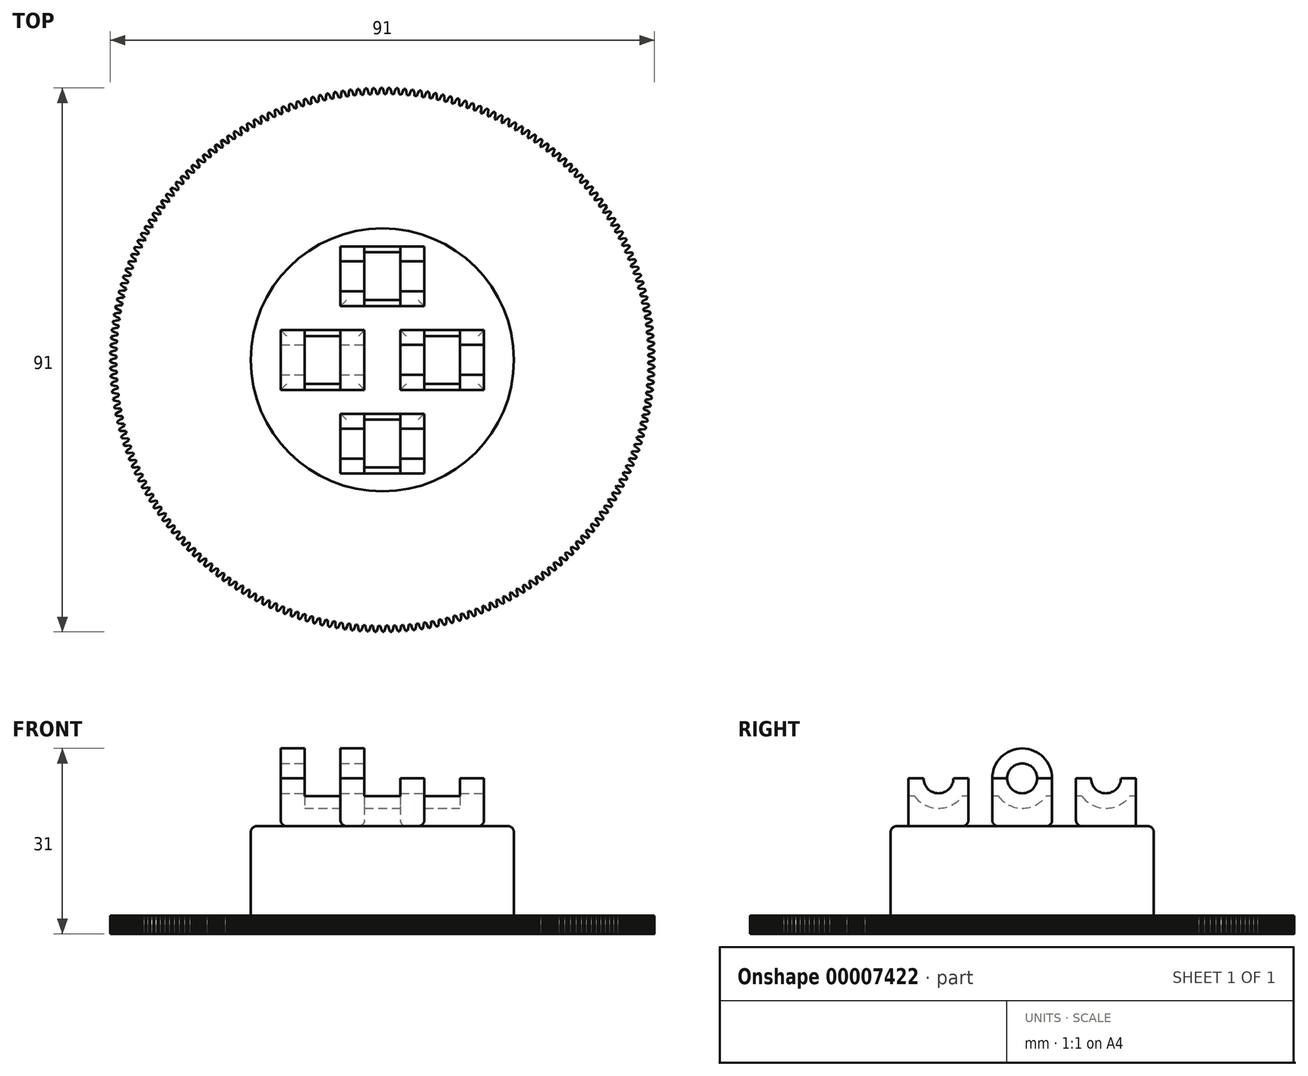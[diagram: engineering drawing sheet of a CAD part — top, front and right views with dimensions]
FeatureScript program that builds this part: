
annotation { "Feature Type Name" : "Feature", "Feature Type Description" : "" }
export const myFeature = defineFeature(function(context is Context, id is Id, definition is map)
    precondition{}
    {
        {
            var Q0;
            Q0=qCreatedBy(makeId("Top.planeOp"),FACE);
            var sketch = newSketch(context, id + "F0", { "sketchPlane" : qUnion([Q0])});
            skPoint(sketch, "E0.rect.middle", {"position": v(0, 0) * mm});
            skCircle(sketch, "E1", {"center": v(0, 0) * mm, "radius": 45.5 * mm});
            skSolve(sketch);
        }
        {
            var Q0;
            Q0=makeQuery(id+"F0.imprint","IMPRINT",FACE,{"disambiguationData":[TD([[makeQuery(id+"F0.imprint","IMPRINT",EDGE,{"derivedFrom":sQuery(id+"F0.wireOp",EDGE,"E1")}),1.0]])]});
            extrude(context, id + "F1", {"entities" : qUnion([Q0]), "depth" : 3 * mm});
        }
        {
            var Q0;
            Q0=makeQuery(id+"F1.opExtrude","CAP_FACE",FACE,{"disambiguationData":[OSD([sQuery(id+"F0.wireOp",EDGE,"E1")])],"isStart":false});
            var sketch = newSketch(context, id + "F2", { "sketchPlane" : qUnion([Q0])});
            skCircle(sketch, "E2", {"center": v(0, 0) * mm, "radius": 22 * mm});
            skSolve(sketch);
        }
        {
            var Q0;
            Q0=makeQuery(id+"F2.imprint","IMPRINT",FACE,{"disambiguationData":[TD([[makeQuery(id+"F2.imprint","IMPRINT",EDGE,{"derivedFrom":sQuery(id+"F2.wireOp",EDGE,"E2")}),1.0]])]});
            extrude(context, id + "F3", {"entities" : qUnion([Q0]), "operationType" : NewBodyOperationType.ADD, "depth" : 15 * mm});
        }
        {
            var Q0;
            Q0=makeQuery(id+"F3.opExtrude","CAP_FACE",FACE,{"disambiguationData":[OSD([sQuery(id+"F2.wireOp",EDGE,"E2")])],"isStart":false});
            var sketch = newSketch(context, id + "F4", { "sketchPlane" : qUnion([Q0])});
            skLineSegment(sketch, "E3", {"start": v(-22, 0) * mm, "end": v(22, 0) * mm});
            skPoint(sketch, "E4", {"position": v(-20, 0) * mm});
            skPoint(sketch, "E5", {"position": v(-10, 0) * mm});
            skLineSegment(sketch, "E6.rect.bottom", {"start": v(-3, 5) * mm, "end": v(-17, 5) * mm});
            skLineSegment(sketch, "E6.rect.top", {"start": v(-3, -5) * mm, "end": v(-17, -5) * mm});
            skLineSegment(sketch, "E6.rect.left", {"start": v(-3, 5) * mm, "end": v(-3, -5) * mm});
            skLineSegment(sketch, "E6.rect.right", {"start": v(-17, 5) * mm, "end": v(-17, -5) * mm});
            skSolve(sketch);
        }
        {
            var Q0;
            Q0=qSketchRegion(id+"F4",true);
            extrude(context, id + "F5", {"entities" : qUnion([Q0]), "depth" : 8 * mm});
        }
        {
            var Q0;
            Q0=makeQuery(id+"F5.opExtrude","SWEPT_FACE",FACE,{"disambiguationData":[OSD([sQuery(id+"F4.wireOp",EDGE,"E6.rect.left")])]});
            var sketch = newSketch(context, id + "F6", { "sketchPlane" : qUnion([Q0])});
            skPoint(sketch, "E7", {"position": v(0, 26) * mm});
            skCircle(sketch, "E8", {"center": v(0, 26) * mm, "radius": 5 * mm});
            skSolve(sketch);
        }
        {
            var Q0;
            {var subQ0=sQuery(id+"F4.wireOp",EDGE,"E6.rect.left");var subQ1=makeQuery(id+"F5.opExtrude","CAP_EDGE",EDGE,{"disambiguationData":[OSD([subQ0])],"isStart":false});Q0=makeQuery(id+"F6.imprint","IMPRINT",FACE,{"disambiguationData":[TD([[makeQuery(id+"F6.imprint","IMPRINT",EDGE,{"derivedFrom":subQ1}),-1.0]])]});}
            extrude(context, id + "F7", {"entities" : qUnion([Q0]), "oppositeDirection" : true, "depth" : 14 * mm});
        }
        {
            var Q0;
            Q0=makeQuery(id+"F7.opExtrude","CAP_FACE",FACE,{"disambiguationData":[OSD([sQuery(id+"F4.wireOp",EDGE,"E6.rect.left"),sQuery(id+"F6.wireOp",EDGE,"E8")])],"isStart":true});
            var sketch = newSketch(context, id + "F8", { "sketchPlane" : qUnion([Q0])});
            skPoint(sketch, "E9", {"position": v(0, 26) * mm});
            skCircle(sketch, "E10", {"center": v(0, 26) * mm, "radius": 2.5 * mm});
            skSolve(sketch);
        }
        {
            var Q0;
            {var subQ0=makeQuery(id+"F7.opExtrude","CAP_EDGE",EDGE,{"disambiguationData":[OSD([sQuery(id+"F4.wireOp",EDGE,"E6.rect.left")])],"isStart":true});var subQ1=sQuery(id+"F8.wireOp",EDGE,"E10");var subQ3=makeQuery(id+"F8.imprint","INTERSECT",VERTEX,{"disambiguationData":[OD(0.0)],"derivedFrom":[subQ0,subQ1]});Q0=makeQuery(id+"F8.imprint","IMPRINT",FACE,{"disambiguationData":[TD([[makeQuery(id+"F8.imprint","IMPRINT",EDGE,{"disambiguationData":[TD([[subQ3,1.0]])],"derivedFrom":subQ1}),1.0]])]});}
            var Q1;
            {var subQ0=makeQuery(id+"F7.opExtrude","CAP_EDGE",EDGE,{"disambiguationData":[OSD([sQuery(id+"F4.wireOp",EDGE,"E6.rect.left")])],"isStart":true});var subQ1=sQuery(id+"F8.wireOp",EDGE,"E10");var subQ3=makeQuery(id+"F8.imprint","INTERSECT",VERTEX,{"disambiguationData":[OD(0.0)],"derivedFrom":[subQ0,subQ1]});Q1=makeQuery(id+"F8.imprint","IMPRINT",FACE,{"disambiguationData":[TD([[makeQuery(id+"F8.imprint","IMPRINT",EDGE,{"disambiguationData":[TD([[subQ3,-1.0]])],"derivedFrom":subQ1}),1.0]])]});}
            extrude(context, id + "F9", {"entities" : qUnion([Q0, Q1]), "operationType" : NewBodyOperationType.REMOVE, "endBound" : BoundingType.THROUGH_ALL, "oppositeDirection" : true, "depth" : 25 * mm});
        }
        {
            var Q0;
            Q0=makeQuery(id+"F7.opExtrude","CAP_FACE",FACE,{"disambiguationData":[OSD([sQuery(id+"F4.wireOp",EDGE,"E6.rect.left"),sQuery(id+"F6.wireOp",EDGE,"E8")])],"isStart":true});
            cPlane(context, id + "F10", {"entities" : qUnion([Q0]), "cplaneType" : CPlaneType.OFFSET, "offset" : 4 * mm, "oppositeDirection" : true, "width" : 150 * mm, "height" : 150 * mm});
        }
        {
            var Q0;
            Q0=qCreatedBy(id+"F10.planeOp",FACE);
            var sketch = newSketch(context, id + "F11", { "sketchPlane" : qUnion([Q0])});
            skCircle(sketch, "E11", {"center": v(0, 26) * mm, "radius": 5 * mm});
            skSolve(sketch);
        }
        {
            var Q0;
            Q0=qSketchRegion(id+"F11",true);
            extrude(context, id + "F12", {"entities" : qUnion([Q0]), "operationType" : NewBodyOperationType.REMOVE, "oppositeDirection" : true, "depth" : 6 * mm});
        }
        {
            var Q0;
            Q0=makeQuery(id+"F5.opExtrude","SWEPT_FACE",FACE,{"disambiguationData":[OSD([sQuery(id+"F4.wireOp",EDGE,"E6.rect.top")])]});
            var sketch = newSketch(context, id + "F13", { "sketchPlane" : qUnion([Q0])});
            skLineSegment(sketch, "E12.bottom", {"start": v(-13, 26) * mm, "end": v(-7, 26) * mm});
            skLineSegment(sketch, "E12.top", {"start": v(-13, 23) * mm, "end": v(-7, 23) * mm});
            skLineSegment(sketch, "E12.left", {"start": v(-13, 26) * mm, "end": v(-13, 23) * mm});
            skLineSegment(sketch, "E12.right", {"start": v(-7, 26) * mm, "end": v(-7, 23) * mm});
            skSolve(sketch);
        }
        {
            var Q0;
            Q0=makeQuery(id+"F13.imprint","IMPRINT",FACE,{"disambiguationData":[TD([[makeQuery(id+"F13.imprint","IMPRINT",EDGE,{"derivedFrom":sQuery(id+"F13.wireOp",EDGE,"E12.bottom")}),-1.0]])]});
            extrude(context, id + "F14", {"entities" : qUnion([Q0]), "operationType" : NewBodyOperationType.REMOVE, "endBound" : BoundingType.THROUGH_ALL, "oppositeDirection" : true, "depth" : 25 * mm});
        }
        {
            var Q0;
            Q0=makeQuery(id+"F5.opExtrude","SWEPT_BODY",BODY,{"disambiguationData":[OSD([sQuery(id+"F4.wireOp",EDGE,"E6.rect.bottom"),sQuery(id+"F4.wireOp",EDGE,"E6.rect.top"),sQuery(id+"F4.wireOp",EDGE,"E6.rect.left"),sQuery(id+"F4.wireOp",EDGE,"E6.rect.right")])]});
            transform(context, id + "F15", {"entities" : qUnion([Q0]), "transformType" : TransformType.TRANSLATION_3D, "dx" : 20 * mm, "dy" : 0 * mm, "dz" : 0 * mm, "makeCopy" : true});
        }
        {
            var Q0;
            Q0=makeQuery(id+"F5.opExtrude","SWEPT_BODY",BODY,{"disambiguationData":[OSD([sQuery(id+"F4.wireOp",EDGE,"E6.rect.bottom"),sQuery(id+"F4.wireOp",EDGE,"E6.rect.top"),sQuery(id+"F4.wireOp",EDGE,"E6.rect.left"),sQuery(id+"F4.wireOp",EDGE,"E6.rect.right")])]});
            transform(context, id + "F16", {"entities" : qUnion([Q0]), "transformType" : TransformType.TRANSLATION_3D, "dx" : 10 * mm, "dy" : 14 * mm, "dz" : 0 * mm, "makeCopy" : true});
        }
        {
            var Q0;
            Q0=makeQuery(id+"F5.opExtrude","SWEPT_BODY",BODY,{"disambiguationData":[OSD([sQuery(id+"F4.wireOp",EDGE,"E6.rect.bottom"),sQuery(id+"F4.wireOp",EDGE,"E6.rect.top"),sQuery(id+"F4.wireOp",EDGE,"E6.rect.left"),sQuery(id+"F4.wireOp",EDGE,"E6.rect.right")])]});
            transform(context, id + "F17", {"entities" : qUnion([Q0]), "transformType" : TransformType.TRANSLATION_3D, "dx" : 10 * mm, "dy" : -14 * mm, "dz" : 0 * mm, "makeCopy" : true});
        }
        {
            var Q0;
            Q0=makeQuery(id+"F3.opExtrude","CAP_EDGE",EDGE,{"disambiguationData":[OSD([sQuery(id+"F2.wireOp",EDGE,"E2")])],"isStart":false});
            var Q1;
            Q1=makeQuery(id+"FjqFsmPxTx0BuLd_1.opFillet","BLEND_EDGE",EDGE,{"blendedFrom":[makeQuery(id+"F5.opExtrude","CAP_EDGE",EDGE,{"disambiguationData":[OSD([sQuery(id+"F4.wireOp",EDGE,"E6.rect.right")])],"isStart":true}),makeQuery(id+"F3.opExtrude","SWEPT_FACE",FACE,{"disambiguationData":[OSD([sQuery(id+"F2.wireOp",EDGE,"E2")])]})],"blendedInto":[makeQuery(id+"F3.opExtrude","SWEPT_FACE",FACE,{"disambiguationData":[OSD([sQuery(id+"F2.wireOp",EDGE,"E2")])]})]});
            var Q2;
            Q2=makeQuery(id+"FjqFsmPxTx0BuLd_1.opFillet","BLEND_EDGE",EDGE,{"blendedFrom":[makeQuery(id+"F15.opPattern","COPY",EDGE,{"derivedFrom":makeQuery(id+"F5.opExtrude","CAP_EDGE",EDGE,{"disambiguationData":[OSD([sQuery(id+"F4.wireOp",EDGE,"E6.rect.left")])],"isStart":true}),"instanceName":"1"}),makeQuery(id+"F3.opExtrude","SWEPT_FACE",FACE,{"disambiguationData":[OSD([sQuery(id+"F2.wireOp",EDGE,"E2")])]})],"blendedInto":[makeQuery(id+"F3.opExtrude","SWEPT_FACE",FACE,{"disambiguationData":[OSD([sQuery(id+"F2.wireOp",EDGE,"E2")])]})]});
            fillet(context, id + "F18", {"entities" : qUnion([Q0, Q1, Q2]), "radius" : 1 * mm, "tangentPropagation" : true, "allowEdgeOverflow" : false});
        }
        {
            var Q0;
            Q0=makeQuery(id+"F5.opExtrude","CAP_EDGE",EDGE,{"disambiguationData":[OSD([sQuery(id+"F4.wireOp",EDGE,"E6.rect.right")])],"isStart":true});
            var Q1;
            Q1=makeQuery(id+"F16.opPattern","COPY",EDGE,{"derivedFrom":makeQuery(id+"F5.opExtrude","CAP_EDGE",EDGE,{"disambiguationData":[OSD([sQuery(id+"F4.wireOp",EDGE,"E6.rect.right")])],"isStart":true}),"instanceName":"1"});
            var Q2;
            Q2=makeQuery(id+"F17.opPattern","COPY",EDGE,{"derivedFrom":makeQuery(id+"F5.opExtrude","CAP_EDGE",EDGE,{"disambiguationData":[OSD([sQuery(id+"F4.wireOp",EDGE,"E6.rect.right")])],"isStart":true}),"instanceName":"1"});
            var Q3;
            Q3=makeQuery(id+"F17.opPattern","COPY",EDGE,{"derivedFrom":makeQuery(id+"F5.opExtrude","CAP_EDGE",EDGE,{"disambiguationData":[OSD([sQuery(id+"F4.wireOp",EDGE,"E6.rect.left")])],"isStart":true}),"instanceName":"1"});
            var Q4;
            Q4=makeQuery(id+"F15.opPattern","COPY",EDGE,{"derivedFrom":makeQuery(id+"F5.opExtrude","CAP_EDGE",EDGE,{"disambiguationData":[OSD([sQuery(id+"F4.wireOp",EDGE,"E6.rect.left")])],"isStart":true}),"instanceName":"1"});
            var Q5;
            Q5=makeQuery(id+"F16.opPattern","COPY",EDGE,{"derivedFrom":makeQuery(id+"F5.opExtrude","CAP_EDGE",EDGE,{"disambiguationData":[OSD([sQuery(id+"F4.wireOp",EDGE,"E6.rect.left")])],"isStart":true}),"instanceName":"1"});
            var Q6;
            Q6=makeQuery(id+"F15.opPattern","COPY",EDGE,{"derivedFrom":makeQuery(id+"F5.opExtrude","CAP_EDGE",EDGE,{"disambiguationData":[OSD([sQuery(id+"F4.wireOp",EDGE,"E6.rect.right")])],"isStart":true}),"instanceName":"1"});
            var Q7;
            Q7=makeQuery(id+"F5.opExtrude","CAP_EDGE",EDGE,{"disambiguationData":[OSD([sQuery(id+"F4.wireOp",EDGE,"E6.rect.left")])],"isStart":true});
            var Q8;
            Q8=makeQuery(id+"F5.opExtrude","CAP_EDGE",EDGE,{"disambiguationData":[OSD([sQuery(id+"F4.wireOp",EDGE,"E6.rect.top")])],"isStart":true});
            var Q9;
            Q9=makeQuery(id+"F15.opPattern","COPY",EDGE,{"derivedFrom":makeQuery(id+"F5.opExtrude","CAP_EDGE",EDGE,{"disambiguationData":[OSD([sQuery(id+"F4.wireOp",EDGE,"E6.rect.top")])],"isStart":true}),"instanceName":"1"});
            var Q10;
            Q10=makeQuery(id+"F16.opPattern","COPY",EDGE,{"derivedFrom":makeQuery(id+"F5.opExtrude","CAP_EDGE",EDGE,{"disambiguationData":[OSD([sQuery(id+"F4.wireOp",EDGE,"E6.rect.top")])],"isStart":true}),"instanceName":"1"});
            var Q11;
            Q11=makeQuery(id+"F15.opPattern","COPY",EDGE,{"derivedFrom":makeQuery(id+"F5.opExtrude","CAP_EDGE",EDGE,{"disambiguationData":[OSD([sQuery(id+"F4.wireOp",EDGE,"E6.rect.bottom")])],"isStart":true}),"instanceName":"1"});
            var Q12;
            Q12=makeQuery(id+"F5.opExtrude","CAP_EDGE",EDGE,{"disambiguationData":[OSD([sQuery(id+"F4.wireOp",EDGE,"E6.rect.bottom")])],"isStart":true});
            var Q13;
            Q13=makeQuery(id+"F17.opPattern","COPY",EDGE,{"derivedFrom":makeQuery(id+"F5.opExtrude","CAP_EDGE",EDGE,{"disambiguationData":[OSD([sQuery(id+"F4.wireOp",EDGE,"E6.rect.bottom")])],"isStart":true}),"instanceName":"1"});
            fillet(context, id + "F19", {"entities" : qUnion([Q0, Q1, Q2, Q3, Q4, Q5, Q6, Q7, Q8, Q9, Q10, Q11, Q12, Q13]), "radius" : 1 * mm, "tangentPropagation" : true, "allowEdgeOverflow" : false});
        }
        {
            var Q0;
            Q0=makeQuery(id+"F1.opExtrude","CAP_FACE",FACE,{"disambiguationData":[OSD([sQuery(id+"F0.wireOp",EDGE,"E1")])],"isStart":false});
            var sketch = newSketch(context, id + "F20", { "sketchPlane" : qUnion([Q0])});
            skLineSegment(sketch, "E13", {"start": v(0, 0) * mm, "end": v(0, 45.5) * mm, "construction": true});
            skLineSegment(sketch, "E14", {"start": v(0, 0) * mm, "end": v(1, 45.49) * mm, "construction": true});
            skPoint(sketch, "E15", {"position": v(0, 44.5) * mm});
            skPoint(sketch, "E16", {"position": v(0.98, 44.49) * mm});
            skLineSegment(sketch, "E17", {"start": v(0, 44.5) * mm, "end": v(0.98, 44.49) * mm, "construction": true});
            skPoint(sketch, "E18", {"position": v(0.3, 44.5) * mm});
            skPoint(sketch, "E19", {"position": v(0.68, 44.5) * mm});
            skPoint(sketch, "E20", {"position": v(0.99, 44.99) * mm});
            skPoint(sketch, "E21", {"position": v(0, 44.99) * mm});
            skLineSegment(sketch, "E22", {"start": v(0, 44.99) * mm, "end": v(0.99, 44.99) * mm, "construction": true});
            skPoint(sketch, "E23", {"position": v(0.2, 44.99) * mm});
            skPoint(sketch, "E24", {"position": v(0.79, 44.99) * mm});
            skLineSegment(sketch, "E25", {"start": v(0, 45.5) * mm, "end": v(0.2, 44.99) * mm});
            skLineSegment(sketch, "E26", {"start": v(0.2, 44.99) * mm, "end": v(0.3, 44.5) * mm});
            skLineSegment(sketch, "E27", {"start": v(0.68, 44.5) * mm, "end": v(0.3, 44.5) * mm});
            skLineSegment(sketch, "E28", {"start": v(0.68, 44.5) * mm, "end": v(0.79, 44.99) * mm});
            skLineSegment(sketch, "E29", {"start": v(1, 45.49) * mm, "end": v(0.79, 44.99) * mm});
            skLineSegment(sketch, "E30.1.0", {"start": v(-1.3, 45.48) * mm, "end": v(-1.08, 44.98) * mm});
            skLineSegment(sketch, "E30.1.1", {"start": v(-1.08, 44.98) * mm, "end": v(-0.97, 44.49) * mm});
            skLineSegment(sketch, "E30.1.2", {"start": v(-0.6, 44.5) * mm, "end": v(-0.97, 44.49) * mm});
            skLineSegment(sketch, "E30.1.3", {"start": v(-0.6, 44.5) * mm, "end": v(-0.5, 45) * mm});
            skLineSegment(sketch, "E30.1.4", {"start": v(-0.3, 45.5) * mm, "end": v(-0.5, 45) * mm});
            skLineSegment(sketch, "E30.2.0", {"start": v(-2.6, 45.43) * mm, "end": v(-2.37, 44.93) * mm});
            skLineSegment(sketch, "E30.2.1", {"start": v(-2.37, 44.93) * mm, "end": v(-2.24, 44.44) * mm});
            skLineSegment(sketch, "E30.2.2", {"start": v(-1.86, 44.46) * mm, "end": v(-2.24, 44.44) * mm});
            skLineSegment(sketch, "E30.2.3", {"start": v(-1.86, 44.46) * mm, "end": v(-1.78, 44.96) * mm});
            skLineSegment(sketch, "E30.2.4", {"start": v(-1.6, 45.47) * mm, "end": v(-1.78, 44.96) * mm});
            skLineSegment(sketch, "E30.3.0", {"start": v(-3.9, 45.33) * mm, "end": v(-3.65, 44.84) * mm});
            skLineSegment(sketch, "E30.3.1", {"start": v(-3.65, 44.84) * mm, "end": v(-3.5, 44.36) * mm});
            skLineSegment(sketch, "E30.3.2", {"start": v(-3.13, 44.39) * mm, "end": v(-3.5, 44.36) * mm});
            skLineSegment(sketch, "E30.3.3", {"start": v(-3.13, 44.39) * mm, "end": v(-3.06, 44.9) * mm});
            skLineSegment(sketch, "E30.3.4", {"start": v(-2.9, 45.4) * mm, "end": v(-3.06, 44.9) * mm});
            skLineSegment(sketch, "E30.4.0", {"start": v(-5.19, 45.2) * mm, "end": v(-4.93, 44.72) * mm});
            skLineSegment(sketch, "E30.4.1", {"start": v(-4.93, 44.72) * mm, "end": v(-4.77, 44.24) * mm});
            skLineSegment(sketch, "E30.4.2", {"start": v(-4.4, 44.28) * mm, "end": v(-4.77, 44.24) * mm});
            skLineSegment(sketch, "E30.4.3", {"start": v(-4.4, 44.28) * mm, "end": v(-4.34, 44.79) * mm});
            skLineSegment(sketch, "E30.4.4", {"start": v(-4.2, 45.3) * mm, "end": v(-4.34, 44.79) * mm});
            skLineSegment(sketch, "E30.5.0", {"start": v(-6.48, 45.04) * mm, "end": v(-6.2, 44.56) * mm});
            skLineSegment(sketch, "E30.5.1", {"start": v(-6.2, 44.56) * mm, "end": v(-6.04, 44.09) * mm});
            skLineSegment(sketch, "E30.5.2", {"start": v(-5.66, 44.14) * mm, "end": v(-6.04, 44.09) * mm});
            skLineSegment(sketch, "E30.5.3", {"start": v(-5.66, 44.14) * mm, "end": v(-5.62, 44.64) * mm});
            skLineSegment(sketch, "E30.5.4", {"start": v(-5.48, 45.17) * mm, "end": v(-5.62, 44.64) * mm});
            skLineSegment(sketch, "E30.6.0", {"start": v(-7.76, 44.83) * mm, "end": v(-7.47, 44.36) * mm});
            skLineSegment(sketch, "E30.6.1", {"start": v(-7.47, 44.36) * mm, "end": v(-7.3, 43.9) * mm});
            skLineSegment(sketch, "E30.6.2", {"start": v(-6.92, 43.96) * mm, "end": v(-7.3, 43.9) * mm});
            skLineSegment(sketch, "E30.6.3", {"start": v(-6.92, 43.96) * mm, "end": v(-6.9, 44.46) * mm});
            skLineSegment(sketch, "E30.6.4", {"start": v(-6.77, 45) * mm, "end": v(-6.9, 44.46) * mm});
            skLineSegment(sketch, "E30.7.0", {"start": v(-9.04, 44.6) * mm, "end": v(-8.74, 44.13) * mm});
            skLineSegment(sketch, "E30.7.1", {"start": v(-8.74, 44.13) * mm, "end": v(-8.54, 43.67) * mm});
            skLineSegment(sketch, "E30.7.2", {"start": v(-8.17, 43.74) * mm, "end": v(-8.54, 43.67) * mm});
            skLineSegment(sketch, "E30.7.3", {"start": v(-8.17, 43.74) * mm, "end": v(-8.16, 44.25) * mm});
            skLineSegment(sketch, "E30.7.4", {"start": v(-8.05, 44.78) * mm, "end": v(-8.16, 44.25) * mm});
            skLineSegment(sketch, "E30.8.0", {"start": v(-10.3, 44.32) * mm, "end": v(-10, 43.87) * mm});
            skLineSegment(sketch, "E30.8.1", {"start": v(-10, 43.87) * mm, "end": v(-9.79, 43.4) * mm});
            skLineSegment(sketch, "E30.8.2", {"start": v(-9.42, 43.49) * mm, "end": v(-9.79, 43.4) * mm});
            skLineSegment(sketch, "E30.8.3", {"start": v(-9.42, 43.49) * mm, "end": v(-9.42, 44) * mm});
            skLineSegment(sketch, "E30.8.4", {"start": v(-9.33, 44.53) * mm, "end": v(-9.42, 44) * mm});
            skLineSegment(sketch, "E30.9.0", {"start": v(-11.57, 44) * mm, "end": v(-11.24, 43.56) * mm});
            skLineSegment(sketch, "E30.9.1", {"start": v(-11.24, 43.56) * mm, "end": v(-11.02, 43.11) * mm});
            skLineSegment(sketch, "E30.9.2", {"start": v(-10.66, 43.2) * mm, "end": v(-11.02, 43.11) * mm});
            skLineSegment(sketch, "E30.9.3", {"start": v(-10.66, 43.2) * mm, "end": v(-10.67, 43.71) * mm});
            skLineSegment(sketch, "E30.9.4", {"start": v(-10.6, 44.25) * mm, "end": v(-10.67, 43.71) * mm});
            skLineSegment(sketch, "E30.10.0", {"start": v(-12.82, 43.66) * mm, "end": v(-12.48, 43.22) * mm});
            skLineSegment(sketch, "E30.10.1", {"start": v(-12.48, 43.22) * mm, "end": v(-12.25, 42.78) * mm});
            skLineSegment(sketch, "E30.10.2", {"start": v(-11.88, 42.88) * mm, "end": v(-12.25, 42.78) * mm});
            skLineSegment(sketch, "E30.10.3", {"start": v(-11.88, 42.88) * mm, "end": v(-11.92, 43.39) * mm});
            skLineSegment(sketch, "E30.10.4", {"start": v(-11.86, 43.93) * mm, "end": v(-11.92, 43.39) * mm});
            skLineSegment(sketch, "E30.11.0", {"start": v(-14.06, 43.27) * mm, "end": v(-13.71, 42.85) * mm});
            skLineSegment(sketch, "E30.11.1", {"start": v(-13.71, 42.85) * mm, "end": v(-13.46, 42.41) * mm});
            skLineSegment(sketch, "E30.11.2", {"start": v(-13.1, 42.52) * mm, "end": v(-13.46, 42.41) * mm});
            skLineSegment(sketch, "E30.11.3", {"start": v(-13.1, 42.52) * mm, "end": v(-13.15, 43.03) * mm});
            skLineSegment(sketch, "E30.11.4", {"start": v(-13.1, 43.57) * mm, "end": v(-13.15, 43.03) * mm});
            skLineSegment(sketch, "E30.12.0", {"start": v(-15.3, 42.85) * mm, "end": v(-14.93, 42.44) * mm});
            skLineSegment(sketch, "E30.12.1", {"start": v(-14.93, 42.44) * mm, "end": v(-14.67, 42) * mm});
            skLineSegment(sketch, "E30.12.2", {"start": v(-14.31, 42.13) * mm, "end": v(-14.67, 42) * mm});
            skLineSegment(sketch, "E30.12.3", {"start": v(-14.31, 42.13) * mm, "end": v(-14.38, 42.64) * mm});
            skLineSegment(sketch, "E30.12.4", {"start": v(-14.34, 43.18) * mm, "end": v(-14.38, 42.64) * mm});
            skLineSegment(sketch, "E30.13.0", {"start": v(-16.5, 42.4) * mm, "end": v(-16.14, 42) * mm});
            skLineSegment(sketch, "E30.13.1", {"start": v(-16.14, 42) * mm, "end": v(-15.86, 41.57) * mm});
            skLineSegment(sketch, "E30.13.2", {"start": v(-15.51, 41.7) * mm, "end": v(-15.86, 41.57) * mm});
            skLineSegment(sketch, "E30.13.3", {"start": v(-15.51, 41.7) * mm, "end": v(-15.59, 42.2) * mm});
            skLineSegment(sketch, "E30.13.4", {"start": v(-15.57, 42.75) * mm, "end": v(-15.59, 42.2) * mm});
            skLineSegment(sketch, "E30.14.0", {"start": v(-17.71, 41.91) * mm, "end": v(-17.33, 41.52) * mm});
            skLineSegment(sketch, "E30.14.1", {"start": v(-17.33, 41.52) * mm, "end": v(-17.04, 41.1) * mm});
            skLineSegment(sketch, "E30.14.2", {"start": v(-16.7, 41.25) * mm, "end": v(-17.04, 41.1) * mm});
            skLineSegment(sketch, "E30.14.3", {"start": v(-16.7, 41.25) * mm, "end": v(-16.79, 41.75) * mm});
            skLineSegment(sketch, "E30.14.4", {"start": v(-16.79, 42.3) * mm, "end": v(-16.79, 41.75) * mm});
            skLineSegment(sketch, "E30.15.0", {"start": v(-18.9, 41.39) * mm, "end": v(-18.5, 41) * mm});
            skLineSegment(sketch, "E30.15.1", {"start": v(-18.5, 41) * mm, "end": v(-18.21, 40.6) * mm});
            skLineSegment(sketch, "E30.15.2", {"start": v(-17.87, 40.75) * mm, "end": v(-18.21, 40.6) * mm});
            skLineSegment(sketch, "E30.15.3", {"start": v(-17.87, 40.75) * mm, "end": v(-17.97, 41.25) * mm});
            skLineSegment(sketch, "E30.15.4", {"start": v(-17.99, 41.8) * mm, "end": v(-17.97, 41.25) * mm});
            skLineSegment(sketch, "E30.16.0", {"start": v(-20.08, 40.83) * mm, "end": v(-19.67, 40.46) * mm});
            skLineSegment(sketch, "E30.16.1", {"start": v(-19.67, 40.46) * mm, "end": v(-19.36, 40.06) * mm});
            skLineSegment(sketch, "E30.16.2", {"start": v(-19.02, 40.23) * mm, "end": v(-19.36, 40.06) * mm});
            skLineSegment(sketch, "E30.16.3", {"start": v(-19.02, 40.23) * mm, "end": v(-19.14, 40.72) * mm});
            skLineSegment(sketch, "E30.16.4", {"start": v(-19.17, 41.26) * mm, "end": v(-19.14, 40.72) * mm});
            skLineSegment(sketch, "E30.17.0", {"start": v(-21.23, 40.24) * mm, "end": v(-20.82, 39.88) * mm});
            skLineSegment(sketch, "E30.17.1", {"start": v(-20.82, 39.88) * mm, "end": v(-20.5, 39.5) * mm});
            skLineSegment(sketch, "E30.17.2", {"start": v(-20.16, 39.67) * mm, "end": v(-20.5, 39.5) * mm});
            skLineSegment(sketch, "E30.17.3", {"start": v(-20.16, 39.67) * mm, "end": v(-20.3, 40.16) * mm});
            skLineSegment(sketch, "E30.17.4", {"start": v(-20.34, 40.7) * mm, "end": v(-20.3, 40.16) * mm});
            skLineSegment(sketch, "E30.18.0", {"start": v(-22.37, 39.62) * mm, "end": v(-21.95, 39.27) * mm});
            skLineSegment(sketch, "E30.18.1", {"start": v(-21.95, 39.27) * mm, "end": v(-21.62, 38.9) * mm});
            skLineSegment(sketch, "E30.18.2", {"start": v(-21.29, 39.07) * mm, "end": v(-21.62, 38.9) * mm});
            skLineSegment(sketch, "E30.18.3", {"start": v(-21.29, 39.07) * mm, "end": v(-21.44, 39.56) * mm});
            skLineSegment(sketch, "E30.18.4", {"start": v(-21.5, 40.1) * mm, "end": v(-21.44, 39.56) * mm});
            skLineSegment(sketch, "E30.19.0", {"start": v(-23.5, 38.96) * mm, "end": v(-23.06, 38.63) * mm});
            skLineSegment(sketch, "E30.19.1", {"start": v(-23.06, 38.63) * mm, "end": v(-22.72, 38.26) * mm});
            skLineSegment(sketch, "E30.19.2", {"start": v(-22.4, 38.45) * mm, "end": v(-22.72, 38.26) * mm});
            skLineSegment(sketch, "E30.19.3", {"start": v(-22.4, 38.45) * mm, "end": v(-22.56, 38.93) * mm});
            skLineSegment(sketch, "E30.19.4", {"start": v(-22.63, 39.47) * mm, "end": v(-22.56, 38.93) * mm});
            skLineSegment(sketch, "E30.20.0", {"start": v(-24.6, 38.28) * mm, "end": v(-24.15, 37.96) * mm});
            skLineSegment(sketch, "E30.20.1", {"start": v(-24.15, 37.96) * mm, "end": v(-23.8, 37.6) * mm});
            skLineSegment(sketch, "E30.20.2", {"start": v(-23.48, 37.8) * mm, "end": v(-23.8, 37.6) * mm});
            skLineSegment(sketch, "E30.20.3", {"start": v(-23.48, 37.8) * mm, "end": v(-23.66, 38.27) * mm});
            skLineSegment(sketch, "E30.20.4", {"start": v(-23.75, 38.8) * mm, "end": v(-23.66, 38.27) * mm});
            skLineSegment(sketch, "E30.21.0", {"start": v(-25.68, 37.56) * mm, "end": v(-25.23, 37.25) * mm});
            skLineSegment(sketch, "E30.21.1", {"start": v(-25.23, 37.25) * mm, "end": v(-24.87, 36.9) * mm});
            skLineSegment(sketch, "E30.21.2", {"start": v(-24.55, 37.1) * mm, "end": v(-24.87, 36.9) * mm});
            skLineSegment(sketch, "E30.21.3", {"start": v(-24.55, 37.1) * mm, "end": v(-24.74, 37.58) * mm});
            skLineSegment(sketch, "E30.21.4", {"start": v(-24.85, 38.11) * mm, "end": v(-24.74, 37.58) * mm});
            skLineSegment(sketch, "E30.22.0", {"start": v(-26.74, 36.81) * mm, "end": v(-26.28, 36.51) * mm});
            skLineSegment(sketch, "E30.22.1", {"start": v(-26.28, 36.51) * mm, "end": v(-25.91, 36.17) * mm});
            skLineSegment(sketch, "E30.22.2", {"start": v(-25.6, 36.4) * mm, "end": v(-25.91, 36.17) * mm});
            skLineSegment(sketch, "E30.22.3", {"start": v(-25.6, 36.4) * mm, "end": v(-25.8, 36.86) * mm});
            skLineSegment(sketch, "E30.22.4", {"start": v(-25.93, 37.39) * mm, "end": v(-25.8, 36.86) * mm});
            skLineSegment(sketch, "E30.23.0", {"start": v(-27.78, 36.03) * mm, "end": v(-27.31, 35.75) * mm});
            skLineSegment(sketch, "E30.23.1", {"start": v(-27.31, 35.75) * mm, "end": v(-26.93, 35.42) * mm});
            skLineSegment(sketch, "E30.23.2", {"start": v(-26.63, 35.65) * mm, "end": v(-26.93, 35.42) * mm});
            skLineSegment(sketch, "E30.23.3", {"start": v(-26.63, 35.65) * mm, "end": v(-26.85, 36.1) * mm});
            skLineSegment(sketch, "E30.23.4", {"start": v(-26.99, 36.63) * mm, "end": v(-26.85, 36.1) * mm});
            skLineSegment(sketch, "E30.24.0", {"start": v(-28.8, 35.22) * mm, "end": v(-28.32, 34.95) * mm});
            skLineSegment(sketch, "E30.24.1", {"start": v(-28.32, 34.95) * mm, "end": v(-27.93, 34.64) * mm});
            skLineSegment(sketch, "E30.24.2", {"start": v(-27.64, 34.87) * mm, "end": v(-27.93, 34.64) * mm});
            skLineSegment(sketch, "E30.24.3", {"start": v(-27.64, 34.87) * mm, "end": v(-27.87, 35.33) * mm});
            skLineSegment(sketch, "E30.24.4", {"start": v(-28.02, 35.85) * mm, "end": v(-27.87, 35.33) * mm});
            skLineSegment(sketch, "E30.25.0", {"start": v(-29.8, 34.39) * mm, "end": v(-29.31, 34.13) * mm});
            skLineSegment(sketch, "E30.25.1", {"start": v(-29.31, 34.13) * mm, "end": v(-28.91, 33.82) * mm});
            skLineSegment(sketch, "E30.25.2", {"start": v(-28.62, 34.07) * mm, "end": v(-28.91, 33.82) * mm});
            skLineSegment(sketch, "E30.25.3", {"start": v(-28.62, 34.07) * mm, "end": v(-28.87, 34.52) * mm});
            skLineSegment(sketch, "E30.25.4", {"start": v(-29.03, 35.03) * mm, "end": v(-28.87, 34.52) * mm});
            skLineSegment(sketch, "E30.26.0", {"start": v(-30.77, 33.52) * mm, "end": v(-30.27, 33.28) * mm});
            skLineSegment(sketch, "E30.26.1", {"start": v(-30.27, 33.28) * mm, "end": v(-29.87, 32.99) * mm});
            skLineSegment(sketch, "E30.26.2", {"start": v(-29.59, 33.24) * mm, "end": v(-29.87, 32.99) * mm});
            skLineSegment(sketch, "E30.26.3", {"start": v(-29.59, 33.24) * mm, "end": v(-29.84, 33.68) * mm});
            skLineSegment(sketch, "E30.26.4", {"start": v(-30.02, 34.19) * mm, "end": v(-29.84, 33.68) * mm});
            skLineSegment(sketch, "E30.27.0", {"start": v(-31.71, 32.63) * mm, "end": v(-31.21, 32.4) * mm});
            skLineSegment(sketch, "E30.27.1", {"start": v(-31.21, 32.4) * mm, "end": v(-30.8, 32.12) * mm});
            skLineSegment(sketch, "E30.27.2", {"start": v(-30.52, 32.38) * mm, "end": v(-30.8, 32.12) * mm});
            skLineSegment(sketch, "E30.27.3", {"start": v(-30.52, 32.38) * mm, "end": v(-30.79, 32.81) * mm});
            skLineSegment(sketch, "E30.27.4", {"start": v(-30.99, 33.32) * mm, "end": v(-30.79, 32.81) * mm});
            skLineSegment(sketch, "E30.28.0", {"start": v(-32.63, 31.71) * mm, "end": v(-32.12, 31.5) * mm});
            skLineSegment(sketch, "E30.28.1", {"start": v(-32.12, 31.5) * mm, "end": v(-31.7, 31.23) * mm});
            skLineSegment(sketch, "E30.28.2", {"start": v(-31.43, 31.5) * mm, "end": v(-31.7, 31.23) * mm});
            skLineSegment(sketch, "E30.28.3", {"start": v(-31.43, 31.5) * mm, "end": v(-31.71, 31.92) * mm});
            skLineSegment(sketch, "E30.28.4", {"start": v(-31.92, 32.42) * mm, "end": v(-31.71, 31.92) * mm});
            skLineSegment(sketch, "E30.29.0", {"start": v(-33.52, 30.77) * mm, "end": v(-33.01, 30.57) * mm});
            skLineSegment(sketch, "E30.29.1", {"start": v(-33.01, 30.57) * mm, "end": v(-32.58, 30.3) * mm});
            skLineSegment(sketch, "E30.29.2", {"start": v(-32.32, 30.58) * mm, "end": v(-32.58, 30.3) * mm});
            skLineSegment(sketch, "E30.29.3", {"start": v(-32.32, 30.58) * mm, "end": v(-32.61, 31) * mm});
            skLineSegment(sketch, "E30.29.4", {"start": v(-32.84, 31.5) * mm, "end": v(-32.61, 31) * mm});
            skLineSegment(sketch, "E30.30.0", {"start": v(-34.39, 29.8) * mm, "end": v(-33.87, 29.61) * mm});
            skLineSegment(sketch, "E30.30.1", {"start": v(-33.87, 29.61) * mm, "end": v(-33.43, 29.37) * mm});
            skLineSegment(sketch, "E30.30.2", {"start": v(-33.18, 29.65) * mm, "end": v(-33.43, 29.37) * mm});
            skLineSegment(sketch, "E30.30.3", {"start": v(-33.18, 29.65) * mm, "end": v(-33.48, 30.06) * mm});
            skLineSegment(sketch, "E30.30.4", {"start": v(-33.72, 30.54) * mm, "end": v(-33.48, 30.06) * mm});
            skLineSegment(sketch, "E30.31.0", {"start": v(-35.22, 28.8) * mm, "end": v(-34.7, 28.63) * mm});
            skLineSegment(sketch, "E30.31.1", {"start": v(-34.7, 28.63) * mm, "end": v(-34.26, 28.4) * mm});
            skLineSegment(sketch, "E30.31.2", {"start": v(-34.01, 28.69) * mm, "end": v(-34.26, 28.4) * mm});
            skLineSegment(sketch, "E30.31.3", {"start": v(-34.01, 28.69) * mm, "end": v(-34.33, 29.09) * mm});
            skLineSegment(sketch, "E30.31.4", {"start": v(-34.58, 29.57) * mm, "end": v(-34.33, 29.09) * mm});
            skLineSegment(sketch, "E30.32.0", {"start": v(-36.03, 27.78) * mm, "end": v(-35.5, 27.63) * mm});
            skLineSegment(sketch, "E30.32.1", {"start": v(-35.5, 27.63) * mm, "end": v(-35.05, 27.4) * mm});
            skLineSegment(sketch, "E30.32.2", {"start": v(-34.82, 27.7) * mm, "end": v(-35.05, 27.4) * mm});
            skLineSegment(sketch, "E30.32.3", {"start": v(-34.82, 27.7) * mm, "end": v(-35.15, 28.1) * mm});
            skLineSegment(sketch, "E30.32.4", {"start": v(-35.41, 28.57) * mm, "end": v(-35.15, 28.1) * mm});
            skLineSegment(sketch, "E30.33.0", {"start": v(-36.81, 26.74) * mm, "end": v(-36.28, 26.6) * mm});
            skLineSegment(sketch, "E30.33.1", {"start": v(-36.28, 26.6) * mm, "end": v(-35.82, 26.4) * mm});
            skLineSegment(sketch, "E30.33.2", {"start": v(-35.6, 26.7) * mm, "end": v(-35.82, 26.4) * mm});
            skLineSegment(sketch, "E30.33.3", {"start": v(-35.6, 26.7) * mm, "end": v(-35.93, 27.08) * mm});
            skLineSegment(sketch, "E30.33.4", {"start": v(-36.21, 27.55) * mm, "end": v(-35.93, 27.08) * mm});
            skLineSegment(sketch, "E30.34.0", {"start": v(-37.56, 25.68) * mm, "end": v(-37.02, 25.56) * mm});
            skLineSegment(sketch, "E30.34.1", {"start": v(-37.02, 25.56) * mm, "end": v(-36.56, 25.36) * mm});
            skLineSegment(sketch, "E30.34.2", {"start": v(-36.34, 25.67) * mm, "end": v(-36.56, 25.36) * mm});
            skLineSegment(sketch, "E30.34.3", {"start": v(-36.34, 25.67) * mm, "end": v(-36.7, 26.04) * mm});
            skLineSegment(sketch, "E30.34.4", {"start": v(-36.99, 26.5) * mm, "end": v(-36.7, 26.04) * mm});
            skLineSegment(sketch, "E30.35.0", {"start": v(-38.28, 24.6) * mm, "end": v(-37.74, 24.5) * mm});
            skLineSegment(sketch, "E30.35.1", {"start": v(-37.74, 24.5) * mm, "end": v(-37.27, 24.3) * mm});
            skLineSegment(sketch, "E30.35.2", {"start": v(-37.06, 24.62) * mm, "end": v(-37.27, 24.3) * mm});
            skLineSegment(sketch, "E30.35.3", {"start": v(-37.06, 24.62) * mm, "end": v(-37.42, 24.99) * mm});
            skLineSegment(sketch, "E30.35.4", {"start": v(-37.73, 25.43) * mm, "end": v(-37.42, 24.99) * mm});
            skLineSegment(sketch, "E30.36.0", {"start": v(-38.96, 23.5) * mm, "end": v(-38.42, 23.4) * mm});
            skLineSegment(sketch, "E30.36.1", {"start": v(-38.42, 23.4) * mm, "end": v(-37.95, 23.23) * mm});
            skLineSegment(sketch, "E30.36.2", {"start": v(-37.75, 23.56) * mm, "end": v(-37.95, 23.23) * mm});
            skLineSegment(sketch, "E30.36.3", {"start": v(-37.75, 23.56) * mm, "end": v(-38.12, 23.9) * mm});
            skLineSegment(sketch, "E30.36.4", {"start": v(-38.44, 24.35) * mm, "end": v(-38.12, 23.9) * mm});
            skLineSegment(sketch, "E30.37.0", {"start": v(-39.62, 22.37) * mm, "end": v(-39.08, 22.3) * mm});
            skLineSegment(sketch, "E30.37.1", {"start": v(-39.08, 22.3) * mm, "end": v(-38.6, 22.14) * mm});
            skLineSegment(sketch, "E30.37.2", {"start": v(-38.4, 22.47) * mm, "end": v(-38.6, 22.14) * mm});
            skLineSegment(sketch, "E30.37.3", {"start": v(-38.4, 22.47) * mm, "end": v(-38.79, 22.8) * mm});
            skLineSegment(sketch, "E30.37.4", {"start": v(-39.12, 23.24) * mm, "end": v(-38.79, 22.8) * mm});
            skLineSegment(sketch, "E30.38.0", {"start": v(-40.24, 21.23) * mm, "end": v(-39.7, 21.17) * mm});
            skLineSegment(sketch, "E30.38.1", {"start": v(-39.7, 21.17) * mm, "end": v(-39.21, 21.03) * mm});
            skLineSegment(sketch, "E30.38.2", {"start": v(-39.03, 21.36) * mm, "end": v(-39.21, 21.03) * mm});
            skLineSegment(sketch, "E30.38.3", {"start": v(-39.03, 21.36) * mm, "end": v(-39.42, 21.7) * mm});
            skLineSegment(sketch, "E30.38.4", {"start": v(-39.77, 22.11) * mm, "end": v(-39.42, 21.7) * mm});
            skLineSegment(sketch, "E30.39.0", {"start": v(-40.83, 20.08) * mm, "end": v(-40.28, 20.03) * mm});
            skLineSegment(sketch, "E30.39.1", {"start": v(-40.28, 20.03) * mm, "end": v(-39.8, 19.9) * mm});
            skLineSegment(sketch, "E30.39.2", {"start": v(-39.63, 20.24) * mm, "end": v(-39.8, 19.9) * mm});
            skLineSegment(sketch, "E30.39.3", {"start": v(-39.63, 20.24) * mm, "end": v(-40.03, 20.56) * mm});
            skLineSegment(sketch, "E30.39.4", {"start": v(-40.38, 20.97) * mm, "end": v(-40.03, 20.56) * mm});
            skLineSegment(sketch, "E30.40.0", {"start": v(-41.39, 18.9) * mm, "end": v(-40.84, 18.87) * mm});
            skLineSegment(sketch, "E30.40.1", {"start": v(-40.84, 18.87) * mm, "end": v(-40.35, 18.76) * mm});
            skLineSegment(sketch, "E30.40.2", {"start": v(-40.2, 19.1) * mm, "end": v(-40.35, 18.76) * mm});
            skLineSegment(sketch, "E30.40.3", {"start": v(-40.2, 19.1) * mm, "end": v(-40.6, 19.4) * mm});
            skLineSegment(sketch, "E30.40.4", {"start": v(-40.96, 19.8) * mm, "end": v(-40.6, 19.4) * mm});
            skLineSegment(sketch, "E30.41.0", {"start": v(-41.91, 17.71) * mm, "end": v(-41.36, 17.7) * mm});
            skLineSegment(sketch, "E30.41.1", {"start": v(-41.36, 17.7) * mm, "end": v(-40.87, 17.6) * mm});
            skLineSegment(sketch, "E30.41.2", {"start": v(-40.72, 17.94) * mm, "end": v(-40.87, 17.6) * mm});
            skLineSegment(sketch, "E30.41.3", {"start": v(-40.72, 17.94) * mm, "end": v(-41.13, 18.24) * mm});
            skLineSegment(sketch, "E30.41.4", {"start": v(-41.51, 18.63) * mm, "end": v(-41.13, 18.24) * mm});
            skLineSegment(sketch, "E30.42.0", {"start": v(-42.4, 16.5) * mm, "end": v(-41.85, 16.5) * mm});
            skLineSegment(sketch, "E30.42.1", {"start": v(-41.85, 16.5) * mm, "end": v(-41.36, 16.42) * mm});
            skLineSegment(sketch, "E30.42.2", {"start": v(-41.21, 16.77) * mm, "end": v(-41.36, 16.42) * mm});
            skLineSegment(sketch, "E30.42.3", {"start": v(-41.21, 16.77) * mm, "end": v(-41.64, 17.06) * mm});
            skLineSegment(sketch, "E30.42.4", {"start": v(-42.03, 17.44) * mm, "end": v(-41.64, 17.06) * mm});
            skLineSegment(sketch, "E30.43.0", {"start": v(-42.85, 15.3) * mm, "end": v(-42.3, 15.3) * mm});
            skLineSegment(sketch, "E30.43.1", {"start": v(-42.3, 15.3) * mm, "end": v(-41.8, 15.24) * mm});
            skLineSegment(sketch, "E30.43.2", {"start": v(-41.68, 15.59) * mm, "end": v(-41.8, 15.24) * mm});
            skLineSegment(sketch, "E30.43.3", {"start": v(-41.68, 15.59) * mm, "end": v(-42.1, 15.86) * mm});
            skLineSegment(sketch, "E30.43.4", {"start": v(-42.5, 16.23) * mm, "end": v(-42.1, 15.86) * mm});
            skLineSegment(sketch, "E30.44.0", {"start": v(-43.27, 14.06) * mm, "end": v(-42.73, 14.1) * mm});
            skLineSegment(sketch, "E30.44.1", {"start": v(-42.73, 14.1) * mm, "end": v(-42.23, 14.04) * mm});
            skLineSegment(sketch, "E30.44.2", {"start": v(-42.1, 14.4) * mm, "end": v(-42.23, 14.04) * mm});
            skLineSegment(sketch, "E30.44.3", {"start": v(-42.1, 14.4) * mm, "end": v(-42.54, 14.65) * mm});
            skLineSegment(sketch, "E30.44.4", {"start": v(-42.95, 15) * mm, "end": v(-42.54, 14.65) * mm});
            skLineSegment(sketch, "E30.45.0", {"start": v(-43.66, 12.82) * mm, "end": v(-43.11, 12.87) * mm});
            skLineSegment(sketch, "E30.45.1", {"start": v(-43.11, 12.87) * mm, "end": v(-42.6, 12.82) * mm});
            skLineSegment(sketch, "E30.45.2", {"start": v(-42.5, 13.19) * mm, "end": v(-42.6, 12.82) * mm});
            skLineSegment(sketch, "E30.45.3", {"start": v(-42.5, 13.19) * mm, "end": v(-42.94, 13.43) * mm});
            skLineSegment(sketch, "E30.45.4", {"start": v(-43.36, 13.77) * mm, "end": v(-42.94, 13.43) * mm});
            skLineSegment(sketch, "E30.46.0", {"start": v(-44, 11.57) * mm, "end": v(-43.46, 11.63) * mm});
            skLineSegment(sketch, "E30.46.1", {"start": v(-43.46, 11.63) * mm, "end": v(-42.96, 11.6) * mm});
            skLineSegment(sketch, "E30.46.2", {"start": v(-42.86, 11.97) * mm, "end": v(-42.96, 11.6) * mm});
            skLineSegment(sketch, "E30.46.3", {"start": v(-42.86, 11.97) * mm, "end": v(-43.31, 12.2) * mm});
            skLineSegment(sketch, "E30.46.4", {"start": v(-43.74, 12.53) * mm, "end": v(-43.31, 12.2) * mm});
            skLineSegment(sketch, "E30.47.0", {"start": v(-44.32, 10.3) * mm, "end": v(-43.77, 10.38) * mm});
            skLineSegment(sketch, "E30.47.1", {"start": v(-43.77, 10.38) * mm, "end": v(-43.27, 10.37) * mm});
            skLineSegment(sketch, "E30.47.2", {"start": v(-43.18, 10.74) * mm, "end": v(-43.27, 10.37) * mm});
            skLineSegment(sketch, "E30.47.3", {"start": v(-43.18, 10.74) * mm, "end": v(-43.64, 10.96) * mm});
            skLineSegment(sketch, "E30.47.4", {"start": v(-44.08, 11.28) * mm, "end": v(-43.64, 10.96) * mm});
            skLineSegment(sketch, "E30.48.0", {"start": v(-44.6, 9.04) * mm, "end": v(-44.05, 9.13) * mm});
            skLineSegment(sketch, "E30.48.1", {"start": v(-44.05, 9.13) * mm, "end": v(-43.55, 9.13) * mm});
            skLineSegment(sketch, "E30.48.2", {"start": v(-43.47, 9.5) * mm, "end": v(-43.55, 9.13) * mm});
            skLineSegment(sketch, "E30.48.3", {"start": v(-43.47, 9.5) * mm, "end": v(-43.94, 9.7) * mm});
            skLineSegment(sketch, "E30.48.4", {"start": v(-44.38, 10.01) * mm, "end": v(-43.94, 9.7) * mm});
            skLineSegment(sketch, "E30.49.0", {"start": v(-44.83, 7.76) * mm, "end": v(-44.3, 7.87) * mm});
            skLineSegment(sketch, "E30.49.1", {"start": v(-44.3, 7.87) * mm, "end": v(-43.8, 7.88) * mm});
            skLineSegment(sketch, "E30.49.2", {"start": v(-43.73, 8.25) * mm, "end": v(-43.8, 7.88) * mm});
            skLineSegment(sketch, "E30.49.3", {"start": v(-43.73, 8.25) * mm, "end": v(-44.2, 8.45) * mm});
            skLineSegment(sketch, "E30.49.4", {"start": v(-44.65, 8.74) * mm, "end": v(-44.2, 8.45) * mm});
            skLineSegment(sketch, "E30.50.0", {"start": v(-45.04, 6.48) * mm, "end": v(-44.5, 6.6) * mm});
            skLineSegment(sketch, "E30.50.1", {"start": v(-44.5, 6.6) * mm, "end": v(-44, 6.63) * mm});
            skLineSegment(sketch, "E30.50.2", {"start": v(-43.94, 7) * mm, "end": v(-44, 6.63) * mm});
            skLineSegment(sketch, "E30.50.3", {"start": v(-43.94, 7) * mm, "end": v(-44.42, 7.18) * mm});
            skLineSegment(sketch, "E30.50.4", {"start": v(-44.88, 7.46) * mm, "end": v(-44.42, 7.18) * mm});
            skLineSegment(sketch, "E30.51.0", {"start": v(-45.2, 5.19) * mm, "end": v(-44.67, 5.33) * mm});
            skLineSegment(sketch, "E30.51.1", {"start": v(-44.67, 5.33) * mm, "end": v(-44.17, 5.37) * mm});
            skLineSegment(sketch, "E30.51.2", {"start": v(-44.13, 5.75) * mm, "end": v(-44.17, 5.37) * mm});
            skLineSegment(sketch, "E30.51.3", {"start": v(-44.13, 5.75) * mm, "end": v(-44.6, 5.91) * mm});
            skLineSegment(sketch, "E30.51.4", {"start": v(-45.08, 6.18) * mm, "end": v(-44.6, 5.91) * mm});
            skLineSegment(sketch, "E30.52.0", {"start": v(-45.33, 3.9) * mm, "end": v(-44.8, 4.05) * mm});
            skLineSegment(sketch, "E30.52.1", {"start": v(-44.8, 4.05) * mm, "end": v(-44.3, 4.1) * mm});
            skLineSegment(sketch, "E30.52.2", {"start": v(-44.27, 4.48) * mm, "end": v(-44.3, 4.1) * mm});
            skLineSegment(sketch, "E30.52.3", {"start": v(-44.27, 4.48) * mm, "end": v(-44.76, 4.64) * mm});
            skLineSegment(sketch, "E30.52.4", {"start": v(-45.24, 4.89) * mm, "end": v(-44.76, 4.64) * mm});
            skLineSegment(sketch, "E30.53.0", {"start": v(-45.43, 2.6) * mm, "end": v(-44.9, 2.77) * mm});
            skLineSegment(sketch, "E30.53.1", {"start": v(-44.9, 2.77) * mm, "end": v(-44.4, 2.84) * mm});
            skLineSegment(sketch, "E30.53.2", {"start": v(-44.38, 3.22) * mm, "end": v(-44.4, 2.84) * mm});
            skLineSegment(sketch, "E30.53.3", {"start": v(-44.38, 3.22) * mm, "end": v(-44.87, 3.36) * mm});
            skLineSegment(sketch, "E30.53.4", {"start": v(-45.36, 3.6) * mm, "end": v(-44.87, 3.36) * mm});
            skLineSegment(sketch, "E30.54.0", {"start": v(-45.48, 1.3) * mm, "end": v(-44.96, 1.48) * mm});
            skLineSegment(sketch, "E30.54.1", {"start": v(-44.96, 1.48) * mm, "end": v(-44.47, 1.57) * mm});
            skLineSegment(sketch, "E30.54.2", {"start": v(-44.45, 1.95) * mm, "end": v(-44.47, 1.57) * mm});
            skLineSegment(sketch, "E30.54.3", {"start": v(-44.45, 1.95) * mm, "end": v(-44.95, 2.07) * mm});
            skLineSegment(sketch, "E30.54.4", {"start": v(-45.44, 2.3) * mm, "end": v(-44.95, 2.07) * mm});
            skLineSegment(sketch, "E30.55.0", {"start": v(-45.5, 0) * mm, "end": v(-44.99, 0.2) * mm});
            skLineSegment(sketch, "E30.55.1", {"start": v(-44.99, 0.2) * mm, "end": v(-44.5, 0.3) * mm});
            skLineSegment(sketch, "E30.55.2", {"start": v(-44.5, 0.68) * mm, "end": v(-44.5, 0.3) * mm});
            skLineSegment(sketch, "E30.55.3", {"start": v(-44.5, 0.68) * mm, "end": v(-44.99, 0.79) * mm});
            skLineSegment(sketch, "E30.55.4", {"start": v(-45.49, 1) * mm, "end": v(-44.99, 0.79) * mm});
            skLineSegment(sketch, "E30.56.0", {"start": v(-45.48, -1.3) * mm, "end": v(-44.98, -1.08) * mm});
            skLineSegment(sketch, "E30.56.1", {"start": v(-44.98, -1.08) * mm, "end": v(-44.49, -0.97) * mm});
            skLineSegment(sketch, "E30.56.2", {"start": v(-44.5, -0.6) * mm, "end": v(-44.49, -0.97) * mm});
            skLineSegment(sketch, "E30.56.3", {"start": v(-44.5, -0.6) * mm, "end": v(-45, -0.5) * mm});
            skLineSegment(sketch, "E30.56.4", {"start": v(-45.5, -0.3) * mm, "end": v(-45, -0.5) * mm});
            skLineSegment(sketch, "E30.57.0", {"start": v(-45.43, -2.6) * mm, "end": v(-44.93, -2.37) * mm});
            skLineSegment(sketch, "E30.57.1", {"start": v(-44.93, -2.37) * mm, "end": v(-44.44, -2.24) * mm});
            skLineSegment(sketch, "E30.57.2", {"start": v(-44.46, -1.86) * mm, "end": v(-44.44, -2.24) * mm});
            skLineSegment(sketch, "E30.57.3", {"start": v(-44.46, -1.86) * mm, "end": v(-44.96, -1.78) * mm});
            skLineSegment(sketch, "E30.57.4", {"start": v(-45.47, -1.6) * mm, "end": v(-44.96, -1.78) * mm});
            skLineSegment(sketch, "E30.58.0", {"start": v(-45.33, -3.9) * mm, "end": v(-44.84, -3.65) * mm});
            skLineSegment(sketch, "E30.58.1", {"start": v(-44.84, -3.65) * mm, "end": v(-44.36, -3.5) * mm});
            skLineSegment(sketch, "E30.58.2", {"start": v(-44.39, -3.13) * mm, "end": v(-44.36, -3.5) * mm});
            skLineSegment(sketch, "E30.58.3", {"start": v(-44.39, -3.13) * mm, "end": v(-44.9, -3.06) * mm});
            skLineSegment(sketch, "E30.58.4", {"start": v(-45.4, -2.9) * mm, "end": v(-44.9, -3.06) * mm});
            skLineSegment(sketch, "E30.59.0", {"start": v(-45.2, -5.19) * mm, "end": v(-44.72, -4.93) * mm});
            skLineSegment(sketch, "E30.59.1", {"start": v(-44.72, -4.93) * mm, "end": v(-44.24, -4.77) * mm});
            skLineSegment(sketch, "E30.59.2", {"start": v(-44.28, -4.4) * mm, "end": v(-44.24, -4.77) * mm});
            skLineSegment(sketch, "E30.59.3", {"start": v(-44.28, -4.4) * mm, "end": v(-44.79, -4.34) * mm});
            skLineSegment(sketch, "E30.59.4", {"start": v(-45.3, -4.2) * mm, "end": v(-44.79, -4.34) * mm});
            skLineSegment(sketch, "E30.60.0", {"start": v(-45.04, -6.48) * mm, "end": v(-44.56, -6.2) * mm});
            skLineSegment(sketch, "E30.60.1", {"start": v(-44.56, -6.2) * mm, "end": v(-44.09, -6.04) * mm});
            skLineSegment(sketch, "E30.60.2", {"start": v(-44.14, -5.66) * mm, "end": v(-44.09, -6.04) * mm});
            skLineSegment(sketch, "E30.60.3", {"start": v(-44.14, -5.66) * mm, "end": v(-44.64, -5.62) * mm});
            skLineSegment(sketch, "E30.60.4", {"start": v(-45.17, -5.48) * mm, "end": v(-44.64, -5.62) * mm});
            skLineSegment(sketch, "E30.61.0", {"start": v(-44.83, -7.76) * mm, "end": v(-44.36, -7.47) * mm});
            skLineSegment(sketch, "E30.61.1", {"start": v(-44.36, -7.47) * mm, "end": v(-43.9, -7.3) * mm});
            skLineSegment(sketch, "E30.61.2", {"start": v(-43.96, -6.92) * mm, "end": v(-43.9, -7.3) * mm});
            skLineSegment(sketch, "E30.61.3", {"start": v(-43.96, -6.92) * mm, "end": v(-44.46, -6.9) * mm});
            skLineSegment(sketch, "E30.61.4", {"start": v(-45, -6.77) * mm, "end": v(-44.46, -6.9) * mm});
            skLineSegment(sketch, "E30.62.0", {"start": v(-44.6, -9.04) * mm, "end": v(-44.13, -8.74) * mm});
            skLineSegment(sketch, "E30.62.1", {"start": v(-44.13, -8.74) * mm, "end": v(-43.67, -8.54) * mm});
            skLineSegment(sketch, "E30.62.2", {"start": v(-43.74, -8.17) * mm, "end": v(-43.67, -8.54) * mm});
            skLineSegment(sketch, "E30.62.3", {"start": v(-43.74, -8.17) * mm, "end": v(-44.25, -8.16) * mm});
            skLineSegment(sketch, "E30.62.4", {"start": v(-44.78, -8.05) * mm, "end": v(-44.25, -8.16) * mm});
            skLineSegment(sketch, "E30.63.0", {"start": v(-44.32, -10.3) * mm, "end": v(-43.87, -10) * mm});
            skLineSegment(sketch, "E30.63.1", {"start": v(-43.87, -10) * mm, "end": v(-43.4, -9.79) * mm});
            skLineSegment(sketch, "E30.63.2", {"start": v(-43.49, -9.42) * mm, "end": v(-43.4, -9.79) * mm});
            skLineSegment(sketch, "E30.63.3", {"start": v(-43.49, -9.42) * mm, "end": v(-44, -9.42) * mm});
            skLineSegment(sketch, "E30.63.4", {"start": v(-44.53, -9.33) * mm, "end": v(-44, -9.42) * mm});
            skLineSegment(sketch, "E30.64.0", {"start": v(-44, -11.57) * mm, "end": v(-43.56, -11.24) * mm});
            skLineSegment(sketch, "E30.64.1", {"start": v(-43.56, -11.24) * mm, "end": v(-43.11, -11.02) * mm});
            skLineSegment(sketch, "E30.64.2", {"start": v(-43.2, -10.66) * mm, "end": v(-43.11, -11.02) * mm});
            skLineSegment(sketch, "E30.64.3", {"start": v(-43.2, -10.66) * mm, "end": v(-43.71, -10.67) * mm});
            skLineSegment(sketch, "E30.64.4", {"start": v(-44.25, -10.6) * mm, "end": v(-43.71, -10.67) * mm});
            skLineSegment(sketch, "E30.65.0", {"start": v(-43.66, -12.82) * mm, "end": v(-43.22, -12.48) * mm});
            skLineSegment(sketch, "E30.65.1", {"start": v(-43.22, -12.48) * mm, "end": v(-42.78, -12.25) * mm});
            skLineSegment(sketch, "E30.65.2", {"start": v(-42.88, -11.88) * mm, "end": v(-42.78, -12.25) * mm});
            skLineSegment(sketch, "E30.65.3", {"start": v(-42.88, -11.88) * mm, "end": v(-43.39, -11.92) * mm});
            skLineSegment(sketch, "E30.65.4", {"start": v(-43.93, -11.86) * mm, "end": v(-43.39, -11.92) * mm});
            skLineSegment(sketch, "E30.66.0", {"start": v(-43.27, -14.06) * mm, "end": v(-42.85, -13.71) * mm});
            skLineSegment(sketch, "E30.66.1", {"start": v(-42.85, -13.71) * mm, "end": v(-42.41, -13.46) * mm});
            skLineSegment(sketch, "E30.66.2", {"start": v(-42.52, -13.1) * mm, "end": v(-42.41, -13.46) * mm});
            skLineSegment(sketch, "E30.66.3", {"start": v(-42.52, -13.1) * mm, "end": v(-43.03, -13.15) * mm});
            skLineSegment(sketch, "E30.66.4", {"start": v(-43.57, -13.1) * mm, "end": v(-43.03, -13.15) * mm});
            skLineSegment(sketch, "E30.67.0", {"start": v(-42.85, -15.3) * mm, "end": v(-42.44, -14.93) * mm});
            skLineSegment(sketch, "E30.67.1", {"start": v(-42.44, -14.93) * mm, "end": v(-42, -14.67) * mm});
            skLineSegment(sketch, "E30.67.2", {"start": v(-42.13, -14.31) * mm, "end": v(-42, -14.67) * mm});
            skLineSegment(sketch, "E30.67.3", {"start": v(-42.13, -14.31) * mm, "end": v(-42.64, -14.38) * mm});
            skLineSegment(sketch, "E30.67.4", {"start": v(-43.18, -14.34) * mm, "end": v(-42.64, -14.38) * mm});
            skLineSegment(sketch, "E30.68.0", {"start": v(-42.4, -16.5) * mm, "end": v(-42, -16.14) * mm});
            skLineSegment(sketch, "E30.68.1", {"start": v(-42, -16.14) * mm, "end": v(-41.57, -15.86) * mm});
            skLineSegment(sketch, "E30.68.2", {"start": v(-41.7, -15.51) * mm, "end": v(-41.57, -15.86) * mm});
            skLineSegment(sketch, "E30.68.3", {"start": v(-41.7, -15.51) * mm, "end": v(-42.2, -15.59) * mm});
            skLineSegment(sketch, "E30.68.4", {"start": v(-42.75, -15.57) * mm, "end": v(-42.2, -15.59) * mm});
            skLineSegment(sketch, "E30.69.0", {"start": v(-41.91, -17.71) * mm, "end": v(-41.52, -17.33) * mm});
            skLineSegment(sketch, "E30.69.1", {"start": v(-41.52, -17.33) * mm, "end": v(-41.1, -17.04) * mm});
            skLineSegment(sketch, "E30.69.2", {"start": v(-41.25, -16.7) * mm, "end": v(-41.1, -17.04) * mm});
            skLineSegment(sketch, "E30.69.3", {"start": v(-41.25, -16.7) * mm, "end": v(-41.75, -16.79) * mm});
            skLineSegment(sketch, "E30.69.4", {"start": v(-42.3, -16.79) * mm, "end": v(-41.75, -16.79) * mm});
            skLineSegment(sketch, "E30.70.0", {"start": v(-41.39, -18.9) * mm, "end": v(-41, -18.5) * mm});
            skLineSegment(sketch, "E30.70.1", {"start": v(-41, -18.5) * mm, "end": v(-40.6, -18.21) * mm});
            skLineSegment(sketch, "E30.70.2", {"start": v(-40.75, -17.87) * mm, "end": v(-40.6, -18.21) * mm});
            skLineSegment(sketch, "E30.70.3", {"start": v(-40.75, -17.87) * mm, "end": v(-41.25, -17.97) * mm});
            skLineSegment(sketch, "E30.70.4", {"start": v(-41.8, -17.99) * mm, "end": v(-41.25, -17.97) * mm});
            skLineSegment(sketch, "E30.71.0", {"start": v(-40.83, -20.08) * mm, "end": v(-40.46, -19.67) * mm});
            skLineSegment(sketch, "E30.71.1", {"start": v(-40.46, -19.67) * mm, "end": v(-40.06, -19.36) * mm});
            skLineSegment(sketch, "E30.71.2", {"start": v(-40.23, -19.02) * mm, "end": v(-40.06, -19.36) * mm});
            skLineSegment(sketch, "E30.71.3", {"start": v(-40.23, -19.02) * mm, "end": v(-40.72, -19.14) * mm});
            skLineSegment(sketch, "E30.71.4", {"start": v(-41.26, -19.17) * mm, "end": v(-40.72, -19.14) * mm});
            skLineSegment(sketch, "E30.72.0", {"start": v(-40.24, -21.23) * mm, "end": v(-39.88, -20.82) * mm});
            skLineSegment(sketch, "E30.72.1", {"start": v(-39.88, -20.82) * mm, "end": v(-39.5, -20.5) * mm});
            skLineSegment(sketch, "E30.72.2", {"start": v(-39.67, -20.16) * mm, "end": v(-39.5, -20.5) * mm});
            skLineSegment(sketch, "E30.72.3", {"start": v(-39.67, -20.16) * mm, "end": v(-40.16, -20.3) * mm});
            skLineSegment(sketch, "E30.72.4", {"start": v(-40.7, -20.34) * mm, "end": v(-40.16, -20.3) * mm});
            skLineSegment(sketch, "E30.73.0", {"start": v(-39.62, -22.37) * mm, "end": v(-39.27, -21.95) * mm});
            skLineSegment(sketch, "E30.73.1", {"start": v(-39.27, -21.95) * mm, "end": v(-38.9, -21.62) * mm});
            skLineSegment(sketch, "E30.73.2", {"start": v(-39.07, -21.29) * mm, "end": v(-38.9, -21.62) * mm});
            skLineSegment(sketch, "E30.73.3", {"start": v(-39.07, -21.29) * mm, "end": v(-39.56, -21.44) * mm});
            skLineSegment(sketch, "E30.73.4", {"start": v(-40.1, -21.5) * mm, "end": v(-39.56, -21.44) * mm});
            skLineSegment(sketch, "E30.74.0", {"start": v(-38.96, -23.5) * mm, "end": v(-38.63, -23.06) * mm});
            skLineSegment(sketch, "E30.74.1", {"start": v(-38.63, -23.06) * mm, "end": v(-38.26, -22.72) * mm});
            skLineSegment(sketch, "E30.74.2", {"start": v(-38.45, -22.4) * mm, "end": v(-38.26, -22.72) * mm});
            skLineSegment(sketch, "E30.74.3", {"start": v(-38.45, -22.4) * mm, "end": v(-38.93, -22.56) * mm});
            skLineSegment(sketch, "E30.74.4", {"start": v(-39.47, -22.63) * mm, "end": v(-38.93, -22.56) * mm});
            skLineSegment(sketch, "E30.75.0", {"start": v(-38.28, -24.6) * mm, "end": v(-37.96, -24.15) * mm});
            skLineSegment(sketch, "E30.75.1", {"start": v(-37.96, -24.15) * mm, "end": v(-37.6, -23.8) * mm});
            skLineSegment(sketch, "E30.75.2", {"start": v(-37.8, -23.48) * mm, "end": v(-37.6, -23.8) * mm});
            skLineSegment(sketch, "E30.75.3", {"start": v(-37.8, -23.48) * mm, "end": v(-38.27, -23.66) * mm});
            skLineSegment(sketch, "E30.75.4", {"start": v(-38.8, -23.75) * mm, "end": v(-38.27, -23.66) * mm});
            skLineSegment(sketch, "E30.76.0", {"start": v(-37.56, -25.68) * mm, "end": v(-37.25, -25.23) * mm});
            skLineSegment(sketch, "E30.76.1", {"start": v(-37.25, -25.23) * mm, "end": v(-36.9, -24.87) * mm});
            skLineSegment(sketch, "E30.76.2", {"start": v(-37.1, -24.55) * mm, "end": v(-36.9, -24.87) * mm});
            skLineSegment(sketch, "E30.76.3", {"start": v(-37.1, -24.55) * mm, "end": v(-37.58, -24.74) * mm});
            skLineSegment(sketch, "E30.76.4", {"start": v(-38.11, -24.85) * mm, "end": v(-37.58, -24.74) * mm});
            skLineSegment(sketch, "E30.77.0", {"start": v(-36.81, -26.74) * mm, "end": v(-36.51, -26.28) * mm});
            skLineSegment(sketch, "E30.77.1", {"start": v(-36.51, -26.28) * mm, "end": v(-36.17, -25.91) * mm});
            skLineSegment(sketch, "E30.77.2", {"start": v(-36.4, -25.6) * mm, "end": v(-36.17, -25.91) * mm});
            skLineSegment(sketch, "E30.77.3", {"start": v(-36.4, -25.6) * mm, "end": v(-36.86, -25.8) * mm});
            skLineSegment(sketch, "E30.77.4", {"start": v(-37.39, -25.93) * mm, "end": v(-36.86, -25.8) * mm});
            skLineSegment(sketch, "E30.78.0", {"start": v(-36.03, -27.78) * mm, "end": v(-35.75, -27.31) * mm});
            skLineSegment(sketch, "E30.78.1", {"start": v(-35.75, -27.31) * mm, "end": v(-35.42, -26.93) * mm});
            skLineSegment(sketch, "E30.78.2", {"start": v(-35.65, -26.63) * mm, "end": v(-35.42, -26.93) * mm});
            skLineSegment(sketch, "E30.78.3", {"start": v(-35.65, -26.63) * mm, "end": v(-36.1, -26.85) * mm});
            skLineSegment(sketch, "E30.78.4", {"start": v(-36.63, -26.99) * mm, "end": v(-36.1, -26.85) * mm});
            skLineSegment(sketch, "E30.79.0", {"start": v(-35.22, -28.8) * mm, "end": v(-34.95, -28.32) * mm});
            skLineSegment(sketch, "E30.79.1", {"start": v(-34.95, -28.32) * mm, "end": v(-34.64, -27.93) * mm});
            skLineSegment(sketch, "E30.79.2", {"start": v(-34.87, -27.64) * mm, "end": v(-34.64, -27.93) * mm});
            skLineSegment(sketch, "E30.79.3", {"start": v(-34.87, -27.64) * mm, "end": v(-35.33, -27.87) * mm});
            skLineSegment(sketch, "E30.79.4", {"start": v(-35.85, -28.02) * mm, "end": v(-35.33, -27.87) * mm});
            skLineSegment(sketch, "E30.80.0", {"start": v(-34.39, -29.8) * mm, "end": v(-34.13, -29.31) * mm});
            skLineSegment(sketch, "E30.80.1", {"start": v(-34.13, -29.31) * mm, "end": v(-33.82, -28.91) * mm});
            skLineSegment(sketch, "E30.80.2", {"start": v(-34.07, -28.62) * mm, "end": v(-33.82, -28.91) * mm});
            skLineSegment(sketch, "E30.80.3", {"start": v(-34.07, -28.62) * mm, "end": v(-34.52, -28.87) * mm});
            skLineSegment(sketch, "E30.80.4", {"start": v(-35.03, -29.03) * mm, "end": v(-34.52, -28.87) * mm});
            skLineSegment(sketch, "E30.81.0", {"start": v(-33.52, -30.77) * mm, "end": v(-33.28, -30.27) * mm});
            skLineSegment(sketch, "E30.81.1", {"start": v(-33.28, -30.27) * mm, "end": v(-32.99, -29.87) * mm});
            skLineSegment(sketch, "E30.81.2", {"start": v(-33.24, -29.59) * mm, "end": v(-32.99, -29.87) * mm});
            skLineSegment(sketch, "E30.81.3", {"start": v(-33.24, -29.59) * mm, "end": v(-33.68, -29.84) * mm});
            skLineSegment(sketch, "E30.81.4", {"start": v(-34.19, -30.02) * mm, "end": v(-33.68, -29.84) * mm});
            skLineSegment(sketch, "E30.82.0", {"start": v(-32.63, -31.71) * mm, "end": v(-32.4, -31.21) * mm});
            skLineSegment(sketch, "E30.82.1", {"start": v(-32.4, -31.21) * mm, "end": v(-32.12, -30.8) * mm});
            skLineSegment(sketch, "E30.82.2", {"start": v(-32.38, -30.52) * mm, "end": v(-32.12, -30.8) * mm});
            skLineSegment(sketch, "E30.82.3", {"start": v(-32.38, -30.52) * mm, "end": v(-32.81, -30.79) * mm});
            skLineSegment(sketch, "E30.82.4", {"start": v(-33.32, -30.99) * mm, "end": v(-32.81, -30.79) * mm});
            skLineSegment(sketch, "E30.83.0", {"start": v(-31.71, -32.63) * mm, "end": v(-31.5, -32.12) * mm});
            skLineSegment(sketch, "E30.83.1", {"start": v(-31.5, -32.12) * mm, "end": v(-31.23, -31.7) * mm});
            skLineSegment(sketch, "E30.83.2", {"start": v(-31.5, -31.43) * mm, "end": v(-31.23, -31.7) * mm});
            skLineSegment(sketch, "E30.83.3", {"start": v(-31.5, -31.43) * mm, "end": v(-31.92, -31.71) * mm});
            skLineSegment(sketch, "E30.83.4", {"start": v(-32.42, -31.92) * mm, "end": v(-31.92, -31.71) * mm});
            skLineSegment(sketch, "E30.84.0", {"start": v(-30.77, -33.52) * mm, "end": v(-30.57, -33.01) * mm});
            skLineSegment(sketch, "E30.84.1", {"start": v(-30.57, -33.01) * mm, "end": v(-30.3, -32.58) * mm});
            skLineSegment(sketch, "E30.84.2", {"start": v(-30.58, -32.32) * mm, "end": v(-30.3, -32.58) * mm});
            skLineSegment(sketch, "E30.84.3", {"start": v(-30.58, -32.32) * mm, "end": v(-31, -32.61) * mm});
            skLineSegment(sketch, "E30.84.4", {"start": v(-31.5, -32.84) * mm, "end": v(-31, -32.61) * mm});
            skLineSegment(sketch, "E30.85.0", {"start": v(-29.8, -34.39) * mm, "end": v(-29.61, -33.87) * mm});
            skLineSegment(sketch, "E30.85.1", {"start": v(-29.61, -33.87) * mm, "end": v(-29.37, -33.43) * mm});
            skLineSegment(sketch, "E30.85.2", {"start": v(-29.65, -33.18) * mm, "end": v(-29.37, -33.43) * mm});
            skLineSegment(sketch, "E30.85.3", {"start": v(-29.65, -33.18) * mm, "end": v(-30.06, -33.48) * mm});
            skLineSegment(sketch, "E30.85.4", {"start": v(-30.54, -33.72) * mm, "end": v(-30.06, -33.48) * mm});
            skLineSegment(sketch, "E30.86.0", {"start": v(-28.8, -35.22) * mm, "end": v(-28.63, -34.7) * mm});
            skLineSegment(sketch, "E30.86.1", {"start": v(-28.63, -34.7) * mm, "end": v(-28.4, -34.26) * mm});
            skLineSegment(sketch, "E30.86.2", {"start": v(-28.69, -34.01) * mm, "end": v(-28.4, -34.26) * mm});
            skLineSegment(sketch, "E30.86.3", {"start": v(-28.69, -34.01) * mm, "end": v(-29.09, -34.33) * mm});
            skLineSegment(sketch, "E30.86.4", {"start": v(-29.57, -34.58) * mm, "end": v(-29.09, -34.33) * mm});
            skLineSegment(sketch, "E30.87.0", {"start": v(-27.78, -36.03) * mm, "end": v(-27.63, -35.5) * mm});
            skLineSegment(sketch, "E30.87.1", {"start": v(-27.63, -35.5) * mm, "end": v(-27.4, -35.05) * mm});
            skLineSegment(sketch, "E30.87.2", {"start": v(-27.7, -34.82) * mm, "end": v(-27.4, -35.05) * mm});
            skLineSegment(sketch, "E30.87.3", {"start": v(-27.7, -34.82) * mm, "end": v(-28.1, -35.15) * mm});
            skLineSegment(sketch, "E30.87.4", {"start": v(-28.57, -35.41) * mm, "end": v(-28.1, -35.15) * mm});
            skLineSegment(sketch, "E30.88.0", {"start": v(-26.74, -36.81) * mm, "end": v(-26.6, -36.28) * mm});
            skLineSegment(sketch, "E30.88.1", {"start": v(-26.6, -36.28) * mm, "end": v(-26.4, -35.82) * mm});
            skLineSegment(sketch, "E30.88.2", {"start": v(-26.7, -35.6) * mm, "end": v(-26.4, -35.82) * mm});
            skLineSegment(sketch, "E30.88.3", {"start": v(-26.7, -35.6) * mm, "end": v(-27.08, -35.93) * mm});
            skLineSegment(sketch, "E30.88.4", {"start": v(-27.55, -36.21) * mm, "end": v(-27.08, -35.93) * mm});
            skLineSegment(sketch, "E30.89.0", {"start": v(-25.68, -37.56) * mm, "end": v(-25.56, -37.02) * mm});
            skLineSegment(sketch, "E30.89.1", {"start": v(-25.56, -37.02) * mm, "end": v(-25.36, -36.56) * mm});
            skLineSegment(sketch, "E30.89.2", {"start": v(-25.67, -36.34) * mm, "end": v(-25.36, -36.56) * mm});
            skLineSegment(sketch, "E30.89.3", {"start": v(-25.67, -36.34) * mm, "end": v(-26.04, -36.7) * mm});
            skLineSegment(sketch, "E30.89.4", {"start": v(-26.5, -36.99) * mm, "end": v(-26.04, -36.7) * mm});
            skLineSegment(sketch, "E30.90.0", {"start": v(-24.6, -38.28) * mm, "end": v(-24.5, -37.74) * mm});
            skLineSegment(sketch, "E30.90.1", {"start": v(-24.5, -37.74) * mm, "end": v(-24.3, -37.27) * mm});
            skLineSegment(sketch, "E30.90.2", {"start": v(-24.62, -37.06) * mm, "end": v(-24.3, -37.27) * mm});
            skLineSegment(sketch, "E30.90.3", {"start": v(-24.62, -37.06) * mm, "end": v(-24.99, -37.42) * mm});
            skLineSegment(sketch, "E30.90.4", {"start": v(-25.43, -37.73) * mm, "end": v(-24.99, -37.42) * mm});
            skLineSegment(sketch, "E30.91.0", {"start": v(-23.5, -38.96) * mm, "end": v(-23.4, -38.42) * mm});
            skLineSegment(sketch, "E30.91.1", {"start": v(-23.4, -38.42) * mm, "end": v(-23.23, -37.95) * mm});
            skLineSegment(sketch, "E30.91.2", {"start": v(-23.56, -37.75) * mm, "end": v(-23.23, -37.95) * mm});
            skLineSegment(sketch, "E30.91.3", {"start": v(-23.56, -37.75) * mm, "end": v(-23.9, -38.12) * mm});
            skLineSegment(sketch, "E30.91.4", {"start": v(-24.35, -38.44) * mm, "end": v(-23.9, -38.12) * mm});
            skLineSegment(sketch, "E30.92.0", {"start": v(-22.37, -39.62) * mm, "end": v(-22.3, -39.08) * mm});
            skLineSegment(sketch, "E30.92.1", {"start": v(-22.3, -39.08) * mm, "end": v(-22.14, -38.6) * mm});
            skLineSegment(sketch, "E30.92.2", {"start": v(-22.47, -38.4) * mm, "end": v(-22.14, -38.6) * mm});
            skLineSegment(sketch, "E30.92.3", {"start": v(-22.47, -38.4) * mm, "end": v(-22.8, -38.79) * mm});
            skLineSegment(sketch, "E30.92.4", {"start": v(-23.24, -39.12) * mm, "end": v(-22.8, -38.79) * mm});
            skLineSegment(sketch, "E30.93.0", {"start": v(-21.23, -40.24) * mm, "end": v(-21.17, -39.7) * mm});
            skLineSegment(sketch, "E30.93.1", {"start": v(-21.17, -39.7) * mm, "end": v(-21.03, -39.21) * mm});
            skLineSegment(sketch, "E30.93.2", {"start": v(-21.36, -39.03) * mm, "end": v(-21.03, -39.21) * mm});
            skLineSegment(sketch, "E30.93.3", {"start": v(-21.36, -39.03) * mm, "end": v(-21.7, -39.42) * mm});
            skLineSegment(sketch, "E30.93.4", {"start": v(-22.11, -39.77) * mm, "end": v(-21.7, -39.42) * mm});
            skLineSegment(sketch, "E30.94.0", {"start": v(-20.08, -40.83) * mm, "end": v(-20.03, -40.28) * mm});
            skLineSegment(sketch, "E30.94.1", {"start": v(-20.03, -40.28) * mm, "end": v(-19.9, -39.8) * mm});
            skLineSegment(sketch, "E30.94.2", {"start": v(-20.24, -39.63) * mm, "end": v(-19.9, -39.8) * mm});
            skLineSegment(sketch, "E30.94.3", {"start": v(-20.24, -39.63) * mm, "end": v(-20.56, -40.03) * mm});
            skLineSegment(sketch, "E30.94.4", {"start": v(-20.97, -40.38) * mm, "end": v(-20.56, -40.03) * mm});
            skLineSegment(sketch, "E30.95.0", {"start": v(-18.9, -41.39) * mm, "end": v(-18.87, -40.84) * mm});
            skLineSegment(sketch, "E30.95.1", {"start": v(-18.87, -40.84) * mm, "end": v(-18.76, -40.35) * mm});
            skLineSegment(sketch, "E30.95.2", {"start": v(-19.1, -40.2) * mm, "end": v(-18.76, -40.35) * mm});
            skLineSegment(sketch, "E30.95.3", {"start": v(-19.1, -40.2) * mm, "end": v(-19.4, -40.6) * mm});
            skLineSegment(sketch, "E30.95.4", {"start": v(-19.8, -40.96) * mm, "end": v(-19.4, -40.6) * mm});
            skLineSegment(sketch, "E30.96.0", {"start": v(-17.71, -41.91) * mm, "end": v(-17.7, -41.36) * mm});
            skLineSegment(sketch, "E30.96.1", {"start": v(-17.7, -41.36) * mm, "end": v(-17.6, -40.87) * mm});
            skLineSegment(sketch, "E30.96.2", {"start": v(-17.94, -40.72) * mm, "end": v(-17.6, -40.87) * mm});
            skLineSegment(sketch, "E30.96.3", {"start": v(-17.94, -40.72) * mm, "end": v(-18.24, -41.13) * mm});
            skLineSegment(sketch, "E30.96.4", {"start": v(-18.63, -41.51) * mm, "end": v(-18.24, -41.13) * mm});
            skLineSegment(sketch, "E30.97.0", {"start": v(-16.5, -42.4) * mm, "end": v(-16.5, -41.85) * mm});
            skLineSegment(sketch, "E30.97.1", {"start": v(-16.5, -41.85) * mm, "end": v(-16.42, -41.36) * mm});
            skLineSegment(sketch, "E30.97.2", {"start": v(-16.77, -41.21) * mm, "end": v(-16.42, -41.36) * mm});
            skLineSegment(sketch, "E30.97.3", {"start": v(-16.77, -41.21) * mm, "end": v(-17.06, -41.64) * mm});
            skLineSegment(sketch, "E30.97.4", {"start": v(-17.44, -42.03) * mm, "end": v(-17.06, -41.64) * mm});
            skLineSegment(sketch, "E30.98.0", {"start": v(-15.3, -42.85) * mm, "end": v(-15.3, -42.3) * mm});
            skLineSegment(sketch, "E30.98.1", {"start": v(-15.3, -42.3) * mm, "end": v(-15.24, -41.8) * mm});
            skLineSegment(sketch, "E30.98.2", {"start": v(-15.59, -41.68) * mm, "end": v(-15.24, -41.8) * mm});
            skLineSegment(sketch, "E30.98.3", {"start": v(-15.59, -41.68) * mm, "end": v(-15.86, -42.1) * mm});
            skLineSegment(sketch, "E30.98.4", {"start": v(-16.23, -42.5) * mm, "end": v(-15.86, -42.1) * mm});
            skLineSegment(sketch, "E30.99.0", {"start": v(-14.06, -43.27) * mm, "end": v(-14.1, -42.73) * mm});
            skLineSegment(sketch, "E30.99.1", {"start": v(-14.1, -42.73) * mm, "end": v(-14.04, -42.23) * mm});
            skLineSegment(sketch, "E30.99.2", {"start": v(-14.4, -42.1) * mm, "end": v(-14.04, -42.23) * mm});
            skLineSegment(sketch, "E30.99.3", {"start": v(-14.4, -42.1) * mm, "end": v(-14.65, -42.54) * mm});
            skLineSegment(sketch, "E30.99.4", {"start": v(-15, -42.95) * mm, "end": v(-14.65, -42.54) * mm});
            skLineSegment(sketch, "E30.100.0", {"start": v(-12.82, -43.66) * mm, "end": v(-12.87, -43.11) * mm});
            skLineSegment(sketch, "E30.100.1", {"start": v(-12.87, -43.11) * mm, "end": v(-12.82, -42.6) * mm});
            skLineSegment(sketch, "E30.100.2", {"start": v(-13.19, -42.5) * mm, "end": v(-12.82, -42.6) * mm});
            skLineSegment(sketch, "E30.100.3", {"start": v(-13.19, -42.5) * mm, "end": v(-13.43, -42.94) * mm});
            skLineSegment(sketch, "E30.100.4", {"start": v(-13.77, -43.36) * mm, "end": v(-13.43, -42.94) * mm});
            skLineSegment(sketch, "E30.101.0", {"start": v(-11.57, -44) * mm, "end": v(-11.63, -43.46) * mm});
            skLineSegment(sketch, "E30.101.1", {"start": v(-11.63, -43.46) * mm, "end": v(-11.6, -42.96) * mm});
            skLineSegment(sketch, "E30.101.2", {"start": v(-11.97, -42.86) * mm, "end": v(-11.6, -42.96) * mm});
            skLineSegment(sketch, "E30.101.3", {"start": v(-11.97, -42.86) * mm, "end": v(-12.2, -43.31) * mm});
            skLineSegment(sketch, "E30.101.4", {"start": v(-12.53, -43.74) * mm, "end": v(-12.2, -43.31) * mm});
            skLineSegment(sketch, "E30.102.0", {"start": v(-10.3, -44.32) * mm, "end": v(-10.38, -43.77) * mm});
            skLineSegment(sketch, "E30.102.1", {"start": v(-10.38, -43.77) * mm, "end": v(-10.37, -43.27) * mm});
            skLineSegment(sketch, "E30.102.2", {"start": v(-10.74, -43.18) * mm, "end": v(-10.37, -43.27) * mm});
            skLineSegment(sketch, "E30.102.3", {"start": v(-10.74, -43.18) * mm, "end": v(-10.96, -43.64) * mm});
            skLineSegment(sketch, "E30.102.4", {"start": v(-11.28, -44.08) * mm, "end": v(-10.96, -43.64) * mm});
            skLineSegment(sketch, "E30.103.0", {"start": v(-9.04, -44.6) * mm, "end": v(-9.13, -44.05) * mm});
            skLineSegment(sketch, "E30.103.1", {"start": v(-9.13, -44.05) * mm, "end": v(-9.13, -43.55) * mm});
            skLineSegment(sketch, "E30.103.2", {"start": v(-9.5, -43.47) * mm, "end": v(-9.13, -43.55) * mm});
            skLineSegment(sketch, "E30.103.3", {"start": v(-9.5, -43.47) * mm, "end": v(-9.7, -43.94) * mm});
            skLineSegment(sketch, "E30.103.4", {"start": v(-10.01, -44.38) * mm, "end": v(-9.7, -43.94) * mm});
            skLineSegment(sketch, "E30.104.0", {"start": v(-7.76, -44.83) * mm, "end": v(-7.87, -44.3) * mm});
            skLineSegment(sketch, "E30.104.1", {"start": v(-7.87, -44.3) * mm, "end": v(-7.88, -43.8) * mm});
            skLineSegment(sketch, "E30.104.2", {"start": v(-8.25, -43.73) * mm, "end": v(-7.88, -43.8) * mm});
            skLineSegment(sketch, "E30.104.3", {"start": v(-8.25, -43.73) * mm, "end": v(-8.45, -44.2) * mm});
            skLineSegment(sketch, "E30.104.4", {"start": v(-8.74, -44.65) * mm, "end": v(-8.45, -44.2) * mm});
            skLineSegment(sketch, "E30.105.0", {"start": v(-6.48, -45.04) * mm, "end": v(-6.6, -44.5) * mm});
            skLineSegment(sketch, "E30.105.1", {"start": v(-6.6, -44.5) * mm, "end": v(-6.63, -44) * mm});
            skLineSegment(sketch, "E30.105.2", {"start": v(-7, -43.94) * mm, "end": v(-6.63, -44) * mm});
            skLineSegment(sketch, "E30.105.3", {"start": v(-7, -43.94) * mm, "end": v(-7.18, -44.42) * mm});
            skLineSegment(sketch, "E30.105.4", {"start": v(-7.46, -44.88) * mm, "end": v(-7.18, -44.42) * mm});
            skLineSegment(sketch, "E30.106.0", {"start": v(-5.19, -45.2) * mm, "end": v(-5.33, -44.67) * mm});
            skLineSegment(sketch, "E30.106.1", {"start": v(-5.33, -44.67) * mm, "end": v(-5.37, -44.17) * mm});
            skLineSegment(sketch, "E30.106.2", {"start": v(-5.75, -44.13) * mm, "end": v(-5.37, -44.17) * mm});
            skLineSegment(sketch, "E30.106.3", {"start": v(-5.75, -44.13) * mm, "end": v(-5.91, -44.6) * mm});
            skLineSegment(sketch, "E30.106.4", {"start": v(-6.18, -45.08) * mm, "end": v(-5.91, -44.6) * mm});
            skLineSegment(sketch, "E30.107.0", {"start": v(-3.9, -45.33) * mm, "end": v(-4.05, -44.8) * mm});
            skLineSegment(sketch, "E30.107.1", {"start": v(-4.05, -44.8) * mm, "end": v(-4.1, -44.3) * mm});
            skLineSegment(sketch, "E30.107.2", {"start": v(-4.48, -44.27) * mm, "end": v(-4.1, -44.3) * mm});
            skLineSegment(sketch, "E30.107.3", {"start": v(-4.48, -44.27) * mm, "end": v(-4.64, -44.76) * mm});
            skLineSegment(sketch, "E30.107.4", {"start": v(-4.89, -45.24) * mm, "end": v(-4.64, -44.76) * mm});
            skLineSegment(sketch, "E30.108.0", {"start": v(-2.6, -45.43) * mm, "end": v(-2.77, -44.9) * mm});
            skLineSegment(sketch, "E30.108.1", {"start": v(-2.77, -44.9) * mm, "end": v(-2.84, -44.4) * mm});
            skLineSegment(sketch, "E30.108.2", {"start": v(-3.22, -44.38) * mm, "end": v(-2.84, -44.4) * mm});
            skLineSegment(sketch, "E30.108.3", {"start": v(-3.22, -44.38) * mm, "end": v(-3.36, -44.87) * mm});
            skLineSegment(sketch, "E30.108.4", {"start": v(-3.6, -45.36) * mm, "end": v(-3.36, -44.87) * mm});
            skLineSegment(sketch, "E30.109.0", {"start": v(-1.3, -45.48) * mm, "end": v(-1.48, -44.96) * mm});
            skLineSegment(sketch, "E30.109.1", {"start": v(-1.48, -44.96) * mm, "end": v(-1.57, -44.47) * mm});
            skLineSegment(sketch, "E30.109.2", {"start": v(-1.95, -44.45) * mm, "end": v(-1.57, -44.47) * mm});
            skLineSegment(sketch, "E30.109.3", {"start": v(-1.95, -44.45) * mm, "end": v(-2.07, -44.95) * mm});
            skLineSegment(sketch, "E30.109.4", {"start": v(-2.3, -45.44) * mm, "end": v(-2.07, -44.95) * mm});
            skLineSegment(sketch, "E30.110.0", {"start": v(0, -45.5) * mm, "end": v(-0.2, -44.99) * mm});
            skLineSegment(sketch, "E30.110.1", {"start": v(-0.2, -44.99) * mm, "end": v(-0.3, -44.5) * mm});
            skLineSegment(sketch, "E30.110.2", {"start": v(-0.68, -44.5) * mm, "end": v(-0.3, -44.5) * mm});
            skLineSegment(sketch, "E30.110.3", {"start": v(-0.68, -44.5) * mm, "end": v(-0.79, -44.99) * mm});
            skLineSegment(sketch, "E30.110.4", {"start": v(-1, -45.49) * mm, "end": v(-0.79, -44.99) * mm});
            skLineSegment(sketch, "E30.111.0", {"start": v(1.3, -45.48) * mm, "end": v(1.08, -44.98) * mm});
            skLineSegment(sketch, "E30.111.1", {"start": v(1.08, -44.98) * mm, "end": v(0.97, -44.49) * mm});
            skLineSegment(sketch, "E30.111.2", {"start": v(0.6, -44.5) * mm, "end": v(0.97, -44.49) * mm});
            skLineSegment(sketch, "E30.111.3", {"start": v(0.6, -44.5) * mm, "end": v(0.5, -45) * mm});
            skLineSegment(sketch, "E30.111.4", {"start": v(0.3, -45.5) * mm, "end": v(0.5, -45) * mm});
            skLineSegment(sketch, "E30.112.0", {"start": v(2.6, -45.43) * mm, "end": v(2.37, -44.93) * mm});
            skLineSegment(sketch, "E30.112.1", {"start": v(2.37, -44.93) * mm, "end": v(2.24, -44.44) * mm});
            skLineSegment(sketch, "E30.112.2", {"start": v(1.86, -44.46) * mm, "end": v(2.24, -44.44) * mm});
            skLineSegment(sketch, "E30.112.3", {"start": v(1.86, -44.46) * mm, "end": v(1.78, -44.96) * mm});
            skLineSegment(sketch, "E30.112.4", {"start": v(1.6, -45.47) * mm, "end": v(1.78, -44.96) * mm});
            skLineSegment(sketch, "E30.113.0", {"start": v(3.9, -45.33) * mm, "end": v(3.65, -44.84) * mm});
            skLineSegment(sketch, "E30.113.1", {"start": v(3.65, -44.84) * mm, "end": v(3.5, -44.36) * mm});
            skLineSegment(sketch, "E30.113.2", {"start": v(3.13, -44.39) * mm, "end": v(3.5, -44.36) * mm});
            skLineSegment(sketch, "E30.113.3", {"start": v(3.13, -44.39) * mm, "end": v(3.06, -44.9) * mm});
            skLineSegment(sketch, "E30.113.4", {"start": v(2.9, -45.4) * mm, "end": v(3.06, -44.9) * mm});
            skLineSegment(sketch, "E30.114.0", {"start": v(5.19, -45.2) * mm, "end": v(4.93, -44.72) * mm});
            skLineSegment(sketch, "E30.114.1", {"start": v(4.93, -44.72) * mm, "end": v(4.77, -44.24) * mm});
            skLineSegment(sketch, "E30.114.2", {"start": v(4.4, -44.28) * mm, "end": v(4.77, -44.24) * mm});
            skLineSegment(sketch, "E30.114.3", {"start": v(4.4, -44.28) * mm, "end": v(4.34, -44.79) * mm});
            skLineSegment(sketch, "E30.114.4", {"start": v(4.2, -45.3) * mm, "end": v(4.34, -44.79) * mm});
            skLineSegment(sketch, "E30.115.0", {"start": v(6.48, -45.04) * mm, "end": v(6.2, -44.56) * mm});
            skLineSegment(sketch, "E30.115.1", {"start": v(6.2, -44.56) * mm, "end": v(6.04, -44.09) * mm});
            skLineSegment(sketch, "E30.115.2", {"start": v(5.66, -44.14) * mm, "end": v(6.04, -44.09) * mm});
            skLineSegment(sketch, "E30.115.3", {"start": v(5.66, -44.14) * mm, "end": v(5.62, -44.64) * mm});
            skLineSegment(sketch, "E30.115.4", {"start": v(5.48, -45.17) * mm, "end": v(5.62, -44.64) * mm});
            skLineSegment(sketch, "E30.116.0", {"start": v(7.76, -44.83) * mm, "end": v(7.47, -44.36) * mm});
            skLineSegment(sketch, "E30.116.1", {"start": v(7.47, -44.36) * mm, "end": v(7.3, -43.9) * mm});
            skLineSegment(sketch, "E30.116.2", {"start": v(6.92, -43.96) * mm, "end": v(7.3, -43.9) * mm});
            skLineSegment(sketch, "E30.116.3", {"start": v(6.92, -43.96) * mm, "end": v(6.9, -44.46) * mm});
            skLineSegment(sketch, "E30.116.4", {"start": v(6.77, -45) * mm, "end": v(6.9, -44.46) * mm});
            skLineSegment(sketch, "E30.117.0", {"start": v(9.04, -44.6) * mm, "end": v(8.74, -44.13) * mm});
            skLineSegment(sketch, "E30.117.1", {"start": v(8.74, -44.13) * mm, "end": v(8.54, -43.67) * mm});
            skLineSegment(sketch, "E30.117.2", {"start": v(8.17, -43.74) * mm, "end": v(8.54, -43.67) * mm});
            skLineSegment(sketch, "E30.117.3", {"start": v(8.17, -43.74) * mm, "end": v(8.16, -44.25) * mm});
            skLineSegment(sketch, "E30.117.4", {"start": v(8.05, -44.78) * mm, "end": v(8.16, -44.25) * mm});
            skLineSegment(sketch, "E30.118.0", {"start": v(10.3, -44.32) * mm, "end": v(10, -43.87) * mm});
            skLineSegment(sketch, "E30.118.1", {"start": v(10, -43.87) * mm, "end": v(9.79, -43.4) * mm});
            skLineSegment(sketch, "E30.118.2", {"start": v(9.42, -43.49) * mm, "end": v(9.79, -43.4) * mm});
            skLineSegment(sketch, "E30.118.3", {"start": v(9.42, -43.49) * mm, "end": v(9.42, -44) * mm});
            skLineSegment(sketch, "E30.118.4", {"start": v(9.33, -44.53) * mm, "end": v(9.42, -44) * mm});
            skLineSegment(sketch, "E30.119.0", {"start": v(11.57, -44) * mm, "end": v(11.24, -43.56) * mm});
            skLineSegment(sketch, "E30.119.1", {"start": v(11.24, -43.56) * mm, "end": v(11.02, -43.11) * mm});
            skLineSegment(sketch, "E30.119.2", {"start": v(10.66, -43.2) * mm, "end": v(11.02, -43.11) * mm});
            skLineSegment(sketch, "E30.119.3", {"start": v(10.66, -43.2) * mm, "end": v(10.67, -43.71) * mm});
            skLineSegment(sketch, "E30.119.4", {"start": v(10.6, -44.25) * mm, "end": v(10.67, -43.71) * mm});
            skLineSegment(sketch, "E30.120.0", {"start": v(12.82, -43.66) * mm, "end": v(12.48, -43.22) * mm});
            skLineSegment(sketch, "E30.120.1", {"start": v(12.48, -43.22) * mm, "end": v(12.25, -42.78) * mm});
            skLineSegment(sketch, "E30.120.2", {"start": v(11.88, -42.88) * mm, "end": v(12.25, -42.78) * mm});
            skLineSegment(sketch, "E30.120.3", {"start": v(11.88, -42.88) * mm, "end": v(11.92, -43.39) * mm});
            skLineSegment(sketch, "E30.120.4", {"start": v(11.86, -43.93) * mm, "end": v(11.92, -43.39) * mm});
            skLineSegment(sketch, "E30.121.0", {"start": v(14.06, -43.27) * mm, "end": v(13.71, -42.85) * mm});
            skLineSegment(sketch, "E30.121.1", {"start": v(13.71, -42.85) * mm, "end": v(13.46, -42.41) * mm});
            skLineSegment(sketch, "E30.121.2", {"start": v(13.1, -42.52) * mm, "end": v(13.46, -42.41) * mm});
            skLineSegment(sketch, "E30.121.3", {"start": v(13.1, -42.52) * mm, "end": v(13.15, -43.03) * mm});
            skLineSegment(sketch, "E30.121.4", {"start": v(13.1, -43.57) * mm, "end": v(13.15, -43.03) * mm});
            skLineSegment(sketch, "E30.122.0", {"start": v(15.3, -42.85) * mm, "end": v(14.93, -42.44) * mm});
            skLineSegment(sketch, "E30.122.1", {"start": v(14.93, -42.44) * mm, "end": v(14.67, -42) * mm});
            skLineSegment(sketch, "E30.122.2", {"start": v(14.31, -42.13) * mm, "end": v(14.67, -42) * mm});
            skLineSegment(sketch, "E30.122.3", {"start": v(14.31, -42.13) * mm, "end": v(14.38, -42.64) * mm});
            skLineSegment(sketch, "E30.122.4", {"start": v(14.34, -43.18) * mm, "end": v(14.38, -42.64) * mm});
            skLineSegment(sketch, "E30.123.0", {"start": v(16.5, -42.4) * mm, "end": v(16.14, -42) * mm});
            skLineSegment(sketch, "E30.123.1", {"start": v(16.14, -42) * mm, "end": v(15.86, -41.57) * mm});
            skLineSegment(sketch, "E30.123.2", {"start": v(15.51, -41.7) * mm, "end": v(15.86, -41.57) * mm});
            skLineSegment(sketch, "E30.123.3", {"start": v(15.51, -41.7) * mm, "end": v(15.59, -42.2) * mm});
            skLineSegment(sketch, "E30.123.4", {"start": v(15.57, -42.75) * mm, "end": v(15.59, -42.2) * mm});
            skLineSegment(sketch, "E30.124.0", {"start": v(17.71, -41.91) * mm, "end": v(17.33, -41.52) * mm});
            skLineSegment(sketch, "E30.124.1", {"start": v(17.33, -41.52) * mm, "end": v(17.04, -41.1) * mm});
            skLineSegment(sketch, "E30.124.2", {"start": v(16.7, -41.25) * mm, "end": v(17.04, -41.1) * mm});
            skLineSegment(sketch, "E30.124.3", {"start": v(16.7, -41.25) * mm, "end": v(16.79, -41.75) * mm});
            skLineSegment(sketch, "E30.124.4", {"start": v(16.79, -42.3) * mm, "end": v(16.79, -41.75) * mm});
            skLineSegment(sketch, "E30.125.0", {"start": v(18.9, -41.39) * mm, "end": v(18.5, -41) * mm});
            skLineSegment(sketch, "E30.125.1", {"start": v(18.5, -41) * mm, "end": v(18.21, -40.6) * mm});
            skLineSegment(sketch, "E30.125.2", {"start": v(17.87, -40.75) * mm, "end": v(18.21, -40.6) * mm});
            skLineSegment(sketch, "E30.125.3", {"start": v(17.87, -40.75) * mm, "end": v(17.97, -41.25) * mm});
            skLineSegment(sketch, "E30.125.4", {"start": v(17.99, -41.8) * mm, "end": v(17.97, -41.25) * mm});
            skLineSegment(sketch, "E30.126.0", {"start": v(20.08, -40.83) * mm, "end": v(19.67, -40.46) * mm});
            skLineSegment(sketch, "E30.126.1", {"start": v(19.67, -40.46) * mm, "end": v(19.36, -40.06) * mm});
            skLineSegment(sketch, "E30.126.2", {"start": v(19.02, -40.23) * mm, "end": v(19.36, -40.06) * mm});
            skLineSegment(sketch, "E30.126.3", {"start": v(19.02, -40.23) * mm, "end": v(19.14, -40.72) * mm});
            skLineSegment(sketch, "E30.126.4", {"start": v(19.17, -41.26) * mm, "end": v(19.14, -40.72) * mm});
            skLineSegment(sketch, "E30.127.0", {"start": v(21.23, -40.24) * mm, "end": v(20.82, -39.88) * mm});
            skLineSegment(sketch, "E30.127.1", {"start": v(20.82, -39.88) * mm, "end": v(20.5, -39.5) * mm});
            skLineSegment(sketch, "E30.127.2", {"start": v(20.16, -39.67) * mm, "end": v(20.5, -39.5) * mm});
            skLineSegment(sketch, "E30.127.3", {"start": v(20.16, -39.67) * mm, "end": v(20.3, -40.16) * mm});
            skLineSegment(sketch, "E30.127.4", {"start": v(20.34, -40.7) * mm, "end": v(20.3, -40.16) * mm});
            skLineSegment(sketch, "E30.128.0", {"start": v(22.37, -39.62) * mm, "end": v(21.95, -39.27) * mm});
            skLineSegment(sketch, "E30.128.1", {"start": v(21.95, -39.27) * mm, "end": v(21.62, -38.9) * mm});
            skLineSegment(sketch, "E30.128.2", {"start": v(21.29, -39.07) * mm, "end": v(21.62, -38.9) * mm});
            skLineSegment(sketch, "E30.128.3", {"start": v(21.29, -39.07) * mm, "end": v(21.44, -39.56) * mm});
            skLineSegment(sketch, "E30.128.4", {"start": v(21.5, -40.1) * mm, "end": v(21.44, -39.56) * mm});
            skLineSegment(sketch, "E30.129.0", {"start": v(23.5, -38.96) * mm, "end": v(23.06, -38.63) * mm});
            skLineSegment(sketch, "E30.129.1", {"start": v(23.06, -38.63) * mm, "end": v(22.72, -38.26) * mm});
            skLineSegment(sketch, "E30.129.2", {"start": v(22.4, -38.45) * mm, "end": v(22.72, -38.26) * mm});
            skLineSegment(sketch, "E30.129.3", {"start": v(22.4, -38.45) * mm, "end": v(22.56, -38.93) * mm});
            skLineSegment(sketch, "E30.129.4", {"start": v(22.63, -39.47) * mm, "end": v(22.56, -38.93) * mm});
            skLineSegment(sketch, "E30.130.0", {"start": v(24.6, -38.28) * mm, "end": v(24.15, -37.96) * mm});
            skLineSegment(sketch, "E30.130.1", {"start": v(24.15, -37.96) * mm, "end": v(23.8, -37.6) * mm});
            skLineSegment(sketch, "E30.130.2", {"start": v(23.48, -37.8) * mm, "end": v(23.8, -37.6) * mm});
            skLineSegment(sketch, "E30.130.3", {"start": v(23.48, -37.8) * mm, "end": v(23.66, -38.27) * mm});
            skLineSegment(sketch, "E30.130.4", {"start": v(23.75, -38.8) * mm, "end": v(23.66, -38.27) * mm});
            skLineSegment(sketch, "E30.131.0", {"start": v(25.68, -37.56) * mm, "end": v(25.23, -37.25) * mm});
            skLineSegment(sketch, "E30.131.1", {"start": v(25.23, -37.25) * mm, "end": v(24.87, -36.9) * mm});
            skLineSegment(sketch, "E30.131.2", {"start": v(24.55, -37.1) * mm, "end": v(24.87, -36.9) * mm});
            skLineSegment(sketch, "E30.131.3", {"start": v(24.55, -37.1) * mm, "end": v(24.74, -37.58) * mm});
            skLineSegment(sketch, "E30.131.4", {"start": v(24.85, -38.11) * mm, "end": v(24.74, -37.58) * mm});
            skLineSegment(sketch, "E30.132.0", {"start": v(26.74, -36.81) * mm, "end": v(26.28, -36.51) * mm});
            skLineSegment(sketch, "E30.132.1", {"start": v(26.28, -36.51) * mm, "end": v(25.91, -36.17) * mm});
            skLineSegment(sketch, "E30.132.2", {"start": v(25.6, -36.4) * mm, "end": v(25.91, -36.17) * mm});
            skLineSegment(sketch, "E30.132.3", {"start": v(25.6, -36.4) * mm, "end": v(25.8, -36.86) * mm});
            skLineSegment(sketch, "E30.132.4", {"start": v(25.93, -37.39) * mm, "end": v(25.8, -36.86) * mm});
            skLineSegment(sketch, "E30.133.0", {"start": v(27.78, -36.03) * mm, "end": v(27.31, -35.75) * mm});
            skLineSegment(sketch, "E30.133.1", {"start": v(27.31, -35.75) * mm, "end": v(26.93, -35.42) * mm});
            skLineSegment(sketch, "E30.133.2", {"start": v(26.63, -35.65) * mm, "end": v(26.93, -35.42) * mm});
            skLineSegment(sketch, "E30.133.3", {"start": v(26.63, -35.65) * mm, "end": v(26.85, -36.1) * mm});
            skLineSegment(sketch, "E30.133.4", {"start": v(26.99, -36.63) * mm, "end": v(26.85, -36.1) * mm});
            skLineSegment(sketch, "E30.134.0", {"start": v(28.8, -35.22) * mm, "end": v(28.32, -34.95) * mm});
            skLineSegment(sketch, "E30.134.1", {"start": v(28.32, -34.95) * mm, "end": v(27.93, -34.64) * mm});
            skLineSegment(sketch, "E30.134.2", {"start": v(27.64, -34.87) * mm, "end": v(27.93, -34.64) * mm});
            skLineSegment(sketch, "E30.134.3", {"start": v(27.64, -34.87) * mm, "end": v(27.87, -35.33) * mm});
            skLineSegment(sketch, "E30.134.4", {"start": v(28.02, -35.85) * mm, "end": v(27.87, -35.33) * mm});
            skLineSegment(sketch, "E30.135.0", {"start": v(29.8, -34.39) * mm, "end": v(29.31, -34.13) * mm});
            skLineSegment(sketch, "E30.135.1", {"start": v(29.31, -34.13) * mm, "end": v(28.91, -33.82) * mm});
            skLineSegment(sketch, "E30.135.2", {"start": v(28.62, -34.07) * mm, "end": v(28.91, -33.82) * mm});
            skLineSegment(sketch, "E30.135.3", {"start": v(28.62, -34.07) * mm, "end": v(28.87, -34.52) * mm});
            skLineSegment(sketch, "E30.135.4", {"start": v(29.03, -35.03) * mm, "end": v(28.87, -34.52) * mm});
            skLineSegment(sketch, "E30.136.0", {"start": v(30.77, -33.52) * mm, "end": v(30.27, -33.28) * mm});
            skLineSegment(sketch, "E30.136.1", {"start": v(30.27, -33.28) * mm, "end": v(29.87, -32.99) * mm});
            skLineSegment(sketch, "E30.136.2", {"start": v(29.59, -33.24) * mm, "end": v(29.87, -32.99) * mm});
            skLineSegment(sketch, "E30.136.3", {"start": v(29.59, -33.24) * mm, "end": v(29.84, -33.68) * mm});
            skLineSegment(sketch, "E30.136.4", {"start": v(30.02, -34.19) * mm, "end": v(29.84, -33.68) * mm});
            skLineSegment(sketch, "E30.137.0", {"start": v(31.71, -32.63) * mm, "end": v(31.21, -32.4) * mm});
            skLineSegment(sketch, "E30.137.1", {"start": v(31.21, -32.4) * mm, "end": v(30.8, -32.12) * mm});
            skLineSegment(sketch, "E30.137.2", {"start": v(30.52, -32.38) * mm, "end": v(30.8, -32.12) * mm});
            skLineSegment(sketch, "E30.137.3", {"start": v(30.52, -32.38) * mm, "end": v(30.79, -32.81) * mm});
            skLineSegment(sketch, "E30.137.4", {"start": v(30.99, -33.32) * mm, "end": v(30.79, -32.81) * mm});
            skLineSegment(sketch, "E30.138.0", {"start": v(32.63, -31.71) * mm, "end": v(32.12, -31.5) * mm});
            skLineSegment(sketch, "E30.138.1", {"start": v(32.12, -31.5) * mm, "end": v(31.7, -31.23) * mm});
            skLineSegment(sketch, "E30.138.2", {"start": v(31.43, -31.5) * mm, "end": v(31.7, -31.23) * mm});
            skLineSegment(sketch, "E30.138.3", {"start": v(31.43, -31.5) * mm, "end": v(31.71, -31.92) * mm});
            skLineSegment(sketch, "E30.138.4", {"start": v(31.92, -32.42) * mm, "end": v(31.71, -31.92) * mm});
            skLineSegment(sketch, "E30.139.0", {"start": v(33.52, -30.77) * mm, "end": v(33.01, -30.57) * mm});
            skLineSegment(sketch, "E30.139.1", {"start": v(33.01, -30.57) * mm, "end": v(32.58, -30.3) * mm});
            skLineSegment(sketch, "E30.139.2", {"start": v(32.32, -30.58) * mm, "end": v(32.58, -30.3) * mm});
            skLineSegment(sketch, "E30.139.3", {"start": v(32.32, -30.58) * mm, "end": v(32.61, -31) * mm});
            skLineSegment(sketch, "E30.139.4", {"start": v(32.84, -31.5) * mm, "end": v(32.61, -31) * mm});
            skLineSegment(sketch, "E30.140.0", {"start": v(34.39, -29.8) * mm, "end": v(33.87, -29.61) * mm});
            skLineSegment(sketch, "E30.140.1", {"start": v(33.87, -29.61) * mm, "end": v(33.43, -29.37) * mm});
            skLineSegment(sketch, "E30.140.2", {"start": v(33.18, -29.65) * mm, "end": v(33.43, -29.37) * mm});
            skLineSegment(sketch, "E30.140.3", {"start": v(33.18, -29.65) * mm, "end": v(33.48, -30.06) * mm});
            skLineSegment(sketch, "E30.140.4", {"start": v(33.72, -30.54) * mm, "end": v(33.48, -30.06) * mm});
            skLineSegment(sketch, "E30.141.0", {"start": v(35.22, -28.8) * mm, "end": v(34.7, -28.63) * mm});
            skLineSegment(sketch, "E30.141.1", {"start": v(34.7, -28.63) * mm, "end": v(34.26, -28.4) * mm});
            skLineSegment(sketch, "E30.141.2", {"start": v(34.01, -28.69) * mm, "end": v(34.26, -28.4) * mm});
            skLineSegment(sketch, "E30.141.3", {"start": v(34.01, -28.69) * mm, "end": v(34.33, -29.09) * mm});
            skLineSegment(sketch, "E30.141.4", {"start": v(34.58, -29.57) * mm, "end": v(34.33, -29.09) * mm});
            skLineSegment(sketch, "E30.142.0", {"start": v(36.03, -27.78) * mm, "end": v(35.5, -27.63) * mm});
            skLineSegment(sketch, "E30.142.1", {"start": v(35.5, -27.63) * mm, "end": v(35.05, -27.4) * mm});
            skLineSegment(sketch, "E30.142.2", {"start": v(34.82, -27.7) * mm, "end": v(35.05, -27.4) * mm});
            skLineSegment(sketch, "E30.142.3", {"start": v(34.82, -27.7) * mm, "end": v(35.15, -28.1) * mm});
            skLineSegment(sketch, "E30.142.4", {"start": v(35.41, -28.57) * mm, "end": v(35.15, -28.1) * mm});
            skLineSegment(sketch, "E30.143.0", {"start": v(36.81, -26.74) * mm, "end": v(36.28, -26.6) * mm});
            skLineSegment(sketch, "E30.143.1", {"start": v(36.28, -26.6) * mm, "end": v(35.82, -26.4) * mm});
            skLineSegment(sketch, "E30.143.2", {"start": v(35.6, -26.7) * mm, "end": v(35.82, -26.4) * mm});
            skLineSegment(sketch, "E30.143.3", {"start": v(35.6, -26.7) * mm, "end": v(35.93, -27.08) * mm});
            skLineSegment(sketch, "E30.143.4", {"start": v(36.21, -27.55) * mm, "end": v(35.93, -27.08) * mm});
            skLineSegment(sketch, "E30.144.0", {"start": v(37.56, -25.68) * mm, "end": v(37.02, -25.56) * mm});
            skLineSegment(sketch, "E30.144.1", {"start": v(37.02, -25.56) * mm, "end": v(36.56, -25.36) * mm});
            skLineSegment(sketch, "E30.144.2", {"start": v(36.34, -25.67) * mm, "end": v(36.56, -25.36) * mm});
            skLineSegment(sketch, "E30.144.3", {"start": v(36.34, -25.67) * mm, "end": v(36.7, -26.04) * mm});
            skLineSegment(sketch, "E30.144.4", {"start": v(36.99, -26.5) * mm, "end": v(36.7, -26.04) * mm});
            skLineSegment(sketch, "E30.145.0", {"start": v(38.28, -24.6) * mm, "end": v(37.74, -24.5) * mm});
            skLineSegment(sketch, "E30.145.1", {"start": v(37.74, -24.5) * mm, "end": v(37.27, -24.3) * mm});
            skLineSegment(sketch, "E30.145.2", {"start": v(37.06, -24.62) * mm, "end": v(37.27, -24.3) * mm});
            skLineSegment(sketch, "E30.145.3", {"start": v(37.06, -24.62) * mm, "end": v(37.42, -24.99) * mm});
            skLineSegment(sketch, "E30.145.4", {"start": v(37.73, -25.43) * mm, "end": v(37.42, -24.99) * mm});
            skLineSegment(sketch, "E30.146.0", {"start": v(38.96, -23.5) * mm, "end": v(38.42, -23.4) * mm});
            skLineSegment(sketch, "E30.146.1", {"start": v(38.42, -23.4) * mm, "end": v(37.95, -23.23) * mm});
            skLineSegment(sketch, "E30.146.2", {"start": v(37.75, -23.56) * mm, "end": v(37.95, -23.23) * mm});
            skLineSegment(sketch, "E30.146.3", {"start": v(37.75, -23.56) * mm, "end": v(38.12, -23.9) * mm});
            skLineSegment(sketch, "E30.146.4", {"start": v(38.44, -24.35) * mm, "end": v(38.12, -23.9) * mm});
            skLineSegment(sketch, "E30.147.0", {"start": v(39.62, -22.37) * mm, "end": v(39.08, -22.3) * mm});
            skLineSegment(sketch, "E30.147.1", {"start": v(39.08, -22.3) * mm, "end": v(38.6, -22.14) * mm});
            skLineSegment(sketch, "E30.147.2", {"start": v(38.4, -22.47) * mm, "end": v(38.6, -22.14) * mm});
            skLineSegment(sketch, "E30.147.3", {"start": v(38.4, -22.47) * mm, "end": v(38.79, -22.8) * mm});
            skLineSegment(sketch, "E30.147.4", {"start": v(39.12, -23.24) * mm, "end": v(38.79, -22.8) * mm});
            skLineSegment(sketch, "E30.148.0", {"start": v(40.24, -21.23) * mm, "end": v(39.7, -21.17) * mm});
            skLineSegment(sketch, "E30.148.1", {"start": v(39.7, -21.17) * mm, "end": v(39.21, -21.03) * mm});
            skLineSegment(sketch, "E30.148.2", {"start": v(39.03, -21.36) * mm, "end": v(39.21, -21.03) * mm});
            skLineSegment(sketch, "E30.148.3", {"start": v(39.03, -21.36) * mm, "end": v(39.42, -21.7) * mm});
            skLineSegment(sketch, "E30.148.4", {"start": v(39.77, -22.11) * mm, "end": v(39.42, -21.7) * mm});
            skLineSegment(sketch, "E30.149.0", {"start": v(40.83, -20.08) * mm, "end": v(40.28, -20.03) * mm});
            skLineSegment(sketch, "E30.149.1", {"start": v(40.28, -20.03) * mm, "end": v(39.8, -19.9) * mm});
            skLineSegment(sketch, "E30.149.2", {"start": v(39.63, -20.24) * mm, "end": v(39.8, -19.9) * mm});
            skLineSegment(sketch, "E30.149.3", {"start": v(39.63, -20.24) * mm, "end": v(40.03, -20.56) * mm});
            skLineSegment(sketch, "E30.149.4", {"start": v(40.38, -20.97) * mm, "end": v(40.03, -20.56) * mm});
            skLineSegment(sketch, "E30.150.0", {"start": v(41.39, -18.9) * mm, "end": v(40.84, -18.87) * mm});
            skLineSegment(sketch, "E30.150.1", {"start": v(40.84, -18.87) * mm, "end": v(40.35, -18.76) * mm});
            skLineSegment(sketch, "E30.150.2", {"start": v(40.2, -19.1) * mm, "end": v(40.35, -18.76) * mm});
            skLineSegment(sketch, "E30.150.3", {"start": v(40.2, -19.1) * mm, "end": v(40.6, -19.4) * mm});
            skLineSegment(sketch, "E30.150.4", {"start": v(40.96, -19.8) * mm, "end": v(40.6, -19.4) * mm});
            skLineSegment(sketch, "E30.151.0", {"start": v(41.91, -17.71) * mm, "end": v(41.36, -17.7) * mm});
            skLineSegment(sketch, "E30.151.1", {"start": v(41.36, -17.7) * mm, "end": v(40.87, -17.6) * mm});
            skLineSegment(sketch, "E30.151.2", {"start": v(40.72, -17.94) * mm, "end": v(40.87, -17.6) * mm});
            skLineSegment(sketch, "E30.151.3", {"start": v(40.72, -17.94) * mm, "end": v(41.13, -18.24) * mm});
            skLineSegment(sketch, "E30.151.4", {"start": v(41.51, -18.63) * mm, "end": v(41.13, -18.24) * mm});
            skLineSegment(sketch, "E30.152.0", {"start": v(42.4, -16.5) * mm, "end": v(41.85, -16.5) * mm});
            skLineSegment(sketch, "E30.152.1", {"start": v(41.85, -16.5) * mm, "end": v(41.36, -16.42) * mm});
            skLineSegment(sketch, "E30.152.2", {"start": v(41.21, -16.77) * mm, "end": v(41.36, -16.42) * mm});
            skLineSegment(sketch, "E30.152.3", {"start": v(41.21, -16.77) * mm, "end": v(41.64, -17.06) * mm});
            skLineSegment(sketch, "E30.152.4", {"start": v(42.03, -17.44) * mm, "end": v(41.64, -17.06) * mm});
            skLineSegment(sketch, "E30.153.0", {"start": v(42.85, -15.3) * mm, "end": v(42.3, -15.3) * mm});
            skLineSegment(sketch, "E30.153.1", {"start": v(42.3, -15.3) * mm, "end": v(41.8, -15.24) * mm});
            skLineSegment(sketch, "E30.153.2", {"start": v(41.68, -15.59) * mm, "end": v(41.8, -15.24) * mm});
            skLineSegment(sketch, "E30.153.3", {"start": v(41.68, -15.59) * mm, "end": v(42.1, -15.86) * mm});
            skLineSegment(sketch, "E30.153.4", {"start": v(42.5, -16.23) * mm, "end": v(42.1, -15.86) * mm});
            skLineSegment(sketch, "E30.154.0", {"start": v(43.27, -14.06) * mm, "end": v(42.73, -14.1) * mm});
            skLineSegment(sketch, "E30.154.1", {"start": v(42.73, -14.1) * mm, "end": v(42.23, -14.04) * mm});
            skLineSegment(sketch, "E30.154.2", {"start": v(42.1, -14.4) * mm, "end": v(42.23, -14.04) * mm});
            skLineSegment(sketch, "E30.154.3", {"start": v(42.1, -14.4) * mm, "end": v(42.54, -14.65) * mm});
            skLineSegment(sketch, "E30.154.4", {"start": v(42.95, -15) * mm, "end": v(42.54, -14.65) * mm});
            skLineSegment(sketch, "E30.155.0", {"start": v(43.66, -12.82) * mm, "end": v(43.11, -12.87) * mm});
            skLineSegment(sketch, "E30.155.1", {"start": v(43.11, -12.87) * mm, "end": v(42.6, -12.82) * mm});
            skLineSegment(sketch, "E30.155.2", {"start": v(42.5, -13.19) * mm, "end": v(42.6, -12.82) * mm});
            skLineSegment(sketch, "E30.155.3", {"start": v(42.5, -13.19) * mm, "end": v(42.94, -13.43) * mm});
            skLineSegment(sketch, "E30.155.4", {"start": v(43.36, -13.77) * mm, "end": v(42.94, -13.43) * mm});
            skLineSegment(sketch, "E30.156.0", {"start": v(44, -11.57) * mm, "end": v(43.46, -11.63) * mm});
            skLineSegment(sketch, "E30.156.1", {"start": v(43.46, -11.63) * mm, "end": v(42.96, -11.6) * mm});
            skLineSegment(sketch, "E30.156.2", {"start": v(42.86, -11.97) * mm, "end": v(42.96, -11.6) * mm});
            skLineSegment(sketch, "E30.156.3", {"start": v(42.86, -11.97) * mm, "end": v(43.31, -12.2) * mm});
            skLineSegment(sketch, "E30.156.4", {"start": v(43.74, -12.53) * mm, "end": v(43.31, -12.2) * mm});
            skLineSegment(sketch, "E30.157.0", {"start": v(44.32, -10.3) * mm, "end": v(43.77, -10.38) * mm});
            skLineSegment(sketch, "E30.157.1", {"start": v(43.77, -10.38) * mm, "end": v(43.27, -10.37) * mm});
            skLineSegment(sketch, "E30.157.2", {"start": v(43.18, -10.74) * mm, "end": v(43.27, -10.37) * mm});
            skLineSegment(sketch, "E30.157.3", {"start": v(43.18, -10.74) * mm, "end": v(43.64, -10.96) * mm});
            skLineSegment(sketch, "E30.157.4", {"start": v(44.08, -11.28) * mm, "end": v(43.64, -10.96) * mm});
            skLineSegment(sketch, "E30.158.0", {"start": v(44.6, -9.04) * mm, "end": v(44.05, -9.13) * mm});
            skLineSegment(sketch, "E30.158.1", {"start": v(44.05, -9.13) * mm, "end": v(43.55, -9.13) * mm});
            skLineSegment(sketch, "E30.158.2", {"start": v(43.47, -9.5) * mm, "end": v(43.55, -9.13) * mm});
            skLineSegment(sketch, "E30.158.3", {"start": v(43.47, -9.5) * mm, "end": v(43.94, -9.7) * mm});
            skLineSegment(sketch, "E30.158.4", {"start": v(44.38, -10.01) * mm, "end": v(43.94, -9.7) * mm});
            skLineSegment(sketch, "E30.159.0", {"start": v(44.83, -7.76) * mm, "end": v(44.3, -7.87) * mm});
            skLineSegment(sketch, "E30.159.1", {"start": v(44.3, -7.87) * mm, "end": v(43.8, -7.88) * mm});
            skLineSegment(sketch, "E30.159.2", {"start": v(43.73, -8.25) * mm, "end": v(43.8, -7.88) * mm});
            skLineSegment(sketch, "E30.159.3", {"start": v(43.73, -8.25) * mm, "end": v(44.2, -8.45) * mm});
            skLineSegment(sketch, "E30.159.4", {"start": v(44.65, -8.74) * mm, "end": v(44.2, -8.45) * mm});
            skLineSegment(sketch, "E30.160.0", {"start": v(45.04, -6.48) * mm, "end": v(44.5, -6.6) * mm});
            skLineSegment(sketch, "E30.160.1", {"start": v(44.5, -6.6) * mm, "end": v(44, -6.63) * mm});
            skLineSegment(sketch, "E30.160.2", {"start": v(43.94, -7) * mm, "end": v(44, -6.63) * mm});
            skLineSegment(sketch, "E30.160.3", {"start": v(43.94, -7) * mm, "end": v(44.42, -7.18) * mm});
            skLineSegment(sketch, "E30.160.4", {"start": v(44.88, -7.46) * mm, "end": v(44.42, -7.18) * mm});
            skLineSegment(sketch, "E30.161.0", {"start": v(45.2, -5.19) * mm, "end": v(44.67, -5.33) * mm});
            skLineSegment(sketch, "E30.161.1", {"start": v(44.67, -5.33) * mm, "end": v(44.17, -5.37) * mm});
            skLineSegment(sketch, "E30.161.2", {"start": v(44.13, -5.75) * mm, "end": v(44.17, -5.37) * mm});
            skLineSegment(sketch, "E30.161.3", {"start": v(44.13, -5.75) * mm, "end": v(44.6, -5.91) * mm});
            skLineSegment(sketch, "E30.161.4", {"start": v(45.08, -6.18) * mm, "end": v(44.6, -5.91) * mm});
            skLineSegment(sketch, "E30.162.0", {"start": v(45.33, -3.9) * mm, "end": v(44.8, -4.05) * mm});
            skLineSegment(sketch, "E30.162.1", {"start": v(44.8, -4.05) * mm, "end": v(44.3, -4.1) * mm});
            skLineSegment(sketch, "E30.162.2", {"start": v(44.27, -4.48) * mm, "end": v(44.3, -4.1) * mm});
            skLineSegment(sketch, "E30.162.3", {"start": v(44.27, -4.48) * mm, "end": v(44.76, -4.64) * mm});
            skLineSegment(sketch, "E30.162.4", {"start": v(45.24, -4.89) * mm, "end": v(44.76, -4.64) * mm});
            skLineSegment(sketch, "E30.163.0", {"start": v(45.43, -2.6) * mm, "end": v(44.9, -2.77) * mm});
            skLineSegment(sketch, "E30.163.1", {"start": v(44.9, -2.77) * mm, "end": v(44.4, -2.84) * mm});
            skLineSegment(sketch, "E30.163.2", {"start": v(44.38, -3.22) * mm, "end": v(44.4, -2.84) * mm});
            skLineSegment(sketch, "E30.163.3", {"start": v(44.38, -3.22) * mm, "end": v(44.87, -3.36) * mm});
            skLineSegment(sketch, "E30.163.4", {"start": v(45.36, -3.6) * mm, "end": v(44.87, -3.36) * mm});
            skLineSegment(sketch, "E30.164.0", {"start": v(45.48, -1.3) * mm, "end": v(44.96, -1.48) * mm});
            skLineSegment(sketch, "E30.164.1", {"start": v(44.96, -1.48) * mm, "end": v(44.47, -1.57) * mm});
            skLineSegment(sketch, "E30.164.2", {"start": v(44.45, -1.95) * mm, "end": v(44.47, -1.57) * mm});
            skLineSegment(sketch, "E30.164.3", {"start": v(44.45, -1.95) * mm, "end": v(44.95, -2.07) * mm});
            skLineSegment(sketch, "E30.164.4", {"start": v(45.44, -2.3) * mm, "end": v(44.95, -2.07) * mm});
            skLineSegment(sketch, "E30.165.0", {"start": v(45.5, 0) * mm, "end": v(44.99, -0.2) * mm});
            skLineSegment(sketch, "E30.165.1", {"start": v(44.99, -0.2) * mm, "end": v(44.5, -0.3) * mm});
            skLineSegment(sketch, "E30.165.2", {"start": v(44.5, -0.68) * mm, "end": v(44.5, -0.3) * mm});
            skLineSegment(sketch, "E30.165.3", {"start": v(44.5, -0.68) * mm, "end": v(44.99, -0.79) * mm});
            skLineSegment(sketch, "E30.165.4", {"start": v(45.49, -1) * mm, "end": v(44.99, -0.79) * mm});
            skLineSegment(sketch, "E30.166.0", {"start": v(45.48, 1.3) * mm, "end": v(44.98, 1.08) * mm});
            skLineSegment(sketch, "E30.166.1", {"start": v(44.98, 1.08) * mm, "end": v(44.49, 0.97) * mm});
            skLineSegment(sketch, "E30.166.2", {"start": v(44.5, 0.6) * mm, "end": v(44.49, 0.97) * mm});
            skLineSegment(sketch, "E30.166.3", {"start": v(44.5, 0.6) * mm, "end": v(45, 0.5) * mm});
            skLineSegment(sketch, "E30.166.4", {"start": v(45.5, 0.3) * mm, "end": v(45, 0.5) * mm});
            skLineSegment(sketch, "E30.167.0", {"start": v(45.43, 2.6) * mm, "end": v(44.93, 2.37) * mm});
            skLineSegment(sketch, "E30.167.1", {"start": v(44.93, 2.37) * mm, "end": v(44.44, 2.24) * mm});
            skLineSegment(sketch, "E30.167.2", {"start": v(44.46, 1.86) * mm, "end": v(44.44, 2.24) * mm});
            skLineSegment(sketch, "E30.167.3", {"start": v(44.46, 1.86) * mm, "end": v(44.96, 1.78) * mm});
            skLineSegment(sketch, "E30.167.4", {"start": v(45.47, 1.6) * mm, "end": v(44.96, 1.78) * mm});
            skLineSegment(sketch, "E30.168.0", {"start": v(45.33, 3.9) * mm, "end": v(44.84, 3.65) * mm});
            skLineSegment(sketch, "E30.168.1", {"start": v(44.84, 3.65) * mm, "end": v(44.36, 3.5) * mm});
            skLineSegment(sketch, "E30.168.2", {"start": v(44.39, 3.13) * mm, "end": v(44.36, 3.5) * mm});
            skLineSegment(sketch, "E30.168.3", {"start": v(44.39, 3.13) * mm, "end": v(44.9, 3.06) * mm});
            skLineSegment(sketch, "E30.168.4", {"start": v(45.4, 2.9) * mm, "end": v(44.9, 3.06) * mm});
            skLineSegment(sketch, "E30.169.0", {"start": v(45.2, 5.19) * mm, "end": v(44.72, 4.93) * mm});
            skLineSegment(sketch, "E30.169.1", {"start": v(44.72, 4.93) * mm, "end": v(44.24, 4.77) * mm});
            skLineSegment(sketch, "E30.169.2", {"start": v(44.28, 4.4) * mm, "end": v(44.24, 4.77) * mm});
            skLineSegment(sketch, "E30.169.3", {"start": v(44.28, 4.4) * mm, "end": v(44.79, 4.34) * mm});
            skLineSegment(sketch, "E30.169.4", {"start": v(45.3, 4.2) * mm, "end": v(44.79, 4.34) * mm});
            skLineSegment(sketch, "E30.170.0", {"start": v(45.04, 6.48) * mm, "end": v(44.56, 6.2) * mm});
            skLineSegment(sketch, "E30.170.1", {"start": v(44.56, 6.2) * mm, "end": v(44.09, 6.04) * mm});
            skLineSegment(sketch, "E30.170.2", {"start": v(44.14, 5.66) * mm, "end": v(44.09, 6.04) * mm});
            skLineSegment(sketch, "E30.170.3", {"start": v(44.14, 5.66) * mm, "end": v(44.64, 5.62) * mm});
            skLineSegment(sketch, "E30.170.4", {"start": v(45.17, 5.48) * mm, "end": v(44.64, 5.62) * mm});
            skLineSegment(sketch, "E30.171.0", {"start": v(44.83, 7.76) * mm, "end": v(44.36, 7.47) * mm});
            skLineSegment(sketch, "E30.171.1", {"start": v(44.36, 7.47) * mm, "end": v(43.9, 7.3) * mm});
            skLineSegment(sketch, "E30.171.2", {"start": v(43.96, 6.92) * mm, "end": v(43.9, 7.3) * mm});
            skLineSegment(sketch, "E30.171.3", {"start": v(43.96, 6.92) * mm, "end": v(44.46, 6.9) * mm});
            skLineSegment(sketch, "E30.171.4", {"start": v(45, 6.77) * mm, "end": v(44.46, 6.9) * mm});
            skLineSegment(sketch, "E30.172.0", {"start": v(44.6, 9.04) * mm, "end": v(44.13, 8.74) * mm});
            skLineSegment(sketch, "E30.172.1", {"start": v(44.13, 8.74) * mm, "end": v(43.67, 8.54) * mm});
            skLineSegment(sketch, "E30.172.2", {"start": v(43.74, 8.17) * mm, "end": v(43.67, 8.54) * mm});
            skLineSegment(sketch, "E30.172.3", {"start": v(43.74, 8.17) * mm, "end": v(44.25, 8.16) * mm});
            skLineSegment(sketch, "E30.172.4", {"start": v(44.78, 8.05) * mm, "end": v(44.25, 8.16) * mm});
            skLineSegment(sketch, "E30.173.0", {"start": v(44.32, 10.3) * mm, "end": v(43.87, 10) * mm});
            skLineSegment(sketch, "E30.173.1", {"start": v(43.87, 10) * mm, "end": v(43.4, 9.79) * mm});
            skLineSegment(sketch, "E30.173.2", {"start": v(43.49, 9.42) * mm, "end": v(43.4, 9.79) * mm});
            skLineSegment(sketch, "E30.173.3", {"start": v(43.49, 9.42) * mm, "end": v(44, 9.42) * mm});
            skLineSegment(sketch, "E30.173.4", {"start": v(44.53, 9.33) * mm, "end": v(44, 9.42) * mm});
            skLineSegment(sketch, "E30.174.0", {"start": v(44, 11.57) * mm, "end": v(43.56, 11.24) * mm});
            skLineSegment(sketch, "E30.174.1", {"start": v(43.56, 11.24) * mm, "end": v(43.11, 11.02) * mm});
            skLineSegment(sketch, "E30.174.2", {"start": v(43.2, 10.66) * mm, "end": v(43.11, 11.02) * mm});
            skLineSegment(sketch, "E30.174.3", {"start": v(43.2, 10.66) * mm, "end": v(43.71, 10.67) * mm});
            skLineSegment(sketch, "E30.174.4", {"start": v(44.25, 10.6) * mm, "end": v(43.71, 10.67) * mm});
            skLineSegment(sketch, "E30.175.0", {"start": v(43.66, 12.82) * mm, "end": v(43.22, 12.48) * mm});
            skLineSegment(sketch, "E30.175.1", {"start": v(43.22, 12.48) * mm, "end": v(42.78, 12.25) * mm});
            skLineSegment(sketch, "E30.175.2", {"start": v(42.88, 11.88) * mm, "end": v(42.78, 12.25) * mm});
            skLineSegment(sketch, "E30.175.3", {"start": v(42.88, 11.88) * mm, "end": v(43.39, 11.92) * mm});
            skLineSegment(sketch, "E30.175.4", {"start": v(43.93, 11.86) * mm, "end": v(43.39, 11.92) * mm});
            skLineSegment(sketch, "E30.176.0", {"start": v(43.27, 14.06) * mm, "end": v(42.85, 13.71) * mm});
            skLineSegment(sketch, "E30.176.1", {"start": v(42.85, 13.71) * mm, "end": v(42.41, 13.46) * mm});
            skLineSegment(sketch, "E30.176.2", {"start": v(42.52, 13.1) * mm, "end": v(42.41, 13.46) * mm});
            skLineSegment(sketch, "E30.176.3", {"start": v(42.52, 13.1) * mm, "end": v(43.03, 13.15) * mm});
            skLineSegment(sketch, "E30.176.4", {"start": v(43.57, 13.1) * mm, "end": v(43.03, 13.15) * mm});
            skLineSegment(sketch, "E30.177.0", {"start": v(42.85, 15.3) * mm, "end": v(42.44, 14.93) * mm});
            skLineSegment(sketch, "E30.177.1", {"start": v(42.44, 14.93) * mm, "end": v(42, 14.67) * mm});
            skLineSegment(sketch, "E30.177.2", {"start": v(42.13, 14.31) * mm, "end": v(42, 14.67) * mm});
            skLineSegment(sketch, "E30.177.3", {"start": v(42.13, 14.31) * mm, "end": v(42.64, 14.38) * mm});
            skLineSegment(sketch, "E30.177.4", {"start": v(43.18, 14.34) * mm, "end": v(42.64, 14.38) * mm});
            skLineSegment(sketch, "E30.178.0", {"start": v(42.4, 16.5) * mm, "end": v(42, 16.14) * mm});
            skLineSegment(sketch, "E30.178.1", {"start": v(42, 16.14) * mm, "end": v(41.57, 15.86) * mm});
            skLineSegment(sketch, "E30.178.2", {"start": v(41.7, 15.51) * mm, "end": v(41.57, 15.86) * mm});
            skLineSegment(sketch, "E30.178.3", {"start": v(41.7, 15.51) * mm, "end": v(42.2, 15.59) * mm});
            skLineSegment(sketch, "E30.178.4", {"start": v(42.75, 15.57) * mm, "end": v(42.2, 15.59) * mm});
            skLineSegment(sketch, "E30.179.0", {"start": v(41.91, 17.71) * mm, "end": v(41.52, 17.33) * mm});
            skLineSegment(sketch, "E30.179.1", {"start": v(41.52, 17.33) * mm, "end": v(41.1, 17.04) * mm});
            skLineSegment(sketch, "E30.179.2", {"start": v(41.25, 16.7) * mm, "end": v(41.1, 17.04) * mm});
            skLineSegment(sketch, "E30.179.3", {"start": v(41.25, 16.7) * mm, "end": v(41.75, 16.79) * mm});
            skLineSegment(sketch, "E30.179.4", {"start": v(42.3, 16.79) * mm, "end": v(41.75, 16.79) * mm});
            skLineSegment(sketch, "E30.180.0", {"start": v(41.39, 18.9) * mm, "end": v(41, 18.5) * mm});
            skLineSegment(sketch, "E30.180.1", {"start": v(41, 18.5) * mm, "end": v(40.6, 18.21) * mm});
            skLineSegment(sketch, "E30.180.2", {"start": v(40.75, 17.87) * mm, "end": v(40.6, 18.21) * mm});
            skLineSegment(sketch, "E30.180.3", {"start": v(40.75, 17.87) * mm, "end": v(41.25, 17.97) * mm});
            skLineSegment(sketch, "E30.180.4", {"start": v(41.8, 17.99) * mm, "end": v(41.25, 17.97) * mm});
            skLineSegment(sketch, "E30.181.0", {"start": v(40.83, 20.08) * mm, "end": v(40.46, 19.67) * mm});
            skLineSegment(sketch, "E30.181.1", {"start": v(40.46, 19.67) * mm, "end": v(40.06, 19.36) * mm});
            skLineSegment(sketch, "E30.181.2", {"start": v(40.23, 19.02) * mm, "end": v(40.06, 19.36) * mm});
            skLineSegment(sketch, "E30.181.3", {"start": v(40.23, 19.02) * mm, "end": v(40.72, 19.14) * mm});
            skLineSegment(sketch, "E30.181.4", {"start": v(41.26, 19.17) * mm, "end": v(40.72, 19.14) * mm});
            skLineSegment(sketch, "E30.182.0", {"start": v(40.24, 21.23) * mm, "end": v(39.88, 20.82) * mm});
            skLineSegment(sketch, "E30.182.1", {"start": v(39.88, 20.82) * mm, "end": v(39.5, 20.5) * mm});
            skLineSegment(sketch, "E30.182.2", {"start": v(39.67, 20.16) * mm, "end": v(39.5, 20.5) * mm});
            skLineSegment(sketch, "E30.182.3", {"start": v(39.67, 20.16) * mm, "end": v(40.16, 20.3) * mm});
            skLineSegment(sketch, "E30.182.4", {"start": v(40.7, 20.34) * mm, "end": v(40.16, 20.3) * mm});
            skLineSegment(sketch, "E30.183.0", {"start": v(39.62, 22.37) * mm, "end": v(39.27, 21.95) * mm});
            skLineSegment(sketch, "E30.183.1", {"start": v(39.27, 21.95) * mm, "end": v(38.9, 21.62) * mm});
            skLineSegment(sketch, "E30.183.2", {"start": v(39.07, 21.29) * mm, "end": v(38.9, 21.62) * mm});
            skLineSegment(sketch, "E30.183.3", {"start": v(39.07, 21.29) * mm, "end": v(39.56, 21.44) * mm});
            skLineSegment(sketch, "E30.183.4", {"start": v(40.1, 21.5) * mm, "end": v(39.56, 21.44) * mm});
            skLineSegment(sketch, "E30.184.0", {"start": v(38.96, 23.5) * mm, "end": v(38.63, 23.06) * mm});
            skLineSegment(sketch, "E30.184.1", {"start": v(38.63, 23.06) * mm, "end": v(38.26, 22.72) * mm});
            skLineSegment(sketch, "E30.184.2", {"start": v(38.45, 22.4) * mm, "end": v(38.26, 22.72) * mm});
            skLineSegment(sketch, "E30.184.3", {"start": v(38.45, 22.4) * mm, "end": v(38.93, 22.56) * mm});
            skLineSegment(sketch, "E30.184.4", {"start": v(39.47, 22.63) * mm, "end": v(38.93, 22.56) * mm});
            skLineSegment(sketch, "E30.185.0", {"start": v(38.28, 24.6) * mm, "end": v(37.96, 24.15) * mm});
            skLineSegment(sketch, "E30.185.1", {"start": v(37.96, 24.15) * mm, "end": v(37.6, 23.8) * mm});
            skLineSegment(sketch, "E30.185.2", {"start": v(37.8, 23.48) * mm, "end": v(37.6, 23.8) * mm});
            skLineSegment(sketch, "E30.185.3", {"start": v(37.8, 23.48) * mm, "end": v(38.27, 23.66) * mm});
            skLineSegment(sketch, "E30.185.4", {"start": v(38.8, 23.75) * mm, "end": v(38.27, 23.66) * mm});
            skLineSegment(sketch, "E30.186.0", {"start": v(37.56, 25.68) * mm, "end": v(37.25, 25.23) * mm});
            skLineSegment(sketch, "E30.186.1", {"start": v(37.25, 25.23) * mm, "end": v(36.9, 24.87) * mm});
            skLineSegment(sketch, "E30.186.2", {"start": v(37.1, 24.55) * mm, "end": v(36.9, 24.87) * mm});
            skLineSegment(sketch, "E30.186.3", {"start": v(37.1, 24.55) * mm, "end": v(37.58, 24.74) * mm});
            skLineSegment(sketch, "E30.186.4", {"start": v(38.11, 24.85) * mm, "end": v(37.58, 24.74) * mm});
            skLineSegment(sketch, "E30.187.0", {"start": v(36.81, 26.74) * mm, "end": v(36.51, 26.28) * mm});
            skLineSegment(sketch, "E30.187.1", {"start": v(36.51, 26.28) * mm, "end": v(36.17, 25.91) * mm});
            skLineSegment(sketch, "E30.187.2", {"start": v(36.4, 25.6) * mm, "end": v(36.17, 25.91) * mm});
            skLineSegment(sketch, "E30.187.3", {"start": v(36.4, 25.6) * mm, "end": v(36.86, 25.8) * mm});
            skLineSegment(sketch, "E30.187.4", {"start": v(37.39, 25.93) * mm, "end": v(36.86, 25.8) * mm});
            skLineSegment(sketch, "E30.188.0", {"start": v(36.03, 27.78) * mm, "end": v(35.75, 27.31) * mm});
            skLineSegment(sketch, "E30.188.1", {"start": v(35.75, 27.31) * mm, "end": v(35.42, 26.93) * mm});
            skLineSegment(sketch, "E30.188.2", {"start": v(35.65, 26.63) * mm, "end": v(35.42, 26.93) * mm});
            skLineSegment(sketch, "E30.188.3", {"start": v(35.65, 26.63) * mm, "end": v(36.1, 26.85) * mm});
            skLineSegment(sketch, "E30.188.4", {"start": v(36.63, 26.99) * mm, "end": v(36.1, 26.85) * mm});
            skLineSegment(sketch, "E30.189.0", {"start": v(35.22, 28.8) * mm, "end": v(34.95, 28.32) * mm});
            skLineSegment(sketch, "E30.189.1", {"start": v(34.95, 28.32) * mm, "end": v(34.64, 27.93) * mm});
            skLineSegment(sketch, "E30.189.2", {"start": v(34.87, 27.64) * mm, "end": v(34.64, 27.93) * mm});
            skLineSegment(sketch, "E30.189.3", {"start": v(34.87, 27.64) * mm, "end": v(35.33, 27.87) * mm});
            skLineSegment(sketch, "E30.189.4", {"start": v(35.85, 28.02) * mm, "end": v(35.33, 27.87) * mm});
            skLineSegment(sketch, "E30.190.0", {"start": v(34.39, 29.8) * mm, "end": v(34.13, 29.31) * mm});
            skLineSegment(sketch, "E30.190.1", {"start": v(34.13, 29.31) * mm, "end": v(33.82, 28.91) * mm});
            skLineSegment(sketch, "E30.190.2", {"start": v(34.07, 28.62) * mm, "end": v(33.82, 28.91) * mm});
            skLineSegment(sketch, "E30.190.3", {"start": v(34.07, 28.62) * mm, "end": v(34.52, 28.87) * mm});
            skLineSegment(sketch, "E30.190.4", {"start": v(35.03, 29.03) * mm, "end": v(34.52, 28.87) * mm});
            skLineSegment(sketch, "E30.191.0", {"start": v(33.52, 30.77) * mm, "end": v(33.28, 30.27) * mm});
            skLineSegment(sketch, "E30.191.1", {"start": v(33.28, 30.27) * mm, "end": v(32.99, 29.87) * mm});
            skLineSegment(sketch, "E30.191.2", {"start": v(33.24, 29.59) * mm, "end": v(32.99, 29.87) * mm});
            skLineSegment(sketch, "E30.191.3", {"start": v(33.24, 29.59) * mm, "end": v(33.68, 29.84) * mm});
            skLineSegment(sketch, "E30.191.4", {"start": v(34.19, 30.02) * mm, "end": v(33.68, 29.84) * mm});
            skLineSegment(sketch, "E30.192.0", {"start": v(32.63, 31.71) * mm, "end": v(32.4, 31.21) * mm});
            skLineSegment(sketch, "E30.192.1", {"start": v(32.4, 31.21) * mm, "end": v(32.12, 30.8) * mm});
            skLineSegment(sketch, "E30.192.2", {"start": v(32.38, 30.52) * mm, "end": v(32.12, 30.8) * mm});
            skLineSegment(sketch, "E30.192.3", {"start": v(32.38, 30.52) * mm, "end": v(32.81, 30.79) * mm});
            skLineSegment(sketch, "E30.192.4", {"start": v(33.32, 30.99) * mm, "end": v(32.81, 30.79) * mm});
            skLineSegment(sketch, "E30.193.0", {"start": v(31.71, 32.63) * mm, "end": v(31.5, 32.12) * mm});
            skLineSegment(sketch, "E30.193.1", {"start": v(31.5, 32.12) * mm, "end": v(31.23, 31.7) * mm});
            skLineSegment(sketch, "E30.193.2", {"start": v(31.5, 31.43) * mm, "end": v(31.23, 31.7) * mm});
            skLineSegment(sketch, "E30.193.3", {"start": v(31.5, 31.43) * mm, "end": v(31.92, 31.71) * mm});
            skLineSegment(sketch, "E30.193.4", {"start": v(32.42, 31.92) * mm, "end": v(31.92, 31.71) * mm});
            skLineSegment(sketch, "E30.194.0", {"start": v(30.77, 33.52) * mm, "end": v(30.57, 33.01) * mm});
            skLineSegment(sketch, "E30.194.1", {"start": v(30.57, 33.01) * mm, "end": v(30.3, 32.58) * mm});
            skLineSegment(sketch, "E30.194.2", {"start": v(30.58, 32.32) * mm, "end": v(30.3, 32.58) * mm});
            skLineSegment(sketch, "E30.194.3", {"start": v(30.58, 32.32) * mm, "end": v(31, 32.61) * mm});
            skLineSegment(sketch, "E30.194.4", {"start": v(31.5, 32.84) * mm, "end": v(31, 32.61) * mm});
            skLineSegment(sketch, "E30.195.0", {"start": v(29.8, 34.39) * mm, "end": v(29.61, 33.87) * mm});
            skLineSegment(sketch, "E30.195.1", {"start": v(29.61, 33.87) * mm, "end": v(29.37, 33.43) * mm});
            skLineSegment(sketch, "E30.195.2", {"start": v(29.65, 33.18) * mm, "end": v(29.37, 33.43) * mm});
            skLineSegment(sketch, "E30.195.3", {"start": v(29.65, 33.18) * mm, "end": v(30.06, 33.48) * mm});
            skLineSegment(sketch, "E30.195.4", {"start": v(30.54, 33.72) * mm, "end": v(30.06, 33.48) * mm});
            skLineSegment(sketch, "E30.196.0", {"start": v(28.8, 35.22) * mm, "end": v(28.63, 34.7) * mm});
            skLineSegment(sketch, "E30.196.1", {"start": v(28.63, 34.7) * mm, "end": v(28.4, 34.26) * mm});
            skLineSegment(sketch, "E30.196.2", {"start": v(28.69, 34.01) * mm, "end": v(28.4, 34.26) * mm});
            skLineSegment(sketch, "E30.196.3", {"start": v(28.69, 34.01) * mm, "end": v(29.09, 34.33) * mm});
            skLineSegment(sketch, "E30.196.4", {"start": v(29.57, 34.58) * mm, "end": v(29.09, 34.33) * mm});
            skLineSegment(sketch, "E30.197.0", {"start": v(27.78, 36.03) * mm, "end": v(27.63, 35.5) * mm});
            skLineSegment(sketch, "E30.197.1", {"start": v(27.63, 35.5) * mm, "end": v(27.4, 35.05) * mm});
            skLineSegment(sketch, "E30.197.2", {"start": v(27.7, 34.82) * mm, "end": v(27.4, 35.05) * mm});
            skLineSegment(sketch, "E30.197.3", {"start": v(27.7, 34.82) * mm, "end": v(28.1, 35.15) * mm});
            skLineSegment(sketch, "E30.197.4", {"start": v(28.57, 35.41) * mm, "end": v(28.1, 35.15) * mm});
            skLineSegment(sketch, "E30.198.0", {"start": v(26.74, 36.81) * mm, "end": v(26.6, 36.28) * mm});
            skLineSegment(sketch, "E30.198.1", {"start": v(26.6, 36.28) * mm, "end": v(26.4, 35.82) * mm});
            skLineSegment(sketch, "E30.198.2", {"start": v(26.7, 35.6) * mm, "end": v(26.4, 35.82) * mm});
            skLineSegment(sketch, "E30.198.3", {"start": v(26.7, 35.6) * mm, "end": v(27.08, 35.93) * mm});
            skLineSegment(sketch, "E30.198.4", {"start": v(27.55, 36.21) * mm, "end": v(27.08, 35.93) * mm});
            skLineSegment(sketch, "E30.199.0", {"start": v(25.68, 37.56) * mm, "end": v(25.56, 37.02) * mm});
            skLineSegment(sketch, "E30.199.1", {"start": v(25.56, 37.02) * mm, "end": v(25.36, 36.56) * mm});
            skLineSegment(sketch, "E30.199.2", {"start": v(25.67, 36.34) * mm, "end": v(25.36, 36.56) * mm});
            skLineSegment(sketch, "E30.199.3", {"start": v(25.67, 36.34) * mm, "end": v(26.04, 36.7) * mm});
            skLineSegment(sketch, "E30.199.4", {"start": v(26.5, 36.99) * mm, "end": v(26.04, 36.7) * mm});
            skLineSegment(sketch, "E30.200.0", {"start": v(24.6, 38.28) * mm, "end": v(24.5, 37.74) * mm});
            skLineSegment(sketch, "E30.200.1", {"start": v(24.5, 37.74) * mm, "end": v(24.3, 37.27) * mm});
            skLineSegment(sketch, "E30.200.2", {"start": v(24.62, 37.06) * mm, "end": v(24.3, 37.27) * mm});
            skLineSegment(sketch, "E30.200.3", {"start": v(24.62, 37.06) * mm, "end": v(24.99, 37.42) * mm});
            skLineSegment(sketch, "E30.200.4", {"start": v(25.43, 37.73) * mm, "end": v(24.99, 37.42) * mm});
            skLineSegment(sketch, "E30.201.0", {"start": v(23.5, 38.96) * mm, "end": v(23.4, 38.42) * mm});
            skLineSegment(sketch, "E30.201.1", {"start": v(23.4, 38.42) * mm, "end": v(23.23, 37.95) * mm});
            skLineSegment(sketch, "E30.201.2", {"start": v(23.56, 37.75) * mm, "end": v(23.23, 37.95) * mm});
            skLineSegment(sketch, "E30.201.3", {"start": v(23.56, 37.75) * mm, "end": v(23.9, 38.12) * mm});
            skLineSegment(sketch, "E30.201.4", {"start": v(24.35, 38.44) * mm, "end": v(23.9, 38.12) * mm});
            skLineSegment(sketch, "E30.202.0", {"start": v(22.37, 39.62) * mm, "end": v(22.3, 39.08) * mm});
            skLineSegment(sketch, "E30.202.1", {"start": v(22.3, 39.08) * mm, "end": v(22.14, 38.6) * mm});
            skLineSegment(sketch, "E30.202.2", {"start": v(22.47, 38.4) * mm, "end": v(22.14, 38.6) * mm});
            skLineSegment(sketch, "E30.202.3", {"start": v(22.47, 38.4) * mm, "end": v(22.8, 38.79) * mm});
            skLineSegment(sketch, "E30.202.4", {"start": v(23.24, 39.12) * mm, "end": v(22.8, 38.79) * mm});
            skLineSegment(sketch, "E30.203.0", {"start": v(21.23, 40.24) * mm, "end": v(21.17, 39.7) * mm});
            skLineSegment(sketch, "E30.203.1", {"start": v(21.17, 39.7) * mm, "end": v(21.03, 39.21) * mm});
            skLineSegment(sketch, "E30.203.2", {"start": v(21.36, 39.03) * mm, "end": v(21.03, 39.21) * mm});
            skLineSegment(sketch, "E30.203.3", {"start": v(21.36, 39.03) * mm, "end": v(21.7, 39.42) * mm});
            skLineSegment(sketch, "E30.203.4", {"start": v(22.11, 39.77) * mm, "end": v(21.7, 39.42) * mm});
            skLineSegment(sketch, "E30.204.0", {"start": v(20.08, 40.83) * mm, "end": v(20.03, 40.28) * mm});
            skLineSegment(sketch, "E30.204.1", {"start": v(20.03, 40.28) * mm, "end": v(19.9, 39.8) * mm});
            skLineSegment(sketch, "E30.204.2", {"start": v(20.24, 39.63) * mm, "end": v(19.9, 39.8) * mm});
            skLineSegment(sketch, "E30.204.3", {"start": v(20.24, 39.63) * mm, "end": v(20.56, 40.03) * mm});
            skLineSegment(sketch, "E30.204.4", {"start": v(20.97, 40.38) * mm, "end": v(20.56, 40.03) * mm});
            skLineSegment(sketch, "E30.205.0", {"start": v(18.9, 41.39) * mm, "end": v(18.87, 40.84) * mm});
            skLineSegment(sketch, "E30.205.1", {"start": v(18.87, 40.84) * mm, "end": v(18.76, 40.35) * mm});
            skLineSegment(sketch, "E30.205.2", {"start": v(19.1, 40.2) * mm, "end": v(18.76, 40.35) * mm});
            skLineSegment(sketch, "E30.205.3", {"start": v(19.1, 40.2) * mm, "end": v(19.4, 40.6) * mm});
            skLineSegment(sketch, "E30.205.4", {"start": v(19.8, 40.96) * mm, "end": v(19.4, 40.6) * mm});
            skLineSegment(sketch, "E30.206.0", {"start": v(17.71, 41.91) * mm, "end": v(17.7, 41.36) * mm});
            skLineSegment(sketch, "E30.206.1", {"start": v(17.7, 41.36) * mm, "end": v(17.6, 40.87) * mm});
            skLineSegment(sketch, "E30.206.2", {"start": v(17.94, 40.72) * mm, "end": v(17.6, 40.87) * mm});
            skLineSegment(sketch, "E30.206.3", {"start": v(17.94, 40.72) * mm, "end": v(18.24, 41.13) * mm});
            skLineSegment(sketch, "E30.206.4", {"start": v(18.63, 41.51) * mm, "end": v(18.24, 41.13) * mm});
            skLineSegment(sketch, "E30.207.0", {"start": v(16.5, 42.4) * mm, "end": v(16.5, 41.85) * mm});
            skLineSegment(sketch, "E30.207.1", {"start": v(16.5, 41.85) * mm, "end": v(16.42, 41.36) * mm});
            skLineSegment(sketch, "E30.207.2", {"start": v(16.77, 41.21) * mm, "end": v(16.42, 41.36) * mm});
            skLineSegment(sketch, "E30.207.3", {"start": v(16.77, 41.21) * mm, "end": v(17.06, 41.64) * mm});
            skLineSegment(sketch, "E30.207.4", {"start": v(17.44, 42.03) * mm, "end": v(17.06, 41.64) * mm});
            skLineSegment(sketch, "E30.208.0", {"start": v(15.3, 42.85) * mm, "end": v(15.3, 42.3) * mm});
            skLineSegment(sketch, "E30.208.1", {"start": v(15.3, 42.3) * mm, "end": v(15.24, 41.8) * mm});
            skLineSegment(sketch, "E30.208.2", {"start": v(15.59, 41.68) * mm, "end": v(15.24, 41.8) * mm});
            skLineSegment(sketch, "E30.208.3", {"start": v(15.59, 41.68) * mm, "end": v(15.86, 42.1) * mm});
            skLineSegment(sketch, "E30.208.4", {"start": v(16.23, 42.5) * mm, "end": v(15.86, 42.1) * mm});
            skLineSegment(sketch, "E30.209.0", {"start": v(14.06, 43.27) * mm, "end": v(14.1, 42.73) * mm});
            skLineSegment(sketch, "E30.209.1", {"start": v(14.1, 42.73) * mm, "end": v(14.04, 42.23) * mm});
            skLineSegment(sketch, "E30.209.2", {"start": v(14.4, 42.1) * mm, "end": v(14.04, 42.23) * mm});
            skLineSegment(sketch, "E30.209.3", {"start": v(14.4, 42.1) * mm, "end": v(14.65, 42.54) * mm});
            skLineSegment(sketch, "E30.209.4", {"start": v(15, 42.95) * mm, "end": v(14.65, 42.54) * mm});
            skLineSegment(sketch, "E30.210.0", {"start": v(12.82, 43.66) * mm, "end": v(12.87, 43.11) * mm});
            skLineSegment(sketch, "E30.210.1", {"start": v(12.87, 43.11) * mm, "end": v(12.82, 42.6) * mm});
            skLineSegment(sketch, "E30.210.2", {"start": v(13.19, 42.5) * mm, "end": v(12.82, 42.6) * mm});
            skLineSegment(sketch, "E30.210.3", {"start": v(13.19, 42.5) * mm, "end": v(13.43, 42.94) * mm});
            skLineSegment(sketch, "E30.210.4", {"start": v(13.77, 43.36) * mm, "end": v(13.43, 42.94) * mm});
            skLineSegment(sketch, "E30.211.0", {"start": v(11.57, 44) * mm, "end": v(11.63, 43.46) * mm});
            skLineSegment(sketch, "E30.211.1", {"start": v(11.63, 43.46) * mm, "end": v(11.6, 42.96) * mm});
            skLineSegment(sketch, "E30.211.2", {"start": v(11.97, 42.86) * mm, "end": v(11.6, 42.96) * mm});
            skLineSegment(sketch, "E30.211.3", {"start": v(11.97, 42.86) * mm, "end": v(12.2, 43.31) * mm});
            skLineSegment(sketch, "E30.211.4", {"start": v(12.53, 43.74) * mm, "end": v(12.2, 43.31) * mm});
            skLineSegment(sketch, "E30.212.0", {"start": v(10.3, 44.32) * mm, "end": v(10.38, 43.77) * mm});
            skLineSegment(sketch, "E30.212.1", {"start": v(10.38, 43.77) * mm, "end": v(10.37, 43.27) * mm});
            skLineSegment(sketch, "E30.212.2", {"start": v(10.74, 43.18) * mm, "end": v(10.37, 43.27) * mm});
            skLineSegment(sketch, "E30.212.3", {"start": v(10.74, 43.18) * mm, "end": v(10.96, 43.64) * mm});
            skLineSegment(sketch, "E30.212.4", {"start": v(11.28, 44.08) * mm, "end": v(10.96, 43.64) * mm});
            skLineSegment(sketch, "E30.213.0", {"start": v(9.04, 44.6) * mm, "end": v(9.13, 44.05) * mm});
            skLineSegment(sketch, "E30.213.1", {"start": v(9.13, 44.05) * mm, "end": v(9.13, 43.55) * mm});
            skLineSegment(sketch, "E30.213.2", {"start": v(9.5, 43.47) * mm, "end": v(9.13, 43.55) * mm});
            skLineSegment(sketch, "E30.213.3", {"start": v(9.5, 43.47) * mm, "end": v(9.7, 43.94) * mm});
            skLineSegment(sketch, "E30.213.4", {"start": v(10.01, 44.38) * mm, "end": v(9.7, 43.94) * mm});
            skLineSegment(sketch, "E30.214.0", {"start": v(7.76, 44.83) * mm, "end": v(7.87, 44.3) * mm});
            skLineSegment(sketch, "E30.214.1", {"start": v(7.87, 44.3) * mm, "end": v(7.88, 43.8) * mm});
            skLineSegment(sketch, "E30.214.2", {"start": v(8.25, 43.73) * mm, "end": v(7.88, 43.8) * mm});
            skLineSegment(sketch, "E30.214.3", {"start": v(8.25, 43.73) * mm, "end": v(8.45, 44.2) * mm});
            skLineSegment(sketch, "E30.214.4", {"start": v(8.74, 44.65) * mm, "end": v(8.45, 44.2) * mm});
            skLineSegment(sketch, "E30.215.0", {"start": v(6.48, 45.04) * mm, "end": v(6.6, 44.5) * mm});
            skLineSegment(sketch, "E30.215.1", {"start": v(6.6, 44.5) * mm, "end": v(6.63, 44) * mm});
            skLineSegment(sketch, "E30.215.2", {"start": v(7, 43.94) * mm, "end": v(6.63, 44) * mm});
            skLineSegment(sketch, "E30.215.3", {"start": v(7, 43.94) * mm, "end": v(7.18, 44.42) * mm});
            skLineSegment(sketch, "E30.215.4", {"start": v(7.46, 44.88) * mm, "end": v(7.18, 44.42) * mm});
            skLineSegment(sketch, "E30.216.0", {"start": v(5.19, 45.2) * mm, "end": v(5.33, 44.67) * mm});
            skLineSegment(sketch, "E30.216.1", {"start": v(5.33, 44.67) * mm, "end": v(5.37, 44.17) * mm});
            skLineSegment(sketch, "E30.216.2", {"start": v(5.75, 44.13) * mm, "end": v(5.37, 44.17) * mm});
            skLineSegment(sketch, "E30.216.3", {"start": v(5.75, 44.13) * mm, "end": v(5.91, 44.6) * mm});
            skLineSegment(sketch, "E30.216.4", {"start": v(6.18, 45.08) * mm, "end": v(5.91, 44.6) * mm});
            skLineSegment(sketch, "E30.217.0", {"start": v(3.9, 45.33) * mm, "end": v(4.05, 44.8) * mm});
            skLineSegment(sketch, "E30.217.1", {"start": v(4.05, 44.8) * mm, "end": v(4.1, 44.3) * mm});
            skLineSegment(sketch, "E30.217.2", {"start": v(4.48, 44.27) * mm, "end": v(4.1, 44.3) * mm});
            skLineSegment(sketch, "E30.217.3", {"start": v(4.48, 44.27) * mm, "end": v(4.64, 44.76) * mm});
            skLineSegment(sketch, "E30.217.4", {"start": v(4.89, 45.24) * mm, "end": v(4.64, 44.76) * mm});
            skLineSegment(sketch, "E30.218.0", {"start": v(2.6, 45.43) * mm, "end": v(2.77, 44.9) * mm});
            skLineSegment(sketch, "E30.218.1", {"start": v(2.77, 44.9) * mm, "end": v(2.84, 44.4) * mm});
            skLineSegment(sketch, "E30.218.2", {"start": v(3.22, 44.38) * mm, "end": v(2.84, 44.4) * mm});
            skLineSegment(sketch, "E30.218.3", {"start": v(3.22, 44.38) * mm, "end": v(3.36, 44.87) * mm});
            skLineSegment(sketch, "E30.218.4", {"start": v(3.6, 45.36) * mm, "end": v(3.36, 44.87) * mm});
            skLineSegment(sketch, "E30.219.0", {"start": v(1.3, 45.48) * mm, "end": v(1.48, 44.96) * mm});
            skLineSegment(sketch, "E30.219.1", {"start": v(1.48, 44.96) * mm, "end": v(1.57, 44.47) * mm});
            skLineSegment(sketch, "E30.219.2", {"start": v(1.95, 44.45) * mm, "end": v(1.57, 44.47) * mm});
            skLineSegment(sketch, "E30.219.3", {"start": v(1.95, 44.45) * mm, "end": v(2.07, 44.95) * mm});
            skLineSegment(sketch, "E30.219.4", {"start": v(2.3, 45.44) * mm, "end": v(2.07, 44.95) * mm});
            skPoint(sketch, "E30.center", {"position": v(0, 0) * mm});
            skSolve(sketch);
        }
        {
            var Q0;
            {var subQ2=sQuery(id+"F20.wireOp",EDGE,"E30.208.0");Q0=makeQuery(id+"F20.imprint","IMPRINT",FACE,{"disambiguationData":[TD([[makeQuery(id+"F20.imprint","IMPRINT",EDGE,{"derivedFrom":subQ2}),1.0]])]});}
            var Q1;
            {var subQ2=sQuery(id+"F20.wireOp",EDGE,"E30.209.0");Q1=makeQuery(id+"F20.imprint","IMPRINT",FACE,{"disambiguationData":[TD([[makeQuery(id+"F20.imprint","IMPRINT",EDGE,{"derivedFrom":subQ2}),1.0]])]});}
            var Q2;
            {var subQ2=sQuery(id+"F20.wireOp",EDGE,"E30.195.0");Q2=makeQuery(id+"F20.imprint","IMPRINT",FACE,{"disambiguationData":[TD([[makeQuery(id+"F20.imprint","IMPRINT",EDGE,{"derivedFrom":subQ2}),1.0]])]});}
            var Q3;
            {var subQ2=sQuery(id+"F20.wireOp",EDGE,"E30.203.0");Q3=makeQuery(id+"F20.imprint","IMPRINT",FACE,{"disambiguationData":[TD([[makeQuery(id+"F20.imprint","IMPRINT",EDGE,{"derivedFrom":subQ2}),1.0]])]});}
            var Q4;
            {var subQ2=sQuery(id+"F20.wireOp",EDGE,"E30.190.0");Q4=makeQuery(id+"F20.imprint","IMPRINT",FACE,{"disambiguationData":[TD([[makeQuery(id+"F20.imprint","IMPRINT",EDGE,{"derivedFrom":subQ2}),1.0]])]});}
            var Q5;
            {var subQ2=sQuery(id+"F20.wireOp",EDGE,"E30.204.0");Q5=makeQuery(id+"F20.imprint","IMPRINT",FACE,{"disambiguationData":[TD([[makeQuery(id+"F20.imprint","IMPRINT",EDGE,{"derivedFrom":subQ2}),1.0]])]});}
            var Q6;
            {var subQ2=sQuery(id+"F20.wireOp",EDGE,"E30.189.0");Q6=makeQuery(id+"F20.imprint","IMPRINT",FACE,{"disambiguationData":[TD([[makeQuery(id+"F20.imprint","IMPRINT",EDGE,{"derivedFrom":subQ2}),1.0]])]});}
            var Q7;
            {var subQ2=sQuery(id+"F20.wireOp",EDGE,"E30.191.0");Q7=makeQuery(id+"F20.imprint","IMPRINT",FACE,{"disambiguationData":[TD([[makeQuery(id+"F20.imprint","IMPRINT",EDGE,{"derivedFrom":subQ2}),1.0]])]});}
            var Q8;
            {var subQ2=sQuery(id+"F20.wireOp",EDGE,"E30.192.0");Q8=makeQuery(id+"F20.imprint","IMPRINT",FACE,{"disambiguationData":[TD([[makeQuery(id+"F20.imprint","IMPRINT",EDGE,{"derivedFrom":subQ2}),1.0]])]});}
            var Q9;
            {var subQ2=sQuery(id+"F20.wireOp",EDGE,"E30.193.0");Q9=makeQuery(id+"F20.imprint","IMPRINT",FACE,{"disambiguationData":[TD([[makeQuery(id+"F20.imprint","IMPRINT",EDGE,{"derivedFrom":subQ2}),1.0]])]});}
            var Q10;
            {var subQ2=sQuery(id+"F20.wireOp",EDGE,"E30.210.0");Q10=makeQuery(id+"F20.imprint","IMPRINT",FACE,{"disambiguationData":[TD([[makeQuery(id+"F20.imprint","IMPRINT",EDGE,{"derivedFrom":subQ2}),1.0]])]});}
            var Q11;
            {var subQ2=sQuery(id+"F20.wireOp",EDGE,"E30.194.0");Q11=makeQuery(id+"F20.imprint","IMPRINT",FACE,{"disambiguationData":[TD([[makeQuery(id+"F20.imprint","IMPRINT",EDGE,{"derivedFrom":subQ2}),1.0]])]});}
            var Q12;
            {var subQ2=sQuery(id+"F20.wireOp",EDGE,"E30.211.0");Q12=makeQuery(id+"F20.imprint","IMPRINT",FACE,{"disambiguationData":[TD([[makeQuery(id+"F20.imprint","IMPRINT",EDGE,{"derivedFrom":subQ2}),1.0]])]});}
            var Q13;
            {var subQ2=sQuery(id+"F20.wireOp",EDGE,"E30.196.0");Q13=makeQuery(id+"F20.imprint","IMPRINT",FACE,{"disambiguationData":[TD([[makeQuery(id+"F20.imprint","IMPRINT",EDGE,{"derivedFrom":subQ2}),1.0]])]});}
            var Q14;
            {var subQ2=sQuery(id+"F20.wireOp",EDGE,"E30.213.0");Q14=makeQuery(id+"F20.imprint","IMPRINT",FACE,{"disambiguationData":[TD([[makeQuery(id+"F20.imprint","IMPRINT",EDGE,{"derivedFrom":subQ2}),1.0]])]});}
            var Q15;
            {var subQ2=sQuery(id+"F20.wireOp",EDGE,"E30.197.0");Q15=makeQuery(id+"F20.imprint","IMPRINT",FACE,{"disambiguationData":[TD([[makeQuery(id+"F20.imprint","IMPRINT",EDGE,{"derivedFrom":subQ2}),1.0]])]});}
            var Q16;
            {var subQ2=sQuery(id+"F20.wireOp",EDGE,"E30.198.0");Q16=makeQuery(id+"F20.imprint","IMPRINT",FACE,{"disambiguationData":[TD([[makeQuery(id+"F20.imprint","IMPRINT",EDGE,{"derivedFrom":subQ2}),1.0]])]});}
            var Q17;
            {var subQ2=sQuery(id+"F20.wireOp",EDGE,"E30.199.0");Q17=makeQuery(id+"F20.imprint","IMPRINT",FACE,{"disambiguationData":[TD([[makeQuery(id+"F20.imprint","IMPRINT",EDGE,{"derivedFrom":subQ2}),1.0]])]});}
            var Q18;
            {var subQ2=sQuery(id+"F20.wireOp",EDGE,"E30.216.0");Q18=makeQuery(id+"F20.imprint","IMPRINT",FACE,{"disambiguationData":[TD([[makeQuery(id+"F20.imprint","IMPRINT",EDGE,{"derivedFrom":subQ2}),1.0]])]});}
            var Q19;
            {var subQ2=sQuery(id+"F20.wireOp",EDGE,"E30.200.0");Q19=makeQuery(id+"F20.imprint","IMPRINT",FACE,{"disambiguationData":[TD([[makeQuery(id+"F20.imprint","IMPRINT",EDGE,{"derivedFrom":subQ2}),1.0]])]});}
            var Q20;
            {var subQ2=sQuery(id+"F20.wireOp",EDGE,"E30.217.0");Q20=makeQuery(id+"F20.imprint","IMPRINT",FACE,{"disambiguationData":[TD([[makeQuery(id+"F20.imprint","IMPRINT",EDGE,{"derivedFrom":subQ2}),1.0]])]});}
            var Q21;
            {var subQ2=sQuery(id+"F20.wireOp",EDGE,"E30.201.0");Q21=makeQuery(id+"F20.imprint","IMPRINT",FACE,{"disambiguationData":[TD([[makeQuery(id+"F20.imprint","IMPRINT",EDGE,{"derivedFrom":subQ2}),1.0]])]});}
            var Q22;
            {var subQ2=sQuery(id+"F20.wireOp",EDGE,"E30.218.0");Q22=makeQuery(id+"F20.imprint","IMPRINT",FACE,{"disambiguationData":[TD([[makeQuery(id+"F20.imprint","IMPRINT",EDGE,{"derivedFrom":subQ2}),1.0]])]});}
            var Q23;
            {var subQ2=sQuery(id+"F20.wireOp",EDGE,"E30.202.0");Q23=makeQuery(id+"F20.imprint","IMPRINT",FACE,{"disambiguationData":[TD([[makeQuery(id+"F20.imprint","IMPRINT",EDGE,{"derivedFrom":subQ2}),1.0]])]});}
            var Q24;
            {var subQ2=sQuery(id+"F20.wireOp",EDGE,"E30.206.0");Q24=makeQuery(id+"F20.imprint","IMPRINT",FACE,{"disambiguationData":[TD([[makeQuery(id+"F20.imprint","IMPRINT",EDGE,{"derivedFrom":subQ2}),1.0]])]});}
            var Q25;
            {var subQ2=sQuery(id+"F20.wireOp",EDGE,"E30.205.0");Q25=makeQuery(id+"F20.imprint","IMPRINT",FACE,{"disambiguationData":[TD([[makeQuery(id+"F20.imprint","IMPRINT",EDGE,{"derivedFrom":subQ2}),1.0]])]});}
            var Q26;
            {var subQ2=sQuery(id+"F20.wireOp",EDGE,"E30.207.0");Q26=makeQuery(id+"F20.imprint","IMPRINT",FACE,{"disambiguationData":[TD([[makeQuery(id+"F20.imprint","IMPRINT",EDGE,{"derivedFrom":subQ2}),1.0]])]});}
            var Q27;
            {var subQ2=sQuery(id+"F20.wireOp",EDGE,"E30.212.0");Q27=makeQuery(id+"F20.imprint","IMPRINT",FACE,{"disambiguationData":[TD([[makeQuery(id+"F20.imprint","IMPRINT",EDGE,{"derivedFrom":subQ2}),1.0]])]});}
            var Q28;
            {var subQ2=sQuery(id+"F20.wireOp",EDGE,"E30.214.0");Q28=makeQuery(id+"F20.imprint","IMPRINT",FACE,{"disambiguationData":[TD([[makeQuery(id+"F20.imprint","IMPRINT",EDGE,{"derivedFrom":subQ2}),1.0]])]});}
            var Q29;
            {var subQ2=sQuery(id+"F20.wireOp",EDGE,"E30.215.0");Q29=makeQuery(id+"F20.imprint","IMPRINT",FACE,{"disambiguationData":[TD([[makeQuery(id+"F20.imprint","IMPRINT",EDGE,{"derivedFrom":subQ2}),1.0]])]});}
            var Q30;
            {var subQ2=sQuery(id+"F20.wireOp",EDGE,"E30.175.0");Q30=makeQuery(id+"F20.imprint","IMPRINT",FACE,{"disambiguationData":[TD([[makeQuery(id+"F20.imprint","IMPRINT",EDGE,{"derivedFrom":subQ2}),1.0]])]});}
            var Q31;
            {var subQ2=sQuery(id+"F20.wireOp",EDGE,"E30.159.0");Q31=makeQuery(id+"F20.imprint","IMPRINT",FACE,{"disambiguationData":[TD([[makeQuery(id+"F20.imprint","IMPRINT",EDGE,{"derivedFrom":subQ2}),1.0]])]});}
            var Q32;
            {var subQ2=sQuery(id+"F20.wireOp",EDGE,"E30.148.0");Q32=makeQuery(id+"F20.imprint","IMPRINT",FACE,{"disambiguationData":[TD([[makeQuery(id+"F20.imprint","IMPRINT",EDGE,{"derivedFrom":subQ2}),1.0]])]});}
            var Q33;
            {var subQ2=sQuery(id+"F20.wireOp",EDGE,"E30.180.0");Q33=makeQuery(id+"F20.imprint","IMPRINT",FACE,{"disambiguationData":[TD([[makeQuery(id+"F20.imprint","IMPRINT",EDGE,{"derivedFrom":subQ2}),1.0]])]});}
            var Q34;
            {var subQ2=sQuery(id+"F20.wireOp",EDGE,"E30.181.0");Q34=makeQuery(id+"F20.imprint","IMPRINT",FACE,{"disambiguationData":[TD([[makeQuery(id+"F20.imprint","IMPRINT",EDGE,{"derivedFrom":subQ2}),1.0]])]});}
            var Q35;
            {var subQ2=sQuery(id+"F20.wireOp",EDGE,"E30.149.0");Q35=makeQuery(id+"F20.imprint","IMPRINT",FACE,{"disambiguationData":[TD([[makeQuery(id+"F20.imprint","IMPRINT",EDGE,{"derivedFrom":subQ2}),1.0]])]});}
            var Q36;
            {var subQ2=sQuery(id+"F20.wireOp",EDGE,"E30.182.0");Q36=makeQuery(id+"F20.imprint","IMPRINT",FACE,{"disambiguationData":[TD([[makeQuery(id+"F20.imprint","IMPRINT",EDGE,{"derivedFrom":subQ2}),1.0]])]});}
            var Q37;
            {var subQ2=sQuery(id+"F20.wireOp",EDGE,"E30.151.0");Q37=makeQuery(id+"F20.imprint","IMPRINT",FACE,{"disambiguationData":[TD([[makeQuery(id+"F20.imprint","IMPRINT",EDGE,{"derivedFrom":subQ2}),1.0]])]});}
            var Q38;
            {var subQ2=sQuery(id+"F20.wireOp",EDGE,"E30.152.0");Q38=makeQuery(id+"F20.imprint","IMPRINT",FACE,{"disambiguationData":[TD([[makeQuery(id+"F20.imprint","IMPRINT",EDGE,{"derivedFrom":subQ2}),1.0]])]});}
            var Q39;
            {var subQ2=sQuery(id+"F20.wireOp",EDGE,"E30.186.0");Q39=makeQuery(id+"F20.imprint","IMPRINT",FACE,{"disambiguationData":[TD([[makeQuery(id+"F20.imprint","IMPRINT",EDGE,{"derivedFrom":subQ2}),1.0]])]});}
            var Q40;
            {var subQ2=sQuery(id+"F20.wireOp",EDGE,"E30.187.0");Q40=makeQuery(id+"F20.imprint","IMPRINT",FACE,{"disambiguationData":[TD([[makeQuery(id+"F20.imprint","IMPRINT",EDGE,{"derivedFrom":subQ2}),1.0]])]});}
            var Q41;
            {var subQ2=sQuery(id+"F20.wireOp",EDGE,"E30.142.0");Q41=makeQuery(id+"F20.imprint","IMPRINT",FACE,{"disambiguationData":[TD([[makeQuery(id+"F20.imprint","IMPRINT",EDGE,{"derivedFrom":subQ2}),1.0]])]});}
            var Q42;
            {var subQ2=sQuery(id+"F20.wireOp",EDGE,"E30.174.0");Q42=makeQuery(id+"F20.imprint","IMPRINT",FACE,{"disambiguationData":[TD([[makeQuery(id+"F20.imprint","IMPRINT",EDGE,{"derivedFrom":subQ2}),1.0]])]});}
            var Q43;
            {var subQ2=sQuery(id+"F20.wireOp",EDGE,"E30.188.0");Q43=makeQuery(id+"F20.imprint","IMPRINT",FACE,{"disambiguationData":[TD([[makeQuery(id+"F20.imprint","IMPRINT",EDGE,{"derivedFrom":subQ2}),1.0]])]});}
            var Q44;
            {var subQ2=sQuery(id+"F20.wireOp",EDGE,"E30.143.0");Q44=makeQuery(id+"F20.imprint","IMPRINT",FACE,{"disambiguationData":[TD([[makeQuery(id+"F20.imprint","IMPRINT",EDGE,{"derivedFrom":subQ2}),1.0]])]});}
            var Q45;
            {var subQ2=sQuery(id+"F20.wireOp",EDGE,"E30.144.0");Q45=makeQuery(id+"F20.imprint","IMPRINT",FACE,{"disambiguationData":[TD([[makeQuery(id+"F20.imprint","IMPRINT",EDGE,{"derivedFrom":subQ2}),1.0]])]});}
            var Q46;
            {var subQ2=sQuery(id+"F20.wireOp",EDGE,"E30.145.0");Q46=makeQuery(id+"F20.imprint","IMPRINT",FACE,{"disambiguationData":[TD([[makeQuery(id+"F20.imprint","IMPRINT",EDGE,{"derivedFrom":subQ2}),1.0]])]});}
            var Q47;
            {var subQ2=sQuery(id+"F20.wireOp",EDGE,"E30.177.0");Q47=makeQuery(id+"F20.imprint","IMPRINT",FACE,{"disambiguationData":[TD([[makeQuery(id+"F20.imprint","IMPRINT",EDGE,{"derivedFrom":subQ2}),1.0]])]});}
            var Q48;
            {var subQ2=sQuery(id+"F20.wireOp",EDGE,"E30.178.0");Q48=makeQuery(id+"F20.imprint","IMPRINT",FACE,{"disambiguationData":[TD([[makeQuery(id+"F20.imprint","IMPRINT",EDGE,{"derivedFrom":subQ2}),1.0]])]});}
            var Q49;
            {var subQ2=sQuery(id+"F20.wireOp",EDGE,"E30.162.0");Q49=makeQuery(id+"F20.imprint","IMPRINT",FACE,{"disambiguationData":[TD([[makeQuery(id+"F20.imprint","IMPRINT",EDGE,{"derivedFrom":subQ2}),1.0]])]});}
            var Q50;
            {var subQ2=sQuery(id+"F20.wireOp",EDGE,"E30.146.0");Q50=makeQuery(id+"F20.imprint","IMPRINT",FACE,{"disambiguationData":[TD([[makeQuery(id+"F20.imprint","IMPRINT",EDGE,{"derivedFrom":subQ2}),1.0]])]});}
            var Q51;
            {var subQ2=sQuery(id+"F20.wireOp",EDGE,"E30.147.0");Q51=makeQuery(id+"F20.imprint","IMPRINT",FACE,{"disambiguationData":[TD([[makeQuery(id+"F20.imprint","IMPRINT",EDGE,{"derivedFrom":subQ2}),1.0]])]});}
            var Q52;
            {var subQ2=sQuery(id+"F20.wireOp",EDGE,"E30.179.0");Q52=makeQuery(id+"F20.imprint","IMPRINT",FACE,{"disambiguationData":[TD([[makeQuery(id+"F20.imprint","IMPRINT",EDGE,{"derivedFrom":subQ2}),1.0]])]});}
            var Q53;
            {var subQ2=sQuery(id+"F20.wireOp",EDGE,"E30.163.0");Q53=makeQuery(id+"F20.imprint","IMPRINT",FACE,{"disambiguationData":[TD([[makeQuery(id+"F20.imprint","IMPRINT",EDGE,{"derivedFrom":subQ2}),1.0]])]});}
            var Q54;
            {var subQ2=sQuery(id+"F20.wireOp",EDGE,"E30.150.0");Q54=makeQuery(id+"F20.imprint","IMPRINT",FACE,{"disambiguationData":[TD([[makeQuery(id+"F20.imprint","IMPRINT",EDGE,{"derivedFrom":subQ2}),1.0]])]});}
            var Q55;
            {var subQ2=sQuery(id+"F20.wireOp",EDGE,"E30.183.0");Q55=makeQuery(id+"F20.imprint","IMPRINT",FACE,{"disambiguationData":[TD([[makeQuery(id+"F20.imprint","IMPRINT",EDGE,{"derivedFrom":subQ2}),1.0]])]});}
            var Q56;
            {var subQ2=sQuery(id+"F20.wireOp",EDGE,"E30.168.0");Q56=makeQuery(id+"F20.imprint","IMPRINT",FACE,{"disambiguationData":[TD([[makeQuery(id+"F20.imprint","IMPRINT",EDGE,{"derivedFrom":subQ2}),1.0]])]});}
            var Q57;
            {var subQ2=sQuery(id+"F20.wireOp",EDGE,"E30.185.0");Q57=makeQuery(id+"F20.imprint","IMPRINT",FACE,{"disambiguationData":[TD([[makeQuery(id+"F20.imprint","IMPRINT",EDGE,{"derivedFrom":subQ2}),1.0]])]});}
            var Q58;
            {var subQ2=sQuery(id+"F20.wireOp",EDGE,"E30.153.0");Q58=makeQuery(id+"F20.imprint","IMPRINT",FACE,{"disambiguationData":[TD([[makeQuery(id+"F20.imprint","IMPRINT",EDGE,{"derivedFrom":subQ2}),1.0]])]});}
            var Q59;
            {var subQ2=sQuery(id+"F20.wireOp",EDGE,"E30.154.0");Q59=makeQuery(id+"F20.imprint","IMPRINT",FACE,{"disambiguationData":[TD([[makeQuery(id+"F20.imprint","IMPRINT",EDGE,{"derivedFrom":subQ2}),1.0]])]});}
            var Q60;
            {var subQ2=sQuery(id+"F20.wireOp",EDGE,"E30.171.0");Q60=makeQuery(id+"F20.imprint","IMPRINT",FACE,{"disambiguationData":[TD([[makeQuery(id+"F20.imprint","IMPRINT",EDGE,{"derivedFrom":subQ2}),1.0]])]});}
            var Q61;
            {var subQ2=sQuery(id+"F20.wireOp",EDGE,"E30.155.0");Q61=makeQuery(id+"F20.imprint","IMPRINT",FACE,{"disambiguationData":[TD([[makeQuery(id+"F20.imprint","IMPRINT",EDGE,{"derivedFrom":subQ2}),1.0]])]});}
            var Q62;
            {var subQ2=sQuery(id+"F20.wireOp",EDGE,"E30.173.0");Q62=makeQuery(id+"F20.imprint","IMPRINT",FACE,{"disambiguationData":[TD([[makeQuery(id+"F20.imprint","IMPRINT",EDGE,{"derivedFrom":subQ2}),1.0]])]});}
            var Q63;
            {var subQ2=sQuery(id+"F20.wireOp",EDGE,"E30.157.0");Q63=makeQuery(id+"F20.imprint","IMPRINT",FACE,{"disambiguationData":[TD([[makeQuery(id+"F20.imprint","IMPRINT",EDGE,{"derivedFrom":subQ2}),1.0]])]});}
            var Q64;
            {var subQ2=sQuery(id+"F20.wireOp",EDGE,"E30.176.0");Q64=makeQuery(id+"F20.imprint","IMPRINT",FACE,{"disambiguationData":[TD([[makeQuery(id+"F20.imprint","IMPRINT",EDGE,{"derivedFrom":subQ2}),1.0]])]});}
            var Q65;
            {var subQ2=sQuery(id+"F20.wireOp",EDGE,"E30.160.0");Q65=makeQuery(id+"F20.imprint","IMPRINT",FACE,{"disambiguationData":[TD([[makeQuery(id+"F20.imprint","IMPRINT",EDGE,{"derivedFrom":subQ2}),1.0]])]});}
            var Q66;
            {var subQ2=sQuery(id+"F20.wireOp",EDGE,"E30.161.0");Q66=makeQuery(id+"F20.imprint","IMPRINT",FACE,{"disambiguationData":[TD([[makeQuery(id+"F20.imprint","IMPRINT",EDGE,{"derivedFrom":subQ2}),1.0]])]});}
            var Q67;
            {var subQ2=sQuery(id+"F20.wireOp",EDGE,"E30.164.0");Q67=makeQuery(id+"F20.imprint","IMPRINT",FACE,{"disambiguationData":[TD([[makeQuery(id+"F20.imprint","IMPRINT",EDGE,{"derivedFrom":subQ2}),1.0]])]});}
            var Q68;
            {var subQ2=sQuery(id+"F20.wireOp",EDGE,"E30.167.0");Q68=makeQuery(id+"F20.imprint","IMPRINT",FACE,{"disambiguationData":[TD([[makeQuery(id+"F20.imprint","IMPRINT",EDGE,{"derivedFrom":subQ2}),1.0]])]});}
            var Q69;
            {var subQ2=sQuery(id+"F20.wireOp",EDGE,"E30.184.0");Q69=makeQuery(id+"F20.imprint","IMPRINT",FACE,{"disambiguationData":[TD([[makeQuery(id+"F20.imprint","IMPRINT",EDGE,{"derivedFrom":subQ2}),1.0]])]});}
            var Q70;
            {var subQ2=sQuery(id+"F20.wireOp",EDGE,"E30.169.0");Q70=makeQuery(id+"F20.imprint","IMPRINT",FACE,{"disambiguationData":[TD([[makeQuery(id+"F20.imprint","IMPRINT",EDGE,{"derivedFrom":subQ2}),1.0]])]});}
            var Q71;
            {var subQ2=sQuery(id+"F20.wireOp",EDGE,"E30.170.0");Q71=makeQuery(id+"F20.imprint","IMPRINT",FACE,{"disambiguationData":[TD([[makeQuery(id+"F20.imprint","IMPRINT",EDGE,{"derivedFrom":subQ2}),1.0]])]});}
            var Q72;
            {var subQ2=sQuery(id+"F20.wireOp",EDGE,"E30.158.0");Q72=makeQuery(id+"F20.imprint","IMPRINT",FACE,{"disambiguationData":[TD([[makeQuery(id+"F20.imprint","IMPRINT",EDGE,{"derivedFrom":subQ2}),1.0]])]});}
            var Q73;
            {var subQ2=sQuery(id+"F20.wireOp",EDGE,"E30.172.0");Q73=makeQuery(id+"F20.imprint","IMPRINT",FACE,{"disambiguationData":[TD([[makeQuery(id+"F20.imprint","IMPRINT",EDGE,{"derivedFrom":subQ2}),1.0]])]});}
            var Q74;
            {var subQ2=sQuery(id+"F20.wireOp",EDGE,"E30.156.0");Q74=makeQuery(id+"F20.imprint","IMPRINT",FACE,{"disambiguationData":[TD([[makeQuery(id+"F20.imprint","IMPRINT",EDGE,{"derivedFrom":subQ2}),1.0]])]});}
            var Q75;
            {var subQ2=sQuery(id+"F20.wireOp",EDGE,"E30.166.0");Q75=makeQuery(id+"F20.imprint","IMPRINT",FACE,{"disambiguationData":[TD([[makeQuery(id+"F20.imprint","IMPRINT",EDGE,{"derivedFrom":subQ2}),1.0]])]});}
            var Q76;
            {var subQ2=sQuery(id+"F20.wireOp",EDGE,"E30.165.0");Q76=makeQuery(id+"F20.imprint","IMPRINT",FACE,{"disambiguationData":[TD([[makeQuery(id+"F20.imprint","IMPRINT",EDGE,{"derivedFrom":subQ2}),1.0]])]});}
            var Q77;
            {var subQ2=sQuery(id+"F20.wireOp",EDGE,"E30.79.0");Q77=makeQuery(id+"F20.imprint","IMPRINT",FACE,{"disambiguationData":[TD([[makeQuery(id+"F20.imprint","IMPRINT",EDGE,{"derivedFrom":subQ2}),1.0]])]});}
            var Q78;
            {var subQ2=sQuery(id+"F20.wireOp",EDGE,"E30.127.0");Q78=makeQuery(id+"F20.imprint","IMPRINT",FACE,{"disambiguationData":[TD([[makeQuery(id+"F20.imprint","IMPRINT",EDGE,{"derivedFrom":subQ2}),1.0]])]});}
            var Q79;
            {var subQ2=sQuery(id+"F20.wireOp",EDGE,"E30.95.0");Q79=makeQuery(id+"F20.imprint","IMPRINT",FACE,{"disambiguationData":[TD([[makeQuery(id+"F20.imprint","IMPRINT",EDGE,{"derivedFrom":subQ2}),1.0]])]});}
            var Q80;
            {var subQ2=sQuery(id+"F20.wireOp",EDGE,"E30.97.0");Q80=makeQuery(id+"F20.imprint","IMPRINT",FACE,{"disambiguationData":[TD([[makeQuery(id+"F20.imprint","IMPRINT",EDGE,{"derivedFrom":subQ2}),1.0]])]});}
            var Q81;
            {var subQ2=sQuery(id+"F20.wireOp",EDGE,"E30.99.0");Q81=makeQuery(id+"F20.imprint","IMPRINT",FACE,{"disambiguationData":[TD([[makeQuery(id+"F20.imprint","IMPRINT",EDGE,{"derivedFrom":subQ2}),1.0]])]});}
            var Q82;
            {var subQ2=sQuery(id+"F20.wireOp",EDGE,"E30.100.0");Q82=makeQuery(id+"F20.imprint","IMPRINT",FACE,{"disambiguationData":[TD([[makeQuery(id+"F20.imprint","IMPRINT",EDGE,{"derivedFrom":subQ2}),1.0]])]});}
            var Q83;
            {var subQ2=sQuery(id+"F20.wireOp",EDGE,"E30.117.0");Q83=makeQuery(id+"F20.imprint","IMPRINT",FACE,{"disambiguationData":[TD([[makeQuery(id+"F20.imprint","IMPRINT",EDGE,{"derivedFrom":subQ2}),1.0]])]});}
            var Q84;
            {var subQ2=sQuery(id+"F20.wireOp",EDGE,"E30.133.0");Q84=makeQuery(id+"F20.imprint","IMPRINT",FACE,{"disambiguationData":[TD([[makeQuery(id+"F20.imprint","IMPRINT",EDGE,{"derivedFrom":subQ2}),1.0]])]});}
            var Q85;
            {var subQ2=sQuery(id+"F20.wireOp",EDGE,"E30.87.0");Q85=makeQuery(id+"F20.imprint","IMPRINT",FACE,{"disambiguationData":[TD([[makeQuery(id+"F20.imprint","IMPRINT",EDGE,{"derivedFrom":subQ2}),1.0]])]});}
            var Q86;
            {var subQ2=sQuery(id+"F20.wireOp",EDGE,"E30.88.0");Q86=makeQuery(id+"F20.imprint","IMPRINT",FACE,{"disambiguationData":[TD([[makeQuery(id+"F20.imprint","IMPRINT",EDGE,{"derivedFrom":subQ2}),1.0]])]});}
            var Q87;
            {var subQ2=sQuery(id+"F20.wireOp",EDGE,"E30.105.0");Q87=makeQuery(id+"F20.imprint","IMPRINT",FACE,{"disambiguationData":[TD([[makeQuery(id+"F20.imprint","IMPRINT",EDGE,{"derivedFrom":subQ2}),1.0]])]});}
            var Q88;
            {var subQ2=sQuery(id+"F20.wireOp",EDGE,"E30.89.0");Q88=makeQuery(id+"F20.imprint","IMPRINT",FACE,{"disambiguationData":[TD([[makeQuery(id+"F20.imprint","IMPRINT",EDGE,{"derivedFrom":subQ2}),1.0]])]});}
            var Q89;
            {var subQ2=sQuery(id+"F20.wireOp",EDGE,"E30.122.0");Q89=makeQuery(id+"F20.imprint","IMPRINT",FACE,{"disambiguationData":[TD([[makeQuery(id+"F20.imprint","IMPRINT",EDGE,{"derivedFrom":subQ2}),1.0]])]});}
            var Q90;
            {var subQ2=sQuery(id+"F20.wireOp",EDGE,"E30.91.0");Q90=makeQuery(id+"F20.imprint","IMPRINT",FACE,{"disambiguationData":[TD([[makeQuery(id+"F20.imprint","IMPRINT",EDGE,{"derivedFrom":subQ2}),1.0]])]});}
            var Q91;
            {var subQ2=sQuery(id+"F20.wireOp",EDGE,"E30.94.0");Q91=makeQuery(id+"F20.imprint","IMPRINT",FACE,{"disambiguationData":[TD([[makeQuery(id+"F20.imprint","IMPRINT",EDGE,{"derivedFrom":subQ2}),1.0]])]});}
            var Q92;
            {var subQ2=sQuery(id+"F20.wireOp",EDGE,"E30.126.0");Q92=makeQuery(id+"F20.imprint","IMPRINT",FACE,{"disambiguationData":[TD([[makeQuery(id+"F20.imprint","IMPRINT",EDGE,{"derivedFrom":subQ2}),1.0]])]});}
            var Q93;
            {var subQ2=sQuery(id+"F20.wireOp",EDGE,"E30.124.0");Q93=makeQuery(id+"F20.imprint","IMPRINT",FACE,{"disambiguationData":[TD([[makeQuery(id+"F20.imprint","IMPRINT",EDGE,{"derivedFrom":subQ2}),1.0]])]});}
            var Q94;
            {var subQ2=sQuery(id+"F20.wireOp",EDGE,"E30.92.0");Q94=makeQuery(id+"F20.imprint","IMPRINT",FACE,{"disambiguationData":[TD([[makeQuery(id+"F20.imprint","IMPRINT",EDGE,{"derivedFrom":subQ2}),1.0]])]});}
            var Q95;
            {var subQ2=sQuery(id+"F20.wireOp",EDGE,"E30.141.0");Q95=makeQuery(id+"F20.imprint","IMPRINT",FACE,{"disambiguationData":[TD([[makeQuery(id+"F20.imprint","IMPRINT",EDGE,{"derivedFrom":subQ2}),1.0]])]});}
            var Q96;
            {var subQ2=sQuery(id+"F20.wireOp",EDGE,"E30.125.0");Q96=makeQuery(id+"F20.imprint","IMPRINT",FACE,{"disambiguationData":[TD([[makeQuery(id+"F20.imprint","IMPRINT",EDGE,{"derivedFrom":subQ2}),1.0]])]});}
            var Q97;
            {var subQ2=sQuery(id+"F20.wireOp",EDGE,"E30.93.0");Q97=makeQuery(id+"F20.imprint","IMPRINT",FACE,{"disambiguationData":[TD([[makeQuery(id+"F20.imprint","IMPRINT",EDGE,{"derivedFrom":subQ2}),1.0]])]});}
            var Q98;
            {var subQ2=sQuery(id+"F20.wireOp",EDGE,"E30.80.0");Q98=makeQuery(id+"F20.imprint","IMPRINT",FACE,{"disambiguationData":[TD([[makeQuery(id+"F20.imprint","IMPRINT",EDGE,{"derivedFrom":subQ2}),1.0]])]});}
            var Q99;
            {var subQ2=sQuery(id+"F20.wireOp",EDGE,"E30.128.0");Q99=makeQuery(id+"F20.imprint","IMPRINT",FACE,{"disambiguationData":[TD([[makeQuery(id+"F20.imprint","IMPRINT",EDGE,{"derivedFrom":subQ2}),1.0]])]});}
            var Q100;
            {var subQ2=sQuery(id+"F20.wireOp",EDGE,"E30.96.0");Q100=makeQuery(id+"F20.imprint","IMPRINT",FACE,{"disambiguationData":[TD([[makeQuery(id+"F20.imprint","IMPRINT",EDGE,{"derivedFrom":subQ2}),1.0]])]});}
            var Q101;
            {var subQ2=sQuery(id+"F20.wireOp",EDGE,"E30.81.0");Q101=makeQuery(id+"F20.imprint","IMPRINT",FACE,{"disambiguationData":[TD([[makeQuery(id+"F20.imprint","IMPRINT",EDGE,{"derivedFrom":subQ2}),1.0]])]});}
            var Q102;
            {var subQ2=sQuery(id+"F20.wireOp",EDGE,"E30.82.0");Q102=makeQuery(id+"F20.imprint","IMPRINT",FACE,{"disambiguationData":[TD([[makeQuery(id+"F20.imprint","IMPRINT",EDGE,{"derivedFrom":subQ2}),1.0]])]});}
            var Q103;
            {var subQ2=sQuery(id+"F20.wireOp",EDGE,"E30.130.0");Q103=makeQuery(id+"F20.imprint","IMPRINT",FACE,{"disambiguationData":[TD([[makeQuery(id+"F20.imprint","IMPRINT",EDGE,{"derivedFrom":subQ2}),1.0]])]});}
            var Q104;
            {var subQ2=sQuery(id+"F20.wireOp",EDGE,"E30.98.0");Q104=makeQuery(id+"F20.imprint","IMPRINT",FACE,{"disambiguationData":[TD([[makeQuery(id+"F20.imprint","IMPRINT",EDGE,{"derivedFrom":subQ2}),1.0]])]});}
            var Q105;
            {var subQ2=sQuery(id+"F20.wireOp",EDGE,"E30.131.0");Q105=makeQuery(id+"F20.imprint","IMPRINT",FACE,{"disambiguationData":[TD([[makeQuery(id+"F20.imprint","IMPRINT",EDGE,{"derivedFrom":subQ2}),1.0]])]});}
            var Q106;
            {var subQ2=sQuery(id+"F20.wireOp",EDGE,"E30.84.0");Q106=makeQuery(id+"F20.imprint","IMPRINT",FACE,{"disambiguationData":[TD([[makeQuery(id+"F20.imprint","IMPRINT",EDGE,{"derivedFrom":subQ2}),1.0]])]});}
            var Q107;
            {var subQ2=sQuery(id+"F20.wireOp",EDGE,"E30.132.0");Q107=makeQuery(id+"F20.imprint","IMPRINT",FACE,{"disambiguationData":[TD([[makeQuery(id+"F20.imprint","IMPRINT",EDGE,{"derivedFrom":subQ2}),1.0]])]});}
            var Q108;
            {var subQ2=sQuery(id+"F20.wireOp",EDGE,"E30.116.0");Q108=makeQuery(id+"F20.imprint","IMPRINT",FACE,{"disambiguationData":[TD([[makeQuery(id+"F20.imprint","IMPRINT",EDGE,{"derivedFrom":subQ2}),1.0]])]});}
            var Q109;
            {var subQ2=sQuery(id+"F20.wireOp",EDGE,"E30.101.0");Q109=makeQuery(id+"F20.imprint","IMPRINT",FACE,{"disambiguationData":[TD([[makeQuery(id+"F20.imprint","IMPRINT",EDGE,{"derivedFrom":subQ2}),1.0]])]});}
            var Q110;
            {var subQ2=sQuery(id+"F20.wireOp",EDGE,"E30.118.0");Q110=makeQuery(id+"F20.imprint","IMPRINT",FACE,{"disambiguationData":[TD([[makeQuery(id+"F20.imprint","IMPRINT",EDGE,{"derivedFrom":subQ2}),1.0]])]});}
            var Q111;
            {var subQ2=sQuery(id+"F20.wireOp",EDGE,"E30.102.0");Q111=makeQuery(id+"F20.imprint","IMPRINT",FACE,{"disambiguationData":[TD([[makeQuery(id+"F20.imprint","IMPRINT",EDGE,{"derivedFrom":subQ2}),1.0]])]});}
            var Q112;
            {var subQ2=sQuery(id+"F20.wireOp",EDGE,"E30.86.0");Q112=makeQuery(id+"F20.imprint","IMPRINT",FACE,{"disambiguationData":[TD([[makeQuery(id+"F20.imprint","IMPRINT",EDGE,{"derivedFrom":subQ2}),1.0]])]});}
            var Q113;
            {var subQ2=sQuery(id+"F20.wireOp",EDGE,"E30.134.0");Q113=makeQuery(id+"F20.imprint","IMPRINT",FACE,{"disambiguationData":[TD([[makeQuery(id+"F20.imprint","IMPRINT",EDGE,{"derivedFrom":subQ2}),1.0]])]});}
            var Q114;
            {var subQ2=sQuery(id+"F20.wireOp",EDGE,"E30.120.0");Q114=makeQuery(id+"F20.imprint","IMPRINT",FACE,{"disambiguationData":[TD([[makeQuery(id+"F20.imprint","IMPRINT",EDGE,{"derivedFrom":subQ2}),1.0]])]});}
            var Q115;
            {var subQ2=sQuery(id+"F20.wireOp",EDGE,"E30.104.0");Q115=makeQuery(id+"F20.imprint","IMPRINT",FACE,{"disambiguationData":[TD([[makeQuery(id+"F20.imprint","IMPRINT",EDGE,{"derivedFrom":subQ2}),1.0]])]});}
            var Q116;
            {var subQ2=sQuery(id+"F20.wireOp",EDGE,"E30.136.0");Q116=makeQuery(id+"F20.imprint","IMPRINT",FACE,{"disambiguationData":[TD([[makeQuery(id+"F20.imprint","IMPRINT",EDGE,{"derivedFrom":subQ2}),1.0]])]});}
            var Q117;
            {var subQ2=sQuery(id+"F20.wireOp",EDGE,"E30.121.0");Q117=makeQuery(id+"F20.imprint","IMPRINT",FACE,{"disambiguationData":[TD([[makeQuery(id+"F20.imprint","IMPRINT",EDGE,{"derivedFrom":subQ2}),1.0]])]});}
            var Q118;
            {var subQ2=sQuery(id+"F20.wireOp",EDGE,"E30.137.0");Q118=makeQuery(id+"F20.imprint","IMPRINT",FACE,{"disambiguationData":[TD([[makeQuery(id+"F20.imprint","IMPRINT",EDGE,{"derivedFrom":subQ2}),1.0]])]});}
            var Q119;
            {var subQ2=sQuery(id+"F20.wireOp",EDGE,"E30.90.0");Q119=makeQuery(id+"F20.imprint","IMPRINT",FACE,{"disambiguationData":[TD([[makeQuery(id+"F20.imprint","IMPRINT",EDGE,{"derivedFrom":subQ2}),1.0]])]});}
            var Q120;
            {var subQ2=sQuery(id+"F20.wireOp",EDGE,"E30.138.0");Q120=makeQuery(id+"F20.imprint","IMPRINT",FACE,{"disambiguationData":[TD([[makeQuery(id+"F20.imprint","IMPRINT",EDGE,{"derivedFrom":subQ2}),1.0]])]});}
            var Q121;
            {var subQ2=sQuery(id+"F20.wireOp",EDGE,"E30.123.0");Q121=makeQuery(id+"F20.imprint","IMPRINT",FACE,{"disambiguationData":[TD([[makeQuery(id+"F20.imprint","IMPRINT",EDGE,{"derivedFrom":subQ2}),1.0]])]});}
            var Q122;
            {var subQ2=sQuery(id+"F20.wireOp",EDGE,"E30.107.0");Q122=makeQuery(id+"F20.imprint","IMPRINT",FACE,{"disambiguationData":[TD([[makeQuery(id+"F20.imprint","IMPRINT",EDGE,{"derivedFrom":subQ2}),1.0]])]});}
            var Q123;
            {var subQ2=sQuery(id+"F20.wireOp",EDGE,"E30.78.0");Q123=makeQuery(id+"F20.imprint","IMPRINT",FACE,{"disambiguationData":[TD([[makeQuery(id+"F20.imprint","IMPRINT",EDGE,{"derivedFrom":subQ2}),1.0]])]});}
            var Q124;
            {var subQ2=sQuery(id+"F20.wireOp",EDGE,"E30.108.0");Q124=makeQuery(id+"F20.imprint","IMPRINT",FACE,{"disambiguationData":[TD([[makeQuery(id+"F20.imprint","IMPRINT",EDGE,{"derivedFrom":subQ2}),1.0]])]});}
            var Q125;
            {var subQ2=sQuery(id+"F20.wireOp",EDGE,"E30.109.0");Q125=makeQuery(id+"F20.imprint","IMPRINT",FACE,{"disambiguationData":[TD([[makeQuery(id+"F20.imprint","IMPRINT",EDGE,{"derivedFrom":subQ2}),1.0]])]});}
            var Q126;
            {var subQ2=sQuery(id+"F20.wireOp",EDGE,"E30.129.0");Q126=makeQuery(id+"F20.imprint","IMPRINT",FACE,{"disambiguationData":[TD([[makeQuery(id+"F20.imprint","IMPRINT",EDGE,{"derivedFrom":subQ2}),1.0]])]});}
            var Q127;
            {var subQ2=sQuery(id+"F20.wireOp",EDGE,"E30.113.0");Q127=makeQuery(id+"F20.imprint","IMPRINT",FACE,{"disambiguationData":[TD([[makeQuery(id+"F20.imprint","IMPRINT",EDGE,{"derivedFrom":subQ2}),1.0]])]});}
            var Q128;
            {var subQ2=sQuery(id+"F20.wireOp",EDGE,"E30.114.0");Q128=makeQuery(id+"F20.imprint","IMPRINT",FACE,{"disambiguationData":[TD([[makeQuery(id+"F20.imprint","IMPRINT",EDGE,{"derivedFrom":subQ2}),1.0]])]});}
            var Q129;
            {var subQ2=sQuery(id+"F20.wireOp",EDGE,"E30.83.0");Q129=makeQuery(id+"F20.imprint","IMPRINT",FACE,{"disambiguationData":[TD([[makeQuery(id+"F20.imprint","IMPRINT",EDGE,{"derivedFrom":subQ2}),1.0]])]});}
            var Q130;
            {var subQ2=sQuery(id+"F20.wireOp",EDGE,"E30.115.0");Q130=makeQuery(id+"F20.imprint","IMPRINT",FACE,{"disambiguationData":[TD([[makeQuery(id+"F20.imprint","IMPRINT",EDGE,{"derivedFrom":subQ2}),1.0]])]});}
            var Q131;
            {var subQ2=sQuery(id+"F20.wireOp",EDGE,"E30.85.0");Q131=makeQuery(id+"F20.imprint","IMPRINT",FACE,{"disambiguationData":[TD([[makeQuery(id+"F20.imprint","IMPRINT",EDGE,{"derivedFrom":subQ2}),1.0]])]});}
            var Q132;
            {var subQ2=sQuery(id+"F20.wireOp",EDGE,"E30.119.0");Q132=makeQuery(id+"F20.imprint","IMPRINT",FACE,{"disambiguationData":[TD([[makeQuery(id+"F20.imprint","IMPRINT",EDGE,{"derivedFrom":subQ2}),1.0]])]});}
            var Q133;
            {var subQ2=sQuery(id+"F20.wireOp",EDGE,"E30.103.0");Q133=makeQuery(id+"F20.imprint","IMPRINT",FACE,{"disambiguationData":[TD([[makeQuery(id+"F20.imprint","IMPRINT",EDGE,{"derivedFrom":subQ2}),1.0]])]});}
            var Q134;
            {var subQ2=sQuery(id+"F20.wireOp",EDGE,"E30.135.0");Q134=makeQuery(id+"F20.imprint","IMPRINT",FACE,{"disambiguationData":[TD([[makeQuery(id+"F20.imprint","IMPRINT",EDGE,{"derivedFrom":subQ2}),1.0]])]});}
            var Q135;
            {var subQ2=sQuery(id+"F20.wireOp",EDGE,"E30.106.0");Q135=makeQuery(id+"F20.imprint","IMPRINT",FACE,{"disambiguationData":[TD([[makeQuery(id+"F20.imprint","IMPRINT",EDGE,{"derivedFrom":subQ2}),1.0]])]});}
            var Q136;
            {var subQ2=sQuery(id+"F20.wireOp",EDGE,"E30.139.0");Q136=makeQuery(id+"F20.imprint","IMPRINT",FACE,{"disambiguationData":[TD([[makeQuery(id+"F20.imprint","IMPRINT",EDGE,{"derivedFrom":subQ2}),1.0]])]});}
            var Q137;
            {var subQ2=sQuery(id+"F20.wireOp",EDGE,"E30.110.0");Q137=makeQuery(id+"F20.imprint","IMPRINT",FACE,{"disambiguationData":[TD([[makeQuery(id+"F20.imprint","IMPRINT",EDGE,{"derivedFrom":subQ2}),1.0]])]});}
            var Q138;
            {var subQ2=sQuery(id+"F20.wireOp",EDGE,"E30.140.0");Q138=makeQuery(id+"F20.imprint","IMPRINT",FACE,{"disambiguationData":[TD([[makeQuery(id+"F20.imprint","IMPRINT",EDGE,{"derivedFrom":subQ2}),1.0]])]});}
            var Q139;
            {var subQ2=sQuery(id+"F20.wireOp",EDGE,"E30.111.0");Q139=makeQuery(id+"F20.imprint","IMPRINT",FACE,{"disambiguationData":[TD([[makeQuery(id+"F20.imprint","IMPRINT",EDGE,{"derivedFrom":subQ2}),1.0]])]});}
            var Q140;
            {var subQ2=sQuery(id+"F20.wireOp",EDGE,"E30.112.0");Q140=makeQuery(id+"F20.imprint","IMPRINT",FACE,{"disambiguationData":[TD([[makeQuery(id+"F20.imprint","IMPRINT",EDGE,{"derivedFrom":subQ2}),1.0]])]});}
            var Q141;
            {var subQ2=sQuery(id+"F20.wireOp",EDGE,"E30.31.0");Q141=makeQuery(id+"F20.imprint","IMPRINT",FACE,{"disambiguationData":[TD([[makeQuery(id+"F20.imprint","IMPRINT",EDGE,{"derivedFrom":subQ2}),1.0]])]});}
            var Q142;
            {var subQ2=sQuery(id+"F20.wireOp",EDGE,"E30.48.0");Q142=makeQuery(id+"F20.imprint","IMPRINT",FACE,{"disambiguationData":[TD([[makeQuery(id+"F20.imprint","IMPRINT",EDGE,{"derivedFrom":subQ2}),1.0]])]});}
            var Q143;
            {var subQ2=sQuery(id+"F20.wireOp",EDGE,"E30.51.0");Q143=makeQuery(id+"F20.imprint","IMPRINT",FACE,{"disambiguationData":[TD([[makeQuery(id+"F20.imprint","IMPRINT",EDGE,{"derivedFrom":subQ2}),1.0]])]});}
            var Q144;
            {var subQ2=sQuery(id+"F20.wireOp",EDGE,"E30.35.0");Q144=makeQuery(id+"F20.imprint","IMPRINT",FACE,{"disambiguationData":[TD([[makeQuery(id+"F20.imprint","IMPRINT",EDGE,{"derivedFrom":subQ2}),1.0]])]});}
            var Q145;
            {var subQ2=sQuery(id+"F20.wireOp",EDGE,"E30.36.0");Q145=makeQuery(id+"F20.imprint","IMPRINT",FACE,{"disambiguationData":[TD([[makeQuery(id+"F20.imprint","IMPRINT",EDGE,{"derivedFrom":subQ2}),1.0]])]});}
            var Q146;
            {var subQ2=sQuery(id+"F20.wireOp",EDGE,"E30.37.0");Q146=makeQuery(id+"F20.imprint","IMPRINT",FACE,{"disambiguationData":[TD([[makeQuery(id+"F20.imprint","IMPRINT",EDGE,{"derivedFrom":subQ2}),1.0]])]});}
            var Q147;
            {var subQ2=sQuery(id+"F20.wireOp",EDGE,"E30.38.0");Q147=makeQuery(id+"F20.imprint","IMPRINT",FACE,{"disambiguationData":[TD([[makeQuery(id+"F20.imprint","IMPRINT",EDGE,{"derivedFrom":subQ2}),1.0]])]});}
            var Q148;
            {var subQ2=sQuery(id+"F20.wireOp",EDGE,"E30.70.0");Q148=makeQuery(id+"F20.imprint","IMPRINT",FACE,{"disambiguationData":[TD([[makeQuery(id+"F20.imprint","IMPRINT",EDGE,{"derivedFrom":subQ2}),1.0]])]});}
            var Q149;
            {var subQ2=sQuery(id+"F20.wireOp",EDGE,"E30.57.0");Q149=makeQuery(id+"F20.imprint","IMPRINT",FACE,{"disambiguationData":[TD([[makeQuery(id+"F20.imprint","IMPRINT",EDGE,{"derivedFrom":subQ2}),1.0]])]});}
            var Q150;
            {var subQ2=sQuery(id+"F20.wireOp",EDGE,"E30.41.0");Q150=makeQuery(id+"F20.imprint","IMPRINT",FACE,{"disambiguationData":[TD([[makeQuery(id+"F20.imprint","IMPRINT",EDGE,{"derivedFrom":subQ2}),1.0]])]});}
            var Q151;
            {var subQ2=sQuery(id+"F20.wireOp",EDGE,"E30.73.0");Q151=makeQuery(id+"F20.imprint","IMPRINT",FACE,{"disambiguationData":[TD([[makeQuery(id+"F20.imprint","IMPRINT",EDGE,{"derivedFrom":subQ2}),1.0]])]});}
            var Q152;
            {var subQ2=sQuery(id+"F20.wireOp",EDGE,"E30.74.0");Q152=makeQuery(id+"F20.imprint","IMPRINT",FACE,{"disambiguationData":[TD([[makeQuery(id+"F20.imprint","IMPRINT",EDGE,{"derivedFrom":subQ2}),1.0]])]});}
            var Q153;
            {var subQ2=sQuery(id+"F20.wireOp",EDGE,"E30.62.0");Q153=makeQuery(id+"F20.imprint","IMPRINT",FACE,{"disambiguationData":[TD([[makeQuery(id+"F20.imprint","IMPRINT",EDGE,{"derivedFrom":subQ2}),1.0]])]});}
            var Q154;
            {var subQ2=sQuery(id+"F20.wireOp",EDGE,"E30.63.0");Q154=makeQuery(id+"F20.imprint","IMPRINT",FACE,{"disambiguationData":[TD([[makeQuery(id+"F20.imprint","IMPRINT",EDGE,{"derivedFrom":subQ2}),1.0]])]});}
            var Q155;
            {var subQ2=sQuery(id+"F20.wireOp",EDGE,"E30.47.0");Q155=makeQuery(id+"F20.imprint","IMPRINT",FACE,{"disambiguationData":[TD([[makeQuery(id+"F20.imprint","IMPRINT",EDGE,{"derivedFrom":subQ2}),1.0]])]});}
            var Q156;
            {var subQ2=sQuery(id+"F20.wireOp",EDGE,"E30.64.0");Q156=makeQuery(id+"F20.imprint","IMPRINT",FACE,{"disambiguationData":[TD([[makeQuery(id+"F20.imprint","IMPRINT",EDGE,{"derivedFrom":subQ2}),1.0]])]});}
            var Q157;
            {var subQ2=sQuery(id+"F20.wireOp",EDGE,"E30.65.0");Q157=makeQuery(id+"F20.imprint","IMPRINT",FACE,{"disambiguationData":[TD([[makeQuery(id+"F20.imprint","IMPRINT",EDGE,{"derivedFrom":subQ2}),1.0]])]});}
            var Q158;
            {var subQ2=sQuery(id+"F20.wireOp",EDGE,"E30.33.0");Q158=makeQuery(id+"F20.imprint","IMPRINT",FACE,{"disambiguationData":[TD([[makeQuery(id+"F20.imprint","IMPRINT",EDGE,{"derivedFrom":subQ2}),1.0]])]});}
            var Q159;
            {var subQ2=sQuery(id+"F20.wireOp",EDGE,"E30.66.0");Q159=makeQuery(id+"F20.imprint","IMPRINT",FACE,{"disambiguationData":[TD([[makeQuery(id+"F20.imprint","IMPRINT",EDGE,{"derivedFrom":subQ2}),1.0]])]});}
            var Q160;
            {var subQ2=sQuery(id+"F20.wireOp",EDGE,"E30.34.0");Q160=makeQuery(id+"F20.imprint","IMPRINT",FACE,{"disambiguationData":[TD([[makeQuery(id+"F20.imprint","IMPRINT",EDGE,{"derivedFrom":subQ2}),1.0]])]});}
            var Q161;
            {var subQ2=sQuery(id+"F20.wireOp",EDGE,"E30.67.0");Q161=makeQuery(id+"F20.imprint","IMPRINT",FACE,{"disambiguationData":[TD([[makeQuery(id+"F20.imprint","IMPRINT",EDGE,{"derivedFrom":subQ2}),1.0]])]});}
            var Q162;
            {var subQ2=sQuery(id+"F20.wireOp",EDGE,"E30.52.0");Q162=makeQuery(id+"F20.imprint","IMPRINT",FACE,{"disambiguationData":[TD([[makeQuery(id+"F20.imprint","IMPRINT",EDGE,{"derivedFrom":subQ2}),1.0]])]});}
            var Q163;
            {var subQ2=sQuery(id+"F20.wireOp",EDGE,"E30.53.0");Q163=makeQuery(id+"F20.imprint","IMPRINT",FACE,{"disambiguationData":[TD([[makeQuery(id+"F20.imprint","IMPRINT",EDGE,{"derivedFrom":subQ2}),1.0]])]});}
            var Q164;
            {var subQ2=sQuery(id+"F20.wireOp",EDGE,"E30.69.0");Q164=makeQuery(id+"F20.imprint","IMPRINT",FACE,{"disambiguationData":[TD([[makeQuery(id+"F20.imprint","IMPRINT",EDGE,{"derivedFrom":subQ2}),1.0]])]});}
            var Q165;
            {var subQ2=sQuery(id+"F20.wireOp",EDGE,"E30.39.0");Q165=makeQuery(id+"F20.imprint","IMPRINT",FACE,{"disambiguationData":[TD([[makeQuery(id+"F20.imprint","IMPRINT",EDGE,{"derivedFrom":subQ2}),1.0]])]});}
            var Q166;
            {var subQ2=sQuery(id+"F20.wireOp",EDGE,"E30.56.0");Q166=makeQuery(id+"F20.imprint","IMPRINT",FACE,{"disambiguationData":[TD([[makeQuery(id+"F20.imprint","IMPRINT",EDGE,{"derivedFrom":subQ2}),1.0]])]});}
            var Q167;
            {var subQ2=sQuery(id+"F20.wireOp",EDGE,"E30.40.0");Q167=makeQuery(id+"F20.imprint","IMPRINT",FACE,{"disambiguationData":[TD([[makeQuery(id+"F20.imprint","IMPRINT",EDGE,{"derivedFrom":subQ2}),1.0]])]});}
            var Q168;
            {var subQ2=sQuery(id+"F20.wireOp",EDGE,"E30.72.0");Q168=makeQuery(id+"F20.imprint","IMPRINT",FACE,{"disambiguationData":[TD([[makeQuery(id+"F20.imprint","IMPRINT",EDGE,{"derivedFrom":subQ2}),1.0]])]});}
            var Q169;
            {var subQ2=sQuery(id+"F20.wireOp",EDGE,"E30.58.0");Q169=makeQuery(id+"F20.imprint","IMPRINT",FACE,{"disambiguationData":[TD([[makeQuery(id+"F20.imprint","IMPRINT",EDGE,{"derivedFrom":subQ2}),1.0]])]});}
            var Q170;
            {var subQ2=sQuery(id+"F20.wireOp",EDGE,"E30.42.0");Q170=makeQuery(id+"F20.imprint","IMPRINT",FACE,{"disambiguationData":[TD([[makeQuery(id+"F20.imprint","IMPRINT",EDGE,{"derivedFrom":subQ2}),1.0]])]});}
            var Q171;
            {var subQ2=sQuery(id+"F20.wireOp",EDGE,"E30.59.0");Q171=makeQuery(id+"F20.imprint","IMPRINT",FACE,{"disambiguationData":[TD([[makeQuery(id+"F20.imprint","IMPRINT",EDGE,{"derivedFrom":subQ2}),1.0]])]});}
            var Q172;
            {var subQ2=sQuery(id+"F20.wireOp",EDGE,"E30.43.0");Q172=makeQuery(id+"F20.imprint","IMPRINT",FACE,{"disambiguationData":[TD([[makeQuery(id+"F20.imprint","IMPRINT",EDGE,{"derivedFrom":subQ2}),1.0]])]});}
            var Q173;
            {var subQ2=sQuery(id+"F20.wireOp",EDGE,"E30.75.0");Q173=makeQuery(id+"F20.imprint","IMPRINT",FACE,{"disambiguationData":[TD([[makeQuery(id+"F20.imprint","IMPRINT",EDGE,{"derivedFrom":subQ2}),1.0]])]});}
            var Q174;
            {var subQ2=sQuery(id+"F20.wireOp",EDGE,"E30.46.0");Q174=makeQuery(id+"F20.imprint","IMPRINT",FACE,{"disambiguationData":[TD([[makeQuery(id+"F20.imprint","IMPRINT",EDGE,{"derivedFrom":subQ2}),1.0]])]});}
            var Q175;
            {var subQ2=sQuery(id+"F20.wireOp",EDGE,"E30.76.0");Q175=makeQuery(id+"F20.imprint","IMPRINT",FACE,{"disambiguationData":[TD([[makeQuery(id+"F20.imprint","IMPRINT",EDGE,{"derivedFrom":subQ2}),1.0]])]});}
            var Q176;
            {var subQ2=sQuery(id+"F20.wireOp",EDGE,"E30.60.0");Q176=makeQuery(id+"F20.imprint","IMPRINT",FACE,{"disambiguationData":[TD([[makeQuery(id+"F20.imprint","IMPRINT",EDGE,{"derivedFrom":subQ2}),1.0]])]});}
            var Q177;
            {var subQ2=sQuery(id+"F20.wireOp",EDGE,"E30.77.0");Q177=makeQuery(id+"F20.imprint","IMPRINT",FACE,{"disambiguationData":[TD([[makeQuery(id+"F20.imprint","IMPRINT",EDGE,{"derivedFrom":subQ2}),1.0]])]});}
            var Q178;
            {var subQ2=sQuery(id+"F20.wireOp",EDGE,"E30.61.0");Q178=makeQuery(id+"F20.imprint","IMPRINT",FACE,{"disambiguationData":[TD([[makeQuery(id+"F20.imprint","IMPRINT",EDGE,{"derivedFrom":subQ2}),1.0]])]});}
            var Q179;
            {var subQ2=sQuery(id+"F20.wireOp",EDGE,"E30.45.0");Q179=makeQuery(id+"F20.imprint","IMPRINT",FACE,{"disambiguationData":[TD([[makeQuery(id+"F20.imprint","IMPRINT",EDGE,{"derivedFrom":subQ2}),1.0]])]});}
            var Q180;
            {var subQ2=sQuery(id+"F20.wireOp",EDGE,"E30.32.0");Q180=makeQuery(id+"F20.imprint","IMPRINT",FACE,{"disambiguationData":[TD([[makeQuery(id+"F20.imprint","IMPRINT",EDGE,{"derivedFrom":subQ2}),1.0]])]});}
            var Q181;
            {var subQ2=sQuery(id+"F20.wireOp",EDGE,"E30.49.0");Q181=makeQuery(id+"F20.imprint","IMPRINT",FACE,{"disambiguationData":[TD([[makeQuery(id+"F20.imprint","IMPRINT",EDGE,{"derivedFrom":subQ2}),1.0]])]});}
            var Q182;
            {var subQ2=sQuery(id+"F20.wireOp",EDGE,"E30.50.0");Q182=makeQuery(id+"F20.imprint","IMPRINT",FACE,{"disambiguationData":[TD([[makeQuery(id+"F20.imprint","IMPRINT",EDGE,{"derivedFrom":subQ2}),1.0]])]});}
            var Q183;
            {var subQ2=sQuery(id+"F20.wireOp",EDGE,"E30.68.0");Q183=makeQuery(id+"F20.imprint","IMPRINT",FACE,{"disambiguationData":[TD([[makeQuery(id+"F20.imprint","IMPRINT",EDGE,{"derivedFrom":subQ2}),1.0]])]});}
            var Q184;
            {var subQ2=sQuery(id+"F20.wireOp",EDGE,"E30.54.0");Q184=makeQuery(id+"F20.imprint","IMPRINT",FACE,{"disambiguationData":[TD([[makeQuery(id+"F20.imprint","IMPRINT",EDGE,{"derivedFrom":subQ2}),1.0]])]});}
            var Q185;
            {var subQ2=sQuery(id+"F20.wireOp",EDGE,"E30.71.0");Q185=makeQuery(id+"F20.imprint","IMPRINT",FACE,{"disambiguationData":[TD([[makeQuery(id+"F20.imprint","IMPRINT",EDGE,{"derivedFrom":subQ2}),1.0]])]});}
            var Q186;
            {var subQ2=sQuery(id+"F20.wireOp",EDGE,"E30.44.0");Q186=makeQuery(id+"F20.imprint","IMPRINT",FACE,{"disambiguationData":[TD([[makeQuery(id+"F20.imprint","IMPRINT",EDGE,{"derivedFrom":subQ2}),1.0]])]});}
            var Q187;
            {var subQ2=sQuery(id+"F20.wireOp",EDGE,"E30.55.0");Q187=makeQuery(id+"F20.imprint","IMPRINT",FACE,{"disambiguationData":[TD([[makeQuery(id+"F20.imprint","IMPRINT",EDGE,{"derivedFrom":subQ2}),1.0]])]});}
            var Q188;
            {var subQ2=sQuery(id+"F20.wireOp",EDGE,"E30.22.0");Q188=makeQuery(id+"F20.imprint","IMPRINT",FACE,{"disambiguationData":[TD([[makeQuery(id+"F20.imprint","IMPRINT",EDGE,{"derivedFrom":subQ2}),1.0]])]});}
            var Q189;
            {var subQ2=sQuery(id+"F20.wireOp",EDGE,"E30.28.0");Q189=makeQuery(id+"F20.imprint","IMPRINT",FACE,{"disambiguationData":[TD([[makeQuery(id+"F20.imprint","IMPRINT",EDGE,{"derivedFrom":subQ2}),1.0]])]});}
            var Q190;
            {var subQ2=sQuery(id+"F20.wireOp",EDGE,"E30.16.0");Q190=makeQuery(id+"F20.imprint","IMPRINT",FACE,{"disambiguationData":[TD([[makeQuery(id+"F20.imprint","IMPRINT",EDGE,{"derivedFrom":subQ2}),1.0]])]});}
            var Q191;
            {var subQ2=sQuery(id+"F20.wireOp",EDGE,"E30.18.0");Q191=makeQuery(id+"F20.imprint","IMPRINT",FACE,{"disambiguationData":[TD([[makeQuery(id+"F20.imprint","IMPRINT",EDGE,{"derivedFrom":subQ2}),1.0]])]});}
            var Q192;
            {var subQ2=sQuery(id+"F20.wireOp",EDGE,"E30.19.0");Q192=makeQuery(id+"F20.imprint","IMPRINT",FACE,{"disambiguationData":[TD([[makeQuery(id+"F20.imprint","IMPRINT",EDGE,{"derivedFrom":subQ2}),1.0]])]});}
            var Q193;
            {var subQ2=sQuery(id+"F20.wireOp",EDGE,"E30.20.0");Q193=makeQuery(id+"F20.imprint","IMPRINT",FACE,{"disambiguationData":[TD([[makeQuery(id+"F20.imprint","IMPRINT",EDGE,{"derivedFrom":subQ2}),1.0]])]});}
            var Q194;
            {var subQ2=sQuery(id+"F20.wireOp",EDGE,"E30.13.0");Q194=makeQuery(id+"F20.imprint","IMPRINT",FACE,{"disambiguationData":[TD([[makeQuery(id+"F20.imprint","IMPRINT",EDGE,{"derivedFrom":subQ2}),1.0]])]});}
            var Q195;
            {var subQ2=sQuery(id+"F20.wireOp",EDGE,"E30.23.0");Q195=makeQuery(id+"F20.imprint","IMPRINT",FACE,{"disambiguationData":[TD([[makeQuery(id+"F20.imprint","IMPRINT",EDGE,{"derivedFrom":subQ2}),1.0]])]});}
            var Q196;
            {var subQ2=sQuery(id+"F20.wireOp",EDGE,"E30.26.0");Q196=makeQuery(id+"F20.imprint","IMPRINT",FACE,{"disambiguationData":[TD([[makeQuery(id+"F20.imprint","IMPRINT",EDGE,{"derivedFrom":subQ2}),1.0]])]});}
            var Q197;
            {var subQ2=sQuery(id+"F20.wireOp",EDGE,"E30.27.0");Q197=makeQuery(id+"F20.imprint","IMPRINT",FACE,{"disambiguationData":[TD([[makeQuery(id+"F20.imprint","IMPRINT",EDGE,{"derivedFrom":subQ2}),1.0]])]});}
            var Q198;
            {var subQ2=sQuery(id+"F20.wireOp",EDGE,"E30.29.0");Q198=makeQuery(id+"F20.imprint","IMPRINT",FACE,{"disambiguationData":[TD([[makeQuery(id+"F20.imprint","IMPRINT",EDGE,{"derivedFrom":subQ2}),1.0]])]});}
            var Q199;
            {var subQ2=sQuery(id+"F20.wireOp",EDGE,"E30.14.0");Q199=makeQuery(id+"F20.imprint","IMPRINT",FACE,{"disambiguationData":[TD([[makeQuery(id+"F20.imprint","IMPRINT",EDGE,{"derivedFrom":subQ2}),1.0]])]});}
            var Q200;
            {var subQ2=sQuery(id+"F20.wireOp",EDGE,"E30.3.0");Q200=makeQuery(id+"F20.imprint","IMPRINT",FACE,{"disambiguationData":[TD([[makeQuery(id+"F20.imprint","IMPRINT",EDGE,{"derivedFrom":subQ2}),1.0]])]});}
            var Q201;
            {var subQ2=sQuery(id+"F20.wireOp",EDGE,"E30.4.0");Q201=makeQuery(id+"F20.imprint","IMPRINT",FACE,{"disambiguationData":[TD([[makeQuery(id+"F20.imprint","IMPRINT",EDGE,{"derivedFrom":subQ2}),1.0]])]});}
            var Q202;
            {var subQ2=sQuery(id+"F20.wireOp",EDGE,"E30.5.0");Q202=makeQuery(id+"F20.imprint","IMPRINT",FACE,{"disambiguationData":[TD([[makeQuery(id+"F20.imprint","IMPRINT",EDGE,{"derivedFrom":subQ2}),1.0]])]});}
            var Q203;
            {var subQ2=sQuery(id+"F20.wireOp",EDGE,"E30.8.0");Q203=makeQuery(id+"F20.imprint","IMPRINT",FACE,{"disambiguationData":[TD([[makeQuery(id+"F20.imprint","IMPRINT",EDGE,{"derivedFrom":subQ2}),1.0]])]});}
            var Q204;
            {var subQ2=sQuery(id+"F20.wireOp",EDGE,"E30.9.0");Q204=makeQuery(id+"F20.imprint","IMPRINT",FACE,{"disambiguationData":[TD([[makeQuery(id+"F20.imprint","IMPRINT",EDGE,{"derivedFrom":subQ2}),1.0]])]});}
            var Q205;
            {var subQ2=sQuery(id+"F20.wireOp",EDGE,"E30.10.0");Q205=makeQuery(id+"F20.imprint","IMPRINT",FACE,{"disambiguationData":[TD([[makeQuery(id+"F20.imprint","IMPRINT",EDGE,{"derivedFrom":subQ2}),1.0]])]});}
            var Q206;
            {var subQ2=sQuery(id+"F20.wireOp",EDGE,"E30.11.0");Q206=makeQuery(id+"F20.imprint","IMPRINT",FACE,{"disambiguationData":[TD([[makeQuery(id+"F20.imprint","IMPRINT",EDGE,{"derivedFrom":subQ2}),1.0]])]});}
            var Q207;
            {var subQ2=sQuery(id+"F20.wireOp",EDGE,"E30.21.0");Q207=makeQuery(id+"F20.imprint","IMPRINT",FACE,{"disambiguationData":[TD([[makeQuery(id+"F20.imprint","IMPRINT",EDGE,{"derivedFrom":subQ2}),1.0]])]});}
            var Q208;
            {var subQ2=sQuery(id+"F20.wireOp",EDGE,"E30.30.0");Q208=makeQuery(id+"F20.imprint","IMPRINT",FACE,{"disambiguationData":[TD([[makeQuery(id+"F20.imprint","IMPRINT",EDGE,{"derivedFrom":subQ2}),1.0]])]});}
            var Q209;
            {var subQ2=sQuery(id+"F20.wireOp",EDGE,"E30.15.0");Q209=makeQuery(id+"F20.imprint","IMPRINT",FACE,{"disambiguationData":[TD([[makeQuery(id+"F20.imprint","IMPRINT",EDGE,{"derivedFrom":subQ2}),1.0]])]});}
            var Q210;
            {var subQ2=sQuery(id+"F20.wireOp",EDGE,"E30.17.0");Q210=makeQuery(id+"F20.imprint","IMPRINT",FACE,{"disambiguationData":[TD([[makeQuery(id+"F20.imprint","IMPRINT",EDGE,{"derivedFrom":subQ2}),1.0]])]});}
            var Q211;
            {var subQ2=sQuery(id+"F20.wireOp",EDGE,"E30.12.0");Q211=makeQuery(id+"F20.imprint","IMPRINT",FACE,{"disambiguationData":[TD([[makeQuery(id+"F20.imprint","IMPRINT",EDGE,{"derivedFrom":subQ2}),1.0]])]});}
            var Q212;
            {var subQ2=sQuery(id+"F20.wireOp",EDGE,"E30.1.0");Q212=makeQuery(id+"F20.imprint","IMPRINT",FACE,{"disambiguationData":[TD([[makeQuery(id+"F20.imprint","IMPRINT",EDGE,{"derivedFrom":subQ2}),1.0]])]});}
            var Q213;
            {var subQ2=sQuery(id+"F20.wireOp",EDGE,"E30.6.0");Q213=makeQuery(id+"F20.imprint","IMPRINT",FACE,{"disambiguationData":[TD([[makeQuery(id+"F20.imprint","IMPRINT",EDGE,{"derivedFrom":subQ2}),1.0]])]});}
            var Q214;
            {var subQ2=sQuery(id+"F20.wireOp",EDGE,"E30.7.0");Q214=makeQuery(id+"F20.imprint","IMPRINT",FACE,{"disambiguationData":[TD([[makeQuery(id+"F20.imprint","IMPRINT",EDGE,{"derivedFrom":subQ2}),1.0]])]});}
            var Q215;
            {var subQ2=sQuery(id+"F20.wireOp",EDGE,"E30.24.0");Q215=makeQuery(id+"F20.imprint","IMPRINT",FACE,{"disambiguationData":[TD([[makeQuery(id+"F20.imprint","IMPRINT",EDGE,{"derivedFrom":subQ2}),1.0]])]});}
            var Q216;
            {var subQ2=sQuery(id+"F20.wireOp",EDGE,"E30.25.0");Q216=makeQuery(id+"F20.imprint","IMPRINT",FACE,{"disambiguationData":[TD([[makeQuery(id+"F20.imprint","IMPRINT",EDGE,{"derivedFrom":subQ2}),1.0]])]});}
            var Q217;
            {var subQ2=sQuery(id+"F20.wireOp",EDGE,"E30.219.0");Q217=makeQuery(id+"F20.imprint","IMPRINT",FACE,{"disambiguationData":[TD([[makeQuery(id+"F20.imprint","IMPRINT",EDGE,{"derivedFrom":subQ2}),1.0]])]});}
            var Q218;
            {var subQ2=sQuery(id+"F20.wireOp",EDGE,"E25");Q218=makeQuery(id+"F20.imprint","IMPRINT",FACE,{"disambiguationData":[TD([[makeQuery(id+"F20.imprint","IMPRINT",EDGE,{"derivedFrom":subQ2}),1.0]])]});}
            var Q219;
            {var subQ2=sQuery(id+"F20.wireOp",EDGE,"E30.2.0");Q219=makeQuery(id+"F20.imprint","IMPRINT",FACE,{"disambiguationData":[TD([[makeQuery(id+"F20.imprint","IMPRINT",EDGE,{"derivedFrom":subQ2}),1.0]])]});}
            extrude(context, id + "F21", {"entities" : qUnion([Q0, Q1, Q2, Q3, Q4, Q5, Q6, Q7, Q8, Q9, Q10, Q11, Q12, Q13, Q14, Q15, Q16, Q17, Q18, Q19, Q20, Q21, Q22, Q23, Q24, Q25, Q26, Q27, Q28, Q29, Q30, Q31, Q32, Q33, Q34, Q35, Q36, Q37, Q38, Q39, Q40, Q41, Q42, Q43, Q44, Q45, Q46, Q47, Q48, Q49, Q50, Q51, Q52, Q53, Q54, Q55, Q56, Q57, Q58, Q59, Q60, Q61, Q62, Q63, Q64, Q65, Q66, Q67, Q68, Q69, Q70, Q71, Q72, Q73, Q74, Q75, Q76, Q77, Q78, Q79, Q80, Q81, Q82, Q83, Q84, Q85, Q86, Q87, Q88, Q89, Q90, Q91, Q92, Q93, Q94, Q95, Q96, Q97, Q98, Q99, Q100, Q101, Q102, Q103, Q104, Q105, Q106, Q107, Q108, Q109, Q110, Q111, Q112, Q113, Q114, Q115, Q116, Q117, Q118, Q119, Q120, Q121, Q122, Q123, Q124, Q125, Q126, Q127, Q128, Q129, Q130, Q131, Q132, Q133, Q134, Q135, Q136, Q137, Q138, Q139, Q140, Q141, Q142, Q143, Q144, Q145, Q146, Q147, Q148, Q149, Q150, Q151, Q152, Q153, Q154, Q155, Q156, Q157, Q158, Q159, Q160, Q161, Q162, Q163, Q164, Q165, Q166, Q167, Q168, Q169, Q170, Q171, Q172, Q173, Q174, Q175, Q176, Q177, Q178, Q179, Q180, Q181, Q182, Q183, Q184, Q185, Q186, Q187, Q188, Q189, Q190, Q191, Q192, Q193, Q194, Q195, Q196, Q197, Q198, Q199, Q200, Q201, Q202, Q203, Q204, Q205, Q206, Q207, Q208, Q209, Q210, Q211, Q212, Q213, Q214, Q215, Q216, Q217, Q218, Q219]), "operationType" : NewBodyOperationType.REMOVE, "oppositeDirection" : true, "depth" : 25 * mm});
        }
    });
